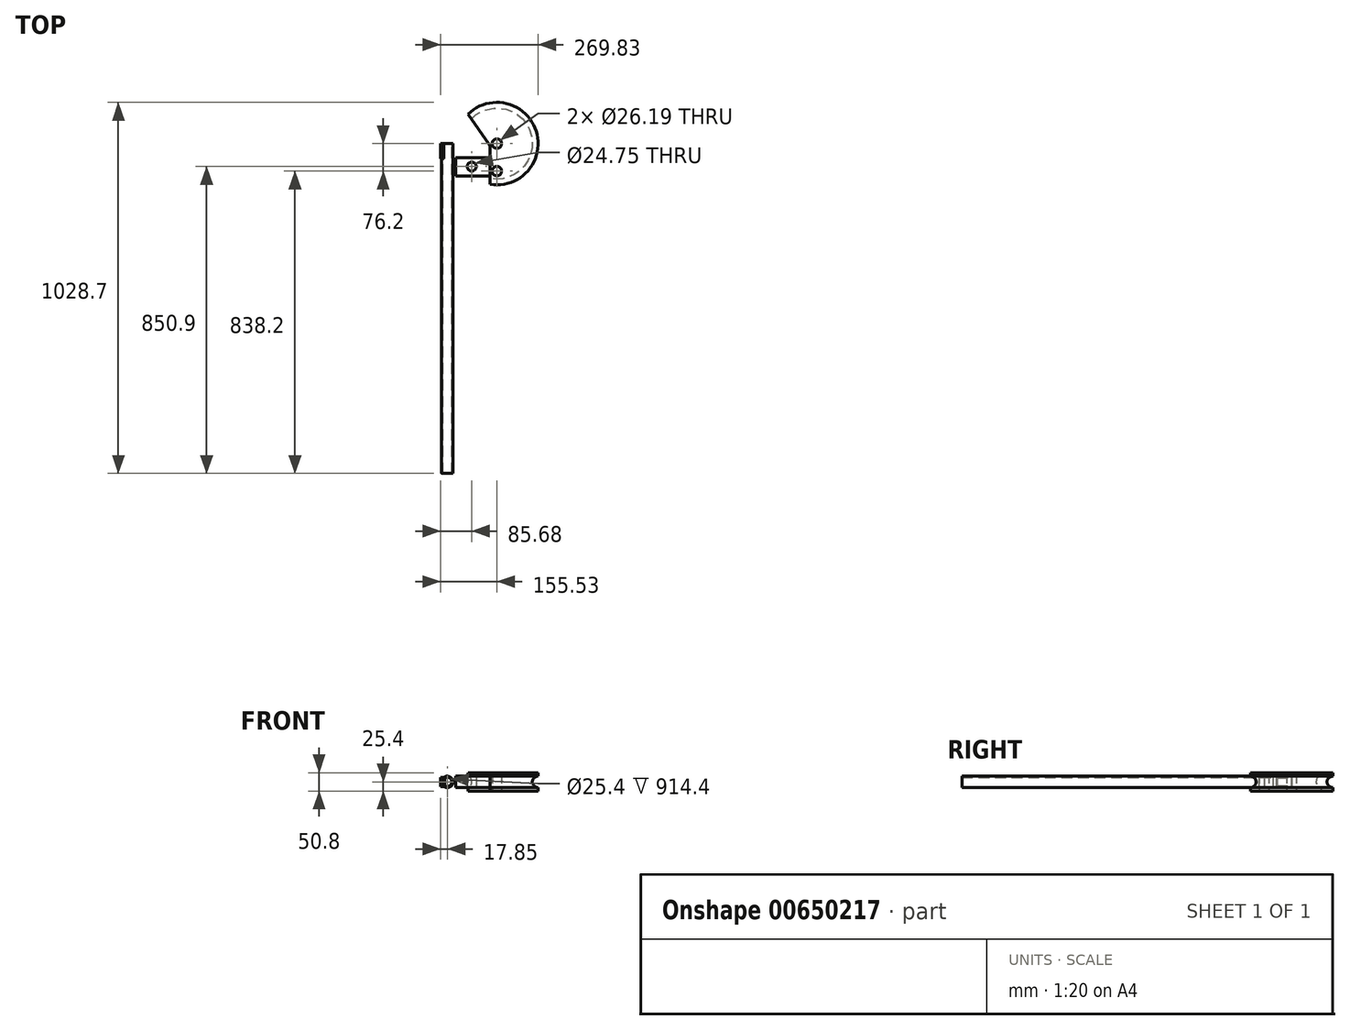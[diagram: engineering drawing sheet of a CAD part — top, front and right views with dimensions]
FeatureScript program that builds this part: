
annotation { "Feature Type Name" : "Feature", "Feature Type Description" : "" }
export const myFeature = defineFeature(function(context is Context, id is Id, definition is map)
    precondition{}
    {
        {
            var Q0;
            Q0=qCreatedBy(makeId("Top.planeOp"),FACE);
            var sketch = newSketch(context, id + "F0", { "sketchPlane" : qUnion([Q0])});
            skArc(sketch, "E0", {"start": v(-19.05, -112.7) * mm, "mid": v(109, 34.37) * mm, "end": v(-80.25, 81.4) * mm});
            skCircle(sketch, "E1", {"center": v(0, 0) * mm, "radius": 13.1 * mm});
            skLineSegment(sketch, "E2", {"start": v(0, 0) * mm, "end": v(0, -166.98) * mm, "construction": true});
            skLineSegment(sketch, "E3", {"start": v(0, 0) * mm, "end": v(-105.24, 150.3) * mm, "construction": true});
            skLineSegment(sketch, "E4.0", {"start": v(-19.05, -6) * mm, "end": v(-80.25, 81.4) * mm});
            skLineSegment(sketch, "E4.1", {"start": v(-19.05, -6) * mm, "end": v(-19.05, -112.7) * mm});
            skSolve(sketch);
        }
        {
            var Q0;
            Q0 = qSketchRegion(id + "F0", true);
            extrude(context, id + "F1", {"entities" : qUnion([Q0]), "endBound" : BoundingType.SYMMETRIC, "depth" : 50.8 * mm, "offsetDistance" : 25.4 * mm});
        }
        {
            var Q0;
            Q0=qCreatedBy(makeId("Top.planeOp"),FACE);
            var sketch = newSketch(context, id + "F2", { "sketchPlane" : qUnion([Q0])});
            skLineSegment(sketch, "E5", {"start": v(14.64, 175.52) * mm, "end": v(14.64, 166) * mm});
            skLineSegment(sketch, "E6", {"start": v(22.02, 212) * mm, "end": v(23.53, 220.42) * mm});
            skLineSegment(sketch, "E7", {"start": v(21.47, 208.86) * mm, "end": v(21.75, 210.43) * mm});
            skLineSegment(sketch, "E8", {"start": v(19.5, 197.94) * mm, "end": v(21.18, 207.32) * mm});
            skLineSegment(sketch, "E9", {"start": v(18.95, 194.8) * mm, "end": v(19.23, 196.37) * mm});
            skLineSegment(sketch, "E10", {"start": v(16.99, 183.86) * mm, "end": v(18.66, 193.24) * mm});
            skLineSegment(sketch, "E11", {"start": v(16.44, 180.75) * mm, "end": v(16.71, 182.3) * mm});
            skLineSegment(sketch, "E12", {"start": v(14.64, 170.76) * mm, "end": v(16.16, 179.19) * mm});
            skLineSegment(sketch, "E13", {"start": v(208.16, 163.65) * mm, "end": v(205.14, 165.03) * mm});
            skLineSegment(sketch, "E14", {"start": v(207.72, 164.56) * mm, "end": v(207.57, 164.88) * mm});
            skLineSegment(sketch, "E15", {"start": v(207.57, 164.88) * mm, "end": v(207.25, 165.17) * mm});
            skLineSegment(sketch, "E16", {"start": v(207.25, 165.17) * mm, "end": v(206.8, 165.32) * mm});
            skLineSegment(sketch, "E17", {"start": v(206.8, 165.32) * mm, "end": v(206.51, 165.32) * mm});
            skLineSegment(sketch, "E18", {"start": v(206.51, 165.32) * mm, "end": v(206.05, 165.17) * mm});
            skLineSegment(sketch, "E19", {"start": v(206.05, 165.17) * mm, "end": v(205.75, 164.88) * mm});
            skLineSegment(sketch, "E20", {"start": v(205.75, 164.88) * mm, "end": v(205.6, 164.56) * mm});
            skLineSegment(sketch, "E21", {"start": v(205.6, 164.56) * mm, "end": v(205.6, 164.12) * mm});
            skLineSegment(sketch, "E22", {"start": v(205.6, 164.12) * mm, "end": v(205.75, 163.82) * mm});
            skLineSegment(sketch, "E23", {"start": v(205.75, 163.82) * mm, "end": v(206.05, 163.5) * mm});
            skLineSegment(sketch, "E24", {"start": v(206.05, 163.5) * mm, "end": v(206.51, 163.35) * mm});
            skLineSegment(sketch, "E25", {"start": v(206.51, 163.35) * mm, "end": v(206.8, 163.35) * mm});
            skLineSegment(sketch, "E26", {"start": v(206.8, 163.35) * mm, "end": v(207.25, 163.5) * mm});
            skLineSegment(sketch, "E27", {"start": v(207.25, 163.5) * mm, "end": v(207.57, 163.82) * mm});
            skLineSegment(sketch, "E28", {"start": v(207.57, 163.82) * mm, "end": v(207.72, 164.12) * mm});
            skLineSegment(sketch, "E29", {"start": v(207.72, 164.12) * mm, "end": v(207.72, 164.56) * mm});
            skLineSegment(sketch, "E30", {"start": v(208.78, 166.38) * mm, "end": v(208.63, 166.53) * mm});
            skLineSegment(sketch, "E31", {"start": v(208.63, 166.53) * mm, "end": v(208.78, 166.68) * mm});
            skLineSegment(sketch, "E32", {"start": v(208.78, 166.68) * mm, "end": v(208.93, 166.53) * mm});
            skLineSegment(sketch, "E33", {"start": v(208.93, 166.53) * mm, "end": v(208.78, 166.38) * mm});
            skLineSegment(sketch, "E34", {"start": v(208.78, 166.38) * mm, "end": v(208.48, 166.38) * mm});
            skLineSegment(sketch, "E35", {"start": v(208.48, 166.38) * mm, "end": v(208.16, 166.53) * mm});
            skLineSegment(sketch, "E36", {"start": v(208.16, 166.53) * mm, "end": v(208.02, 166.68) * mm});
            skLineSegment(sketch, "E37", {"start": v(208.78, 167.3) * mm, "end": v(208.63, 167.44) * mm});
            skLineSegment(sketch, "E38", {"start": v(208.63, 167.44) * mm, "end": v(208.78, 167.59) * mm});
            skLineSegment(sketch, "E39", {"start": v(208.78, 167.59) * mm, "end": v(208.93, 167.44) * mm});
            skLineSegment(sketch, "E40", {"start": v(208.93, 167.44) * mm, "end": v(208.78, 167.3) * mm});
            skLineSegment(sketch, "E41", {"start": v(208.78, 167.3) * mm, "end": v(208.48, 167.3) * mm});
            skLineSegment(sketch, "E42", {"start": v(208.48, 167.3) * mm, "end": v(208.16, 167.44) * mm});
            skLineSegment(sketch, "E43", {"start": v(208.16, 167.44) * mm, "end": v(208.02, 167.59) * mm});
            skLineSegment(sketch, "E44", {"start": v(206.2, 170.61) * mm, "end": v(205.92, 170.57) * mm});
            skLineSegment(sketch, "E45", {"start": v(205.92, 170.57) * mm, "end": v(205.67, 170.47) * mm});
            skLineSegment(sketch, "E46", {"start": v(205.67, 170.47) * mm, "end": v(205.45, 170.3) * mm});
            skLineSegment(sketch, "E47", {"start": v(205.45, 170.3) * mm, "end": v(205.28, 170.08) * mm});
            skLineSegment(sketch, "E48", {"start": v(205.28, 170.08) * mm, "end": v(205.18, 169.83) * mm});
            skLineSegment(sketch, "E49", {"start": v(205.18, 169.83) * mm, "end": v(205.14, 169.56) * mm});
            skLineSegment(sketch, "E50", {"start": v(205.14, 169.56) * mm, "end": v(205.18, 169.28) * mm});
            skLineSegment(sketch, "E51", {"start": v(205.18, 169.28) * mm, "end": v(205.28, 169.03) * mm});
            skLineSegment(sketch, "E52", {"start": v(205.28, 169.03) * mm, "end": v(205.45, 168.81) * mm});
            skLineSegment(sketch, "E53", {"start": v(205.45, 168.81) * mm, "end": v(205.67, 168.65) * mm});
            skLineSegment(sketch, "E54", {"start": v(205.67, 168.65) * mm, "end": v(205.92, 168.54) * mm});
            skLineSegment(sketch, "E55", {"start": v(205.92, 168.54) * mm, "end": v(206.2, 168.5) * mm});
            skLineSegment(sketch, "E56", {"start": v(206.2, 168.5) * mm, "end": v(207.25, 168.5) * mm});
            skLineSegment(sketch, "E57", {"start": v(207.25, 168.5) * mm, "end": v(207.53, 168.54) * mm});
            skLineSegment(sketch, "E58", {"start": v(207.53, 168.54) * mm, "end": v(207.78, 168.65) * mm});
            skLineSegment(sketch, "E59", {"start": v(207.78, 168.65) * mm, "end": v(208.02, 168.81) * mm});
            skLineSegment(sketch, "E60", {"start": v(208.02, 168.81) * mm, "end": v(208.18, 169.03) * mm});
            skLineSegment(sketch, "E61", {"start": v(208.18, 169.03) * mm, "end": v(208.3, 169.28) * mm});
            skLineSegment(sketch, "E62", {"start": v(208.3, 169.28) * mm, "end": v(208.31, 169.56) * mm});
            skLineSegment(sketch, "E63", {"start": v(208.31, 169.56) * mm, "end": v(208.3, 169.83) * mm});
            skLineSegment(sketch, "E64", {"start": v(208.3, 169.83) * mm, "end": v(208.18, 170.08) * mm});
            skLineSegment(sketch, "E65", {"start": v(208.18, 170.08) * mm, "end": v(208.02, 170.3) * mm});
            skLineSegment(sketch, "E66", {"start": v(208.02, 170.3) * mm, "end": v(207.78, 170.47) * mm});
            skLineSegment(sketch, "E67", {"start": v(207.78, 170.47) * mm, "end": v(207.53, 170.57) * mm});
            skLineSegment(sketch, "E68", {"start": v(207.53, 170.57) * mm, "end": v(207.25, 170.61) * mm});
            skLineSegment(sketch, "E69", {"start": v(207.25, 170.61) * mm, "end": v(206.2, 170.61) * mm});
            skLineSegment(sketch, "E70", {"start": v(206.2, 173.64) * mm, "end": v(205.92, 173.6) * mm});
            skLineSegment(sketch, "E71", {"start": v(205.92, 173.6) * mm, "end": v(205.67, 173.5) * mm});
            skLineSegment(sketch, "E72", {"start": v(205.67, 173.5) * mm, "end": v(205.45, 173.32) * mm});
            skLineSegment(sketch, "E73", {"start": v(205.45, 173.32) * mm, "end": v(205.28, 173.11) * mm});
            skLineSegment(sketch, "E74", {"start": v(205.28, 173.11) * mm, "end": v(205.18, 172.86) * mm});
            skLineSegment(sketch, "E75", {"start": v(205.18, 172.86) * mm, "end": v(205.14, 172.58) * mm});
            skLineSegment(sketch, "E76", {"start": v(205.14, 172.58) * mm, "end": v(205.18, 172.3) * mm});
            skLineSegment(sketch, "E77", {"start": v(205.18, 172.3) * mm, "end": v(205.28, 172.05) * mm});
            skLineSegment(sketch, "E78", {"start": v(205.28, 172.05) * mm, "end": v(205.45, 171.84) * mm});
            skLineSegment(sketch, "E79", {"start": v(205.45, 171.84) * mm, "end": v(205.67, 171.67) * mm});
            skLineSegment(sketch, "E80", {"start": v(205.67, 171.67) * mm, "end": v(205.92, 171.57) * mm});
            skLineSegment(sketch, "E81", {"start": v(205.92, 171.57) * mm, "end": v(206.2, 171.52) * mm});
            skLineSegment(sketch, "E82", {"start": v(206.2, 171.52) * mm, "end": v(207.25, 171.52) * mm});
            skLineSegment(sketch, "E83", {"start": v(207.25, 171.52) * mm, "end": v(207.53, 171.57) * mm});
            skLineSegment(sketch, "E84", {"start": v(207.53, 171.57) * mm, "end": v(207.78, 171.67) * mm});
            skLineSegment(sketch, "E85", {"start": v(207.78, 171.67) * mm, "end": v(208.02, 171.84) * mm});
            skLineSegment(sketch, "E86", {"start": v(208.02, 171.84) * mm, "end": v(208.18, 172.05) * mm});
            skLineSegment(sketch, "E87", {"start": v(208.18, 172.05) * mm, "end": v(208.3, 172.3) * mm});
            skLineSegment(sketch, "E88", {"start": v(208.3, 172.3) * mm, "end": v(208.31, 172.58) * mm});
            skLineSegment(sketch, "E89", {"start": v(208.31, 172.58) * mm, "end": v(208.3, 172.86) * mm});
            skLineSegment(sketch, "E90", {"start": v(208.3, 172.86) * mm, "end": v(208.18, 173.11) * mm});
            skLineSegment(sketch, "E91", {"start": v(208.18, 173.11) * mm, "end": v(208.02, 173.32) * mm});
            skLineSegment(sketch, "E92", {"start": v(208.02, 173.32) * mm, "end": v(207.78, 173.5) * mm});
            skLineSegment(sketch, "E93", {"start": v(207.78, 173.5) * mm, "end": v(207.53, 173.6) * mm});
            skLineSegment(sketch, "E94", {"start": v(207.53, 173.6) * mm, "end": v(207.25, 173.64) * mm});
            skLineSegment(sketch, "E95", {"start": v(207.25, 173.64) * mm, "end": v(206.2, 173.64) * mm});
            skLineSegment(sketch, "E96", {"start": v(205.45, 175) * mm, "end": v(205.3, 175.14) * mm});
            skLineSegment(sketch, "E97", {"start": v(205.3, 175.14) * mm, "end": v(205.14, 175) * mm});
            skLineSegment(sketch, "E98", {"start": v(205.14, 175) * mm, "end": v(205.3, 174.85) * mm});
            skLineSegment(sketch, "E99", {"start": v(207.25, 176.2) * mm, "end": v(206.8, 176.35) * mm});
            skLineSegment(sketch, "E100", {"start": v(206.8, 176.35) * mm, "end": v(206.51, 176.67) * mm});
            skLineSegment(sketch, "E101", {"start": v(206.51, 176.67) * mm, "end": v(206.36, 177.11) * mm});
            skLineSegment(sketch, "E102", {"start": v(206.36, 177.11) * mm, "end": v(206.36, 177.26) * mm});
            skLineSegment(sketch, "E103", {"start": v(206.36, 177.26) * mm, "end": v(206.51, 177.73) * mm});
            skLineSegment(sketch, "E104", {"start": v(206.51, 177.73) * mm, "end": v(206.8, 178.02) * mm});
            skLineSegment(sketch, "E105", {"start": v(206.8, 178.02) * mm, "end": v(207.25, 178.17) * mm});
            skLineSegment(sketch, "E106", {"start": v(207.25, 178.17) * mm, "end": v(207.42, 178.17) * mm});
            skLineSegment(sketch, "E107", {"start": v(207.42, 178.17) * mm, "end": v(207.87, 178.02) * mm});
            skLineSegment(sketch, "E108", {"start": v(207.87, 178.02) * mm, "end": v(208.16, 177.73) * mm});
            skLineSegment(sketch, "E109", {"start": v(208.16, 177.73) * mm, "end": v(208.31, 177.26) * mm});
            skLineSegment(sketch, "E110", {"start": v(208.31, 177.26) * mm, "end": v(208.31, 177.11) * mm});
            skLineSegment(sketch, "E111", {"start": v(208.31, 177.11) * mm, "end": v(208.16, 176.67) * mm});
            skLineSegment(sketch, "E112", {"start": v(208.16, 176.67) * mm, "end": v(207.87, 176.35) * mm});
            skLineSegment(sketch, "E113", {"start": v(207.87, 176.35) * mm, "end": v(207.25, 176.2) * mm});
            skLineSegment(sketch, "E114", {"start": v(207.25, 176.2) * mm, "end": v(206.51, 176.2) * mm});
            skLineSegment(sketch, "E115", {"start": v(206.51, 176.2) * mm, "end": v(205.75, 176.35) * mm});
            skLineSegment(sketch, "E116", {"start": v(205.75, 176.35) * mm, "end": v(205.3, 176.67) * mm});
            skLineSegment(sketch, "E117", {"start": v(205.3, 176.67) * mm, "end": v(205.14, 177.11) * mm});
            skLineSegment(sketch, "E118", {"start": v(205.14, 177.11) * mm, "end": v(205.14, 177.4) * mm});
            skLineSegment(sketch, "E119", {"start": v(205.14, 177.4) * mm, "end": v(205.3, 177.87) * mm});
            skLineSegment(sketch, "E120", {"start": v(205.3, 177.87) * mm, "end": v(205.6, 178.02) * mm});
            skLineSegment(sketch, "E121", {"start": v(203.55, 285.06) * mm, "end": v(203.55, 56.46) * mm});
            skLineSegment(sketch, "E122", {"start": v(153.2, 90.07) * mm, "end": v(154.97, 93.2) * mm});
            skLineSegment(sketch, "E123", {"start": v(154.97, 93.2) * mm, "end": v(156.69, 96.4) * mm});
            skLineSegment(sketch, "E124", {"start": v(156.69, 96.4) * mm, "end": v(158.34, 99.62) * mm});
            skLineSegment(sketch, "E125", {"start": v(158.34, 99.62) * mm, "end": v(159.9, 102.88) * mm});
            skLineSegment(sketch, "E126", {"start": v(159.9, 102.88) * mm, "end": v(161.39, 106.16) * mm});
            skLineSegment(sketch, "E127", {"start": v(161.39, 106.16) * mm, "end": v(162.8, 109.48) * mm});
            skLineSegment(sketch, "E128", {"start": v(162.8, 109.48) * mm, "end": v(164.16, 112.85) * mm});
            skLineSegment(sketch, "E129", {"start": v(164.16, 112.85) * mm, "end": v(165.43, 116.24) * mm});
            skLineSegment(sketch, "E130", {"start": v(165.43, 116.24) * mm, "end": v(166.61, 119.64) * mm});
            skLineSegment(sketch, "E131", {"start": v(166.61, 119.64) * mm, "end": v(167.74, 123.1) * mm});
            skLineSegment(sketch, "E132", {"start": v(167.74, 123.1) * mm, "end": v(168.77, 126.54) * mm});
            skLineSegment(sketch, "E133", {"start": v(168.77, 126.54) * mm, "end": v(169.72, 130.04) * mm});
            skLineSegment(sketch, "E134", {"start": v(169.72, 130.04) * mm, "end": v(170.6, 133.53) * mm});
            skLineSegment(sketch, "E135", {"start": v(170.6, 133.53) * mm, "end": v(171.4, 137.06) * mm});
            skLineSegment(sketch, "E136", {"start": v(171.4, 137.06) * mm, "end": v(172.12, 140.6) * mm});
            skLineSegment(sketch, "E137", {"start": v(172.12, 140.6) * mm, "end": v(172.75, 144.16) * mm});
            skLineSegment(sketch, "E138", {"start": v(172.75, 144.16) * mm, "end": v(173.32, 147.73) * mm});
            skLineSegment(sketch, "E139", {"start": v(173.32, 147.73) * mm, "end": v(173.79, 151.3) * mm});
            skLineSegment(sketch, "E140", {"start": v(173.79, 151.3) * mm, "end": v(174.2, 154.9) * mm});
            skLineSegment(sketch, "E141", {"start": v(174.2, 154.9) * mm, "end": v(174.5, 158.5) * mm});
            skLineSegment(sketch, "E142", {"start": v(174.5, 158.5) * mm, "end": v(174.74, 162.13) * mm});
            skLineSegment(sketch, "E143", {"start": v(174.74, 162.13) * mm, "end": v(174.91, 165.72) * mm});
            skLineSegment(sketch, "E144", {"start": v(174.91, 165.72) * mm, "end": v(174.97, 169.34) * mm});
            skLineSegment(sketch, "E145", {"start": v(174.97, 169.34) * mm, "end": v(174.97, 172.96) * mm});
            skLineSegment(sketch, "E146", {"start": v(174.97, 172.96) * mm, "end": v(174.87, 176.56) * mm});
            skLineSegment(sketch, "E147", {"start": v(174.87, 176.56) * mm, "end": v(174.7, 180.18) * mm});
            skLineSegment(sketch, "E148", {"start": v(174.7, 180.18) * mm, "end": v(174.45, 183.78) * mm});
            skLineSegment(sketch, "E149", {"start": v(174.45, 183.78) * mm, "end": v(174.13, 187.38) * mm});
            skLineSegment(sketch, "E150", {"start": v(102.06, 169.92) * mm, "end": v(99.03, 171.3) * mm});
            skLineSegment(sketch, "E151", {"start": v(101.61, 170.83) * mm, "end": v(101.46, 171.14) * mm});
            skLineSegment(sketch, "E152", {"start": v(101.46, 171.14) * mm, "end": v(101.14, 171.44) * mm});
            skLineSegment(sketch, "E153", {"start": v(101.14, 171.44) * mm, "end": v(100.7, 171.59) * mm});
            skLineSegment(sketch, "E154", {"start": v(100.7, 171.59) * mm, "end": v(100.4, 171.59) * mm});
            skLineSegment(sketch, "E155", {"start": v(100.4, 171.59) * mm, "end": v(99.94, 171.44) * mm});
            skLineSegment(sketch, "E156", {"start": v(99.94, 171.44) * mm, "end": v(99.64, 171.14) * mm});
            skLineSegment(sketch, "E157", {"start": v(99.64, 171.14) * mm, "end": v(99.5, 170.83) * mm});
            skLineSegment(sketch, "E158", {"start": v(99.5, 170.83) * mm, "end": v(99.5, 170.38) * mm});
            skLineSegment(sketch, "E159", {"start": v(99.5, 170.38) * mm, "end": v(99.64, 170.08) * mm});
            skLineSegment(sketch, "E160", {"start": v(99.64, 170.08) * mm, "end": v(99.94, 169.77) * mm});
            skLineSegment(sketch, "E161", {"start": v(99.94, 169.77) * mm, "end": v(100.4, 169.62) * mm});
            skLineSegment(sketch, "E162", {"start": v(100.4, 169.62) * mm, "end": v(100.7, 169.62) * mm});
            skLineSegment(sketch, "E163", {"start": v(100.7, 169.62) * mm, "end": v(101.14, 169.77) * mm});
            skLineSegment(sketch, "E164", {"start": v(101.14, 169.77) * mm, "end": v(101.46, 170.08) * mm});
            skLineSegment(sketch, "E165", {"start": v(101.46, 170.08) * mm, "end": v(101.61, 170.38) * mm});
            skLineSegment(sketch, "E166", {"start": v(101.61, 170.38) * mm, "end": v(101.61, 170.83) * mm});
            skLineSegment(sketch, "E167", {"start": v(101.61, 174) * mm, "end": v(101.76, 173.7) * mm});
            skLineSegment(sketch, "E168", {"start": v(101.76, 173.7) * mm, "end": v(102.2, 173.26) * mm});
            skLineSegment(sketch, "E169", {"start": v(102.2, 173.26) * mm, "end": v(99.03, 173.26) * mm});
            skLineSegment(sketch, "E170", {"start": v(102.2, 176.73) * mm, "end": v(102.2, 175.06) * mm});
            skLineSegment(sketch, "E171", {"start": v(102.2, 175.06) * mm, "end": v(101, 175.97) * mm});
            skLineSegment(sketch, "E172", {"start": v(101, 175.97) * mm, "end": v(101, 175.52) * mm});
            skLineSegment(sketch, "E173", {"start": v(101, 175.52) * mm, "end": v(100.85, 175.2) * mm});
            skLineSegment(sketch, "E174", {"start": v(100.85, 175.2) * mm, "end": v(100.7, 175.06) * mm});
            skLineSegment(sketch, "E175", {"start": v(100.7, 175.06) * mm, "end": v(100.23, 174.91) * mm});
            skLineSegment(sketch, "E176", {"start": v(100.23, 174.91) * mm, "end": v(99.94, 174.91) * mm});
            skLineSegment(sketch, "E177", {"start": v(99.94, 174.91) * mm, "end": v(99.5, 175.06) * mm});
            skLineSegment(sketch, "E178", {"start": v(99.5, 175.06) * mm, "end": v(99.18, 175.38) * mm});
            skLineSegment(sketch, "E179", {"start": v(99.18, 175.38) * mm, "end": v(99.03, 175.82) * mm});
            skLineSegment(sketch, "E180", {"start": v(99.03, 175.82) * mm, "end": v(99.03, 176.27) * mm});
            skLineSegment(sketch, "E181", {"start": v(99.03, 176.27) * mm, "end": v(99.18, 176.73) * mm});
            skLineSegment(sketch, "E182", {"start": v(99.18, 176.73) * mm, "end": v(99.32, 176.88) * mm});
            skLineSegment(sketch, "E183", {"start": v(99.32, 176.88) * mm, "end": v(99.64, 177.03) * mm});
            skLineSegment(sketch, "E184", {"start": v(100.09, 180.05) * mm, "end": v(99.81, 180.01) * mm});
            skLineSegment(sketch, "E185", {"start": v(99.81, 180.01) * mm, "end": v(99.56, 179.9) * mm});
            skLineSegment(sketch, "E186", {"start": v(99.56, 179.9) * mm, "end": v(99.35, 179.74) * mm});
            skLineSegment(sketch, "E187", {"start": v(99.35, 179.74) * mm, "end": v(99.18, 179.53) * mm});
            skLineSegment(sketch, "E188", {"start": v(99.18, 179.53) * mm, "end": v(99.07, 179.27) * mm});
            skLineSegment(sketch, "E189", {"start": v(99.07, 179.27) * mm, "end": v(99.03, 179) * mm});
            skLineSegment(sketch, "E190", {"start": v(99.03, 179) * mm, "end": v(99.07, 178.72) * mm});
            skLineSegment(sketch, "E191", {"start": v(99.07, 178.72) * mm, "end": v(99.18, 178.47) * mm});
            skLineSegment(sketch, "E192", {"start": v(99.18, 178.47) * mm, "end": v(99.35, 178.26) * mm});
            skLineSegment(sketch, "E193", {"start": v(99.35, 178.26) * mm, "end": v(99.56, 178.09) * mm});
            skLineSegment(sketch, "E194", {"start": v(99.56, 178.09) * mm, "end": v(99.81, 177.98) * mm});
            skLineSegment(sketch, "E195", {"start": v(99.81, 177.98) * mm, "end": v(100.09, 177.94) * mm});
            skLineSegment(sketch, "E196", {"start": v(100.09, 177.94) * mm, "end": v(101.14, 177.94) * mm});
            skLineSegment(sketch, "E197", {"start": v(101.14, 177.94) * mm, "end": v(101.42, 177.98) * mm});
            skLineSegment(sketch, "E198", {"start": v(101.42, 177.98) * mm, "end": v(101.67, 178.09) * mm});
            skLineSegment(sketch, "E199", {"start": v(101.67, 178.09) * mm, "end": v(101.9, 178.26) * mm});
            skLineSegment(sketch, "E200", {"start": v(101.9, 178.26) * mm, "end": v(102.06, 178.47) * mm});
            skLineSegment(sketch, "E201", {"start": v(102.06, 178.47) * mm, "end": v(102.16, 178.72) * mm});
            skLineSegment(sketch, "E202", {"start": v(102.16, 178.72) * mm, "end": v(102.2, 179) * mm});
            skLineSegment(sketch, "E203", {"start": v(102.2, 179) * mm, "end": v(102.16, 179.27) * mm});
            skLineSegment(sketch, "E204", {"start": v(102.16, 179.27) * mm, "end": v(102.06, 179.53) * mm});
            skLineSegment(sketch, "E205", {"start": v(102.06, 179.53) * mm, "end": v(101.9, 179.74) * mm});
            skLineSegment(sketch, "E206", {"start": v(101.9, 179.74) * mm, "end": v(101.67, 179.9) * mm});
            skLineSegment(sketch, "E207", {"start": v(101.67, 179.9) * mm, "end": v(101.42, 180.01) * mm});
            skLineSegment(sketch, "E208", {"start": v(101.42, 180.01) * mm, "end": v(101.14, 180.05) * mm});
            skLineSegment(sketch, "E209", {"start": v(101.14, 180.05) * mm, "end": v(100.09, 180.05) * mm});
            skLineSegment(sketch, "E210", {"start": v(99.32, 181.4) * mm, "end": v(99.18, 181.56) * mm});
            skLineSegment(sketch, "E211", {"start": v(99.18, 181.56) * mm, "end": v(99.03, 181.4) * mm});
            skLineSegment(sketch, "E212", {"start": v(99.03, 181.4) * mm, "end": v(99.18, 181.26) * mm});
            skLineSegment(sketch, "E213", {"start": v(101.61, 184) * mm, "end": v(101.76, 183.67) * mm});
            skLineSegment(sketch, "E214", {"start": v(101.76, 183.67) * mm, "end": v(102.2, 183.23) * mm});
            skLineSegment(sketch, "E215", {"start": v(102.2, 183.23) * mm, "end": v(99.03, 183.23) * mm});
            skLineSegment(sketch, "E216", {"start": v(-28.99, 199.87) * mm, "end": v(-30.47, 198.79) * mm});
            skLineSegment(sketch, "E217", {"start": v(-30.47, 198.79) * mm, "end": v(-31.93, 197.62) * mm});
            skLineSegment(sketch, "E218", {"start": v(-31.93, 197.62) * mm, "end": v(-33.3, 196.42) * mm});
            skLineSegment(sketch, "E219", {"start": v(-33.3, 196.42) * mm, "end": v(-34.64, 195.15) * mm});
            skLineSegment(sketch, "E220", {"start": v(-34.64, 195.15) * mm, "end": v(-35.93, 193.81) * mm});
            skLineSegment(sketch, "E221", {"start": v(-35.93, 193.81) * mm, "end": v(-37.14, 192.42) * mm});
            skLineSegment(sketch, "E222", {"start": v(-37.14, 192.42) * mm, "end": v(-38.3, 191) * mm});
            skLineSegment(sketch, "E223", {"start": v(-38.3, 191) * mm, "end": v(-39.4, 189.5) * mm});
            skLineSegment(sketch, "E224", {"start": v(-39.4, 189.5) * mm, "end": v(-40.44, 187.97) * mm});
            skLineSegment(sketch, "E225", {"start": v(-40.44, 187.97) * mm, "end": v(-41.41, 186.4) * mm});
            skLineSegment(sketch, "E226", {"start": v(-41.41, 186.4) * mm, "end": v(-42.3, 184.8) * mm});
            skLineSegment(sketch, "E227", {"start": v(-42.3, 184.8) * mm, "end": v(-43.13, 183.14) * mm});
            skLineSegment(sketch, "E228", {"start": v(-43.13, 183.14) * mm, "end": v(-43.89, 181.45) * mm});
            skLineSegment(sketch, "E229", {"start": v(-43.89, 181.45) * mm, "end": v(-44.57, 179.74) * mm});
            skLineSegment(sketch, "E230", {"start": v(-44.57, 179.74) * mm, "end": v(-45.18, 178) * mm});
            skLineSegment(sketch, "E231", {"start": v(-45.18, 178) * mm, "end": v(-45.7, 176.22) * mm});
            skLineSegment(sketch, "E232", {"start": v(-45.7, 176.22) * mm, "end": v(-46.15, 174.45) * mm});
            skLineSegment(sketch, "E233", {"start": v(-46.15, 174.45) * mm, "end": v(-46.53, 172.62) * mm});
            skLineSegment(sketch, "E234", {"start": v(-46.53, 172.62) * mm, "end": v(-46.83, 170.8) * mm});
            skLineSegment(sketch, "E235", {"start": v(-46.83, 170.8) * mm, "end": v(-47.06, 168.98) * mm});
            skLineSegment(sketch, "E236", {"start": v(-47.06, 168.98) * mm, "end": v(-47.21, 167.14) * mm});
            skLineSegment(sketch, "E237", {"start": v(-47.21, 167.14) * mm, "end": v(-47.25, 165.3) * mm});
            skLineSegment(sketch, "E238", {"start": v(-47.25, 165.3) * mm, "end": v(-47.25, 163.44) * mm});
            skLineSegment(sketch, "E239", {"start": v(-47.25, 163.44) * mm, "end": v(-47.15, 161.6) * mm});
            skLineSegment(sketch, "E240", {"start": v(-47.15, 161.6) * mm, "end": v(-46.98, 159.78) * mm});
            skLineSegment(sketch, "E241", {"start": v(-46.98, 159.78) * mm, "end": v(-46.73, 157.94) * mm});
            skLineSegment(sketch, "E242", {"start": v(-46.73, 157.94) * mm, "end": v(-46.39, 156.11) * mm});
            skLineSegment(sketch, "E243", {"start": v(109.5, 225.54) * mm, "end": v(113.63, 227.91) * mm});
            skLineSegment(sketch, "E244", {"start": v(106.75, 223.95) * mm, "end": v(108.13, 224.74) * mm});
            skLineSegment(sketch, "E245", {"start": v(97.12, 218.39) * mm, "end": v(105.38, 223.15) * mm});
            skLineSegment(sketch, "E246", {"start": v(94.4, 216.8) * mm, "end": v(95.77, 217.6) * mm});
            skLineSegment(sketch, "E247", {"start": v(84.76, 211.25) * mm, "end": v(93.02, 216.02) * mm});
            skLineSegment(sketch, "E248", {"start": v(82.01, 209.67) * mm, "end": v(83.39, 210.45) * mm});
            skLineSegment(sketch, "E249", {"start": v(72.38, 204.1) * mm, "end": v(80.63, 208.86) * mm});
            skLineSegment(sketch, "E250", {"start": v(69.63, 202.51) * mm, "end": v(71, 203.32) * mm});
            skLineSegment(sketch, "E251", {"start": v(60.02, 196.97) * mm, "end": v(68.25, 201.73) * mm});
            skLineSegment(sketch, "E252", {"start": v(57.27, 195.38) * mm, "end": v(58.64, 196.16) * mm});
            skLineSegment(sketch, "E253", {"start": v(47.64, 189.81) * mm, "end": v(55.9, 194.57) * mm});
            skLineSegment(sketch, "E254", {"start": v(44.88, 188.22) * mm, "end": v(46.26, 189.03) * mm});
            skLineSegment(sketch, "E255", {"start": v(35.27, 182.68) * mm, "end": v(43.5, 187.44) * mm});
            skLineSegment(sketch, "E256", {"start": v(32.52, 181.1) * mm, "end": v(33.9, 181.87) * mm});
            skLineSegment(sketch, "E257", {"start": v(22.9, 175.52) * mm, "end": v(31.15, 180.29) * mm});
            skLineSegment(sketch, "E258", {"start": v(20.14, 173.94) * mm, "end": v(21.52, 174.74) * mm});
            skLineSegment(sketch, "E259", {"start": v(14.64, 170.76) * mm, "end": v(18.76, 173.15) * mm});
            skLineSegment(sketch, "E260", {"start": v(52.1, 273.7) * mm, "end": v(53.73, 278.18) * mm});
            skLineSegment(sketch, "E261", {"start": v(51.02, 270.71) * mm, "end": v(51.57, 272.21) * mm});
            skLineSegment(sketch, "E262", {"start": v(47.21, 260.28) * mm, "end": v(50.47, 269.23) * mm});
            skLineSegment(sketch, "E263", {"start": v(46.13, 257.3) * mm, "end": v(46.68, 258.77) * mm});
            skLineSegment(sketch, "E264", {"start": v(42.34, 246.86) * mm, "end": v(45.58, 255.79) * mm});
            skLineSegment(sketch, "E265", {"start": v(41.24, 243.87) * mm, "end": v(41.8, 245.35) * mm});
            skLineSegment(sketch, "E266", {"start": v(37.45, 233.42) * mm, "end": v(40.71, 242.37) * mm});
            skLineSegment(sketch, "E267", {"start": v(36.35, 230.43) * mm, "end": v(36.9, 231.93) * mm});
            skLineSegment(sketch, "E268", {"start": v(32.56, 220) * mm, "end": v(35.82, 228.95) * mm});
            skLineSegment(sketch, "E269", {"start": v(31.49, 217.01) * mm, "end": v(32.01, 218.5) * mm});
            skLineSegment(sketch, "E270", {"start": v(27.68, 206.58) * mm, "end": v(30.94, 215.53) * mm});
            skLineSegment(sketch, "E271", {"start": v(26.6, 203.6) * mm, "end": v(27.13, 205.07) * mm});
            skLineSegment(sketch, "E272", {"start": v(22.79, 193.14) * mm, "end": v(26.05, 202.09) * mm});
            skLineSegment(sketch, "E273", {"start": v(21.7, 190.15) * mm, "end": v(22.24, 191.65) * mm});
            skLineSegment(sketch, "E274", {"start": v(17.9, 179.72) * mm, "end": v(21.16, 188.67) * mm});
            skLineSegment(sketch, "E275", {"start": v(16.82, 176.73) * mm, "end": v(17.37, 178.23) * mm});
            skLineSegment(sketch, "E276", {"start": v(11.9, 174.68) * mm, "end": v(14.64, 170.76) * mm});
            skLineSegment(sketch, "E277", {"start": v(14.64, 170.76) * mm, "end": v(16.27, 175.25) * mm});
            skLineSegment(sketch, "E278", {"start": v(10.09, 177.26) * mm, "end": v(11, 175.97) * mm});
            skLineSegment(sketch, "E279", {"start": v(3.71, 186.36) * mm, "end": v(9.18, 178.57) * mm});
            skLineSegment(sketch, "E280", {"start": v(1.9, 188.97) * mm, "end": v(2.8, 187.67) * mm});
            skLineSegment(sketch, "E281", {"start": v(-4.48, 198.07) * mm, "end": v(0.98, 190.28) * mm});
            skLineSegment(sketch, "E282", {"start": v(-6.3, 200.67) * mm, "end": v(-5.39, 199.38) * mm});
            skLineSegment(sketch, "E283", {"start": v(-12.67, 209.77) * mm, "end": v(-7.2, 201.98) * mm});
            skLineSegment(sketch, "E284", {"start": v(-14.49, 212.38) * mm, "end": v(-13.58, 211.08) * mm});
            skLineSegment(sketch, "E285", {"start": v(-20.86, 221.48) * mm, "end": v(-15.4, 213.69) * mm});
            skLineSegment(sketch, "E286", {"start": v(-22.68, 224.08) * mm, "end": v(-21.77, 222.79) * mm});
            skLineSegment(sketch, "E287", {"start": v(-29.07, 233.18) * mm, "end": v(-23.6, 225.4) * mm});
            skLineSegment(sketch, "E288", {"start": v(-30.9, 235.79) * mm, "end": v(-29.98, 234.5) * mm});
            skLineSegment(sketch, "E289", {"start": v(-37.26, 244.89) * mm, "end": v(-31.8, 237.08) * mm});
            skLineSegment(sketch, "E290", {"start": v(-39.08, 247.5) * mm, "end": v(-38.17, 246.2) * mm});
            skLineSegment(sketch, "E291", {"start": v(-45.46, 256.6) * mm, "end": v(-40, 248.78) * mm});
            skLineSegment(sketch, "E292", {"start": v(-47.28, 259.2) * mm, "end": v(-46.37, 257.88) * mm});
            skLineSegment(sketch, "E293", {"start": v(-50.92, 264.4) * mm, "end": v(-48.19, 260.49) * mm});
            skLineSegment(sketch, "E294", {"start": v(-36.44, 227.3) * mm, "end": v(-38, 225.84) * mm});
            skLineSegment(sketch, "E295", {"start": v(-38, 225.84) * mm, "end": v(-39.83, 224.04) * mm});
            skLineSegment(sketch, "E296", {"start": v(-39.83, 224.04) * mm, "end": v(-41.58, 222.2) * mm});
            skLineSegment(sketch, "E297", {"start": v(-41.58, 222.2) * mm, "end": v(-43.28, 220.27) * mm});
            skLineSegment(sketch, "E298", {"start": v(-34.05, 229.4) * mm, "end": v(-34.22, 229.25) * mm});
            skLineSegment(sketch, "E299", {"start": v(-34.22, 229.25) * mm, "end": v(-35.25, 228.36) * mm});
            skLineSegment(sketch, "E300", {"start": v(-25, 235.83) * mm, "end": v(-25.94, 235.26) * mm});
            skLineSegment(sketch, "E301", {"start": v(-25.94, 235.26) * mm, "end": v(-28.08, 233.86) * mm});
            skLineSegment(sketch, "E302", {"start": v(-28.08, 233.86) * mm, "end": v(-30.17, 232.4) * mm});
            skLineSegment(sketch, "E303", {"start": v(-30.17, 232.4) * mm, "end": v(-32.23, 230.85) * mm});
            skLineSegment(sketch, "E304", {"start": v(-32.23, 230.85) * mm, "end": v(-32.8, 230.39) * mm});
            skLineSegment(sketch, "E305", {"start": v(-22.26, 237.42) * mm, "end": v(-23.63, 236.65) * mm});
            skLineSegment(sketch, "E306", {"start": v(-12.18, 242.1) * mm, "end": v(-12.24, 242.07) * mm});
            skLineSegment(sketch, "E307", {"start": v(-12.24, 242.07) * mm, "end": v(-14.62, 241.12) * mm});
            skLineSegment(sketch, "E308", {"start": v(-14.62, 241.12) * mm, "end": v(-16.97, 240.1) * mm});
            skLineSegment(sketch, "E309", {"start": v(-16.97, 240.1) * mm, "end": v(-19.27, 239) * mm});
            skLineSegment(sketch, "E310", {"start": v(-19.27, 239) * mm, "end": v(-20.86, 238.18) * mm});
            skLineSegment(sketch, "E311", {"start": v(-9.18, 243.13) * mm, "end": v(-9.83, 242.92) * mm});
            skLineSegment(sketch, "E312", {"start": v(-9.83, 242.92) * mm, "end": v(-10.68, 242.62) * mm});
            skLineSegment(sketch, "E313", {"start": v(1.6, 245.82) * mm, "end": v(0.03, 245.54) * mm});
            skLineSegment(sketch, "E314", {"start": v(0.03, 245.54) * mm, "end": v(-2.47, 245.01) * mm});
            skLineSegment(sketch, "E315", {"start": v(-2.47, 245.01) * mm, "end": v(-4.94, 244.4) * mm});
            skLineSegment(sketch, "E316", {"start": v(-4.94, 244.4) * mm, "end": v(-7.4, 243.7) * mm});
            skLineSegment(sketch, "E317", {"start": v(-7.4, 243.7) * mm, "end": v(-7.67, 243.62) * mm});
            skLineSegment(sketch, "E318", {"start": v(4.73, 246.3) * mm, "end": v(3.16, 246.1) * mm});
            skLineSegment(sketch, "E319", {"start": v(15.8, 246.94) * mm, "end": v(15.27, 246.96) * mm});
            skLineSegment(sketch, "E320", {"start": v(15.27, 246.96) * mm, "end": v(12.71, 246.94) * mm});
            skLineSegment(sketch, "E321", {"start": v(12.71, 246.94) * mm, "end": v(10.15, 246.84) * mm});
            skLineSegment(sketch, "E322", {"start": v(10.15, 246.84) * mm, "end": v(7.6, 246.64) * mm});
            skLineSegment(sketch, "E323", {"start": v(7.6, 246.64) * mm, "end": v(6.3, 246.5) * mm});
            skLineSegment(sketch, "E324", {"start": v(18.98, 246.84) * mm, "end": v(17.81, 246.9) * mm});
            skLineSegment(sketch, "E325", {"start": v(17.81, 246.9) * mm, "end": v(17.39, 246.92) * mm});
            skLineSegment(sketch, "E326", {"start": v(29.98, 245.4) * mm, "end": v(27.97, 245.8) * mm});
            skLineSegment(sketch, "E327", {"start": v(27.97, 245.8) * mm, "end": v(25.45, 246.2) * mm});
            skLineSegment(sketch, "E328", {"start": v(25.45, 246.2) * mm, "end": v(22.91, 246.52) * mm});
            skLineSegment(sketch, "E329", {"start": v(22.91, 246.52) * mm, "end": v(20.56, 246.73) * mm});
            skLineSegment(sketch, "E330", {"start": v(33.1, 244.7) * mm, "end": v(32.97, 244.74) * mm});
            skLineSegment(sketch, "E331", {"start": v(32.97, 244.74) * mm, "end": v(31.55, 245.06) * mm});
            skLineSegment(sketch, "E332", {"start": v(43.64, 241.23) * mm, "end": v(42.68, 241.6) * mm});
            skLineSegment(sketch, "E333", {"start": v(42.68, 241.6) * mm, "end": v(40.3, 242.52) * mm});
            skLineSegment(sketch, "E334", {"start": v(40.3, 242.52) * mm, "end": v(37.88, 243.34) * mm});
            skLineSegment(sketch, "E335", {"start": v(37.88, 243.34) * mm, "end": v(35.44, 244.08) * mm});
            skLineSegment(sketch, "E336", {"start": v(35.44, 244.08) * mm, "end": v(34.62, 244.3) * mm});
            skLineSegment(sketch, "E337", {"start": v(46.53, 239.96) * mm, "end": v(45.1, 240.61) * mm});
            skLineSegment(sketch, "E338", {"start": v(56.27, 234.6) * mm, "end": v(54.11, 235.93) * mm});
            skLineSegment(sketch, "E339", {"start": v(54.11, 235.93) * mm, "end": v(51.91, 237.23) * mm});
            skLineSegment(sketch, "E340", {"start": v(51.91, 237.23) * mm, "end": v(49.67, 238.45) * mm});
            skLineSegment(sketch, "E341", {"start": v(49.67, 238.45) * mm, "end": v(47.97, 239.28) * mm});
            skLineSegment(sketch, "E342", {"start": v(58.88, 232.8) * mm, "end": v(58.39, 233.16) * mm});
            skLineSegment(sketch, "E343", {"start": v(58.39, 233.16) * mm, "end": v(57.58, 233.71) * mm});
            skLineSegment(sketch, "E344", {"start": v(67.43, 225.71) * mm, "end": v(66.35, 226.75) * mm});
            skLineSegment(sketch, "E345", {"start": v(66.35, 226.75) * mm, "end": v(64.44, 228.44) * mm});
            skLineSegment(sketch, "E346", {"start": v(64.44, 228.44) * mm, "end": v(62.47, 230.07) * mm});
            skLineSegment(sketch, "E347", {"start": v(62.47, 230.07) * mm, "end": v(60.46, 231.66) * mm});
            skLineSegment(sketch, "E348", {"start": v(60.46, 231.66) * mm, "end": v(60.17, 231.87) * mm});
            skLineSegment(sketch, "E349", {"start": v(69.67, 223.47) * mm, "end": v(68.57, 224.61) * mm});
            skLineSegment(sketch, "E350", {"start": v(76.74, 214.92) * mm, "end": v(76.49, 215.28) * mm});
            skLineSegment(sketch, "E351", {"start": v(76.49, 215.28) * mm, "end": v(74.96, 217.33) * mm});
            skLineSegment(sketch, "E352", {"start": v(74.96, 217.33) * mm, "end": v(73.37, 219.32) * mm});
            skLineSegment(sketch, "E353", {"start": v(73.37, 219.32) * mm, "end": v(71.7, 221.27) * mm});
            skLineSegment(sketch, "E354", {"start": v(71.7, 221.27) * mm, "end": v(70.75, 222.3) * mm});
            skLineSegment(sketch, "E355", {"start": v(78.54, 212.3) * mm, "end": v(77.95, 213.18) * mm});
            skLineSegment(sketch, "E356", {"start": v(77.95, 213.18) * mm, "end": v(77.65, 213.6) * mm});
            skLineSegment(sketch, "E357", {"start": v(83.9, 202.55) * mm, "end": v(83.05, 204.33) * mm});
            skLineSegment(sketch, "E358", {"start": v(83.05, 204.33) * mm, "end": v(81.88, 206.62) * mm});
            skLineSegment(sketch, "E359", {"start": v(81.88, 206.62) * mm, "end": v(80.63, 208.84) * mm});
            skLineSegment(sketch, "E360", {"start": v(80.63, 208.84) * mm, "end": v(79.39, 210.96) * mm});
            skLineSegment(sketch, "E361", {"start": v(85.16, 199.65) * mm, "end": v(85.14, 199.68) * mm});
            skLineSegment(sketch, "E362", {"start": v(85.14, 199.68) * mm, "end": v(84.53, 201.12) * mm});
            skLineSegment(sketch, "E363", {"start": v(88.6, 189.1) * mm, "end": v(88.38, 190) * mm});
            skLineSegment(sketch, "E364", {"start": v(88.38, 190) * mm, "end": v(87.68, 192.46) * mm});
            skLineSegment(sketch, "E365", {"start": v(87.68, 192.46) * mm, "end": v(86.92, 194.9) * mm});
            skLineSegment(sketch, "E366", {"start": v(86.92, 194.9) * mm, "end": v(86.07, 197.3) * mm});
            skLineSegment(sketch, "E367", {"start": v(86.07, 197.3) * mm, "end": v(85.74, 198.17) * mm});
            skLineSegment(sketch, "E368", {"start": v(89.3, 186) * mm, "end": v(88.97, 187.53) * mm});
            skLineSegment(sketch, "E369", {"start": v(88.97, 187.53) * mm, "end": v(88.97, 187.55) * mm});
            skLineSegment(sketch, "E370", {"start": v(90.73, 175) * mm, "end": v(90.56, 177.43) * mm});
            skLineSegment(sketch, "E371", {"start": v(90.56, 177.43) * mm, "end": v(90.29, 179.97) * mm});
            skLineSegment(sketch, "E372", {"start": v(90.29, 179.97) * mm, "end": v(89.93, 182.49) * mm});
            skLineSegment(sketch, "E373", {"start": v(89.93, 182.49) * mm, "end": v(89.6, 184.44) * mm});
            skLineSegment(sketch, "E374", {"start": v(90.84, 171.82) * mm, "end": v(90.84, 172.33) * mm});
            skLineSegment(sketch, "E375", {"start": v(90.84, 172.33) * mm, "end": v(90.8, 173.4) * mm});
            skLineSegment(sketch, "E376", {"start": v(90.18, 160.73) * mm, "end": v(90.35, 162.13) * mm});
            skLineSegment(sketch, "E377", {"start": v(90.35, 162.13) * mm, "end": v(90.6, 164.67) * mm});
            skLineSegment(sketch, "E378", {"start": v(90.6, 164.67) * mm, "end": v(90.75, 167.23) * mm});
            skLineSegment(sketch, "E379", {"start": v(90.75, 167.23) * mm, "end": v(90.84, 169.77) * mm});
            skLineSegment(sketch, "E380", {"start": v(90.84, 169.77) * mm, "end": v(90.84, 170.23) * mm});
            skLineSegment(sketch, "E381", {"start": v(89.7, 157.6) * mm, "end": v(89.95, 159.16) * mm});
            skLineSegment(sketch, "E382", {"start": v(86.98, 146.82) * mm, "end": v(87.1, 147.18) * mm});
            skLineSegment(sketch, "E383", {"start": v(87.1, 147.18) * mm, "end": v(87.85, 149.62) * mm});
            skLineSegment(sketch, "E384", {"start": v(87.85, 149.62) * mm, "end": v(88.5, 152.07) * mm});
            skLineSegment(sketch, "E385", {"start": v(88.5, 152.07) * mm, "end": v(89.1, 154.57) * mm});
            skLineSegment(sketch, "E386", {"start": v(89.1, 154.57) * mm, "end": v(89.4, 156.03) * mm});
            skLineSegment(sketch, "E387", {"start": v(85.93, 143.84) * mm, "end": v(86.26, 144.75) * mm});
            skLineSegment(sketch, "E388", {"start": v(86.26, 144.75) * mm, "end": v(86.46, 145.32) * mm});
            skLineSegment(sketch, "E389", {"start": v(81.25, 133.76) * mm, "end": v(82.14, 135.41) * mm});
            skLineSegment(sketch, "E390", {"start": v(82.14, 135.41) * mm, "end": v(83.3, 137.7) * mm});
            skLineSegment(sketch, "E391", {"start": v(83.3, 137.7) * mm, "end": v(84.36, 140) * mm});
            skLineSegment(sketch, "E392", {"start": v(84.36, 140) * mm, "end": v(85.35, 142.36) * mm});
            skLineSegment(sketch, "E393", {"start": v(79.66, 131.01) * mm, "end": v(80.47, 132.39) * mm});
            skLineSegment(sketch, "E394", {"start": v(73.18, 122) * mm, "end": v(73.71, 122.65) * mm});
            skLineSegment(sketch, "E395", {"start": v(73.71, 122.65) * mm, "end": v(75.3, 124.64) * mm});
            skLineSegment(sketch, "E396", {"start": v(75.3, 124.64) * mm, "end": v(76.82, 126.71) * mm});
            skLineSegment(sketch, "E397", {"start": v(76.82, 126.71) * mm, "end": v(78.26, 128.8) * mm});
            skLineSegment(sketch, "E398", {"start": v(78.26, 128.8) * mm, "end": v(78.81, 129.68) * mm});
            skLineSegment(sketch, "E399", {"start": v(71.09, 119.6) * mm, "end": v(72.08, 120.68) * mm});
            skLineSegment(sketch, "E400", {"start": v(72.08, 120.68) * mm, "end": v(72.17, 120.79) * mm});
            skLineSegment(sketch, "E401", {"start": v(63.07, 111.94) * mm, "end": v(64.87, 113.46) * mm});
            skLineSegment(sketch, "E402", {"start": v(64.87, 113.46) * mm, "end": v(66.75, 115.18) * mm});
            skLineSegment(sketch, "E403", {"start": v(66.75, 115.18) * mm, "end": v(68.6, 116.96) * mm});
            skLineSegment(sketch, "E404", {"start": v(68.6, 116.96) * mm, "end": v(70.03, 118.44) * mm});
            skLineSegment(sketch, "E405", {"start": v(60.57, 109.97) * mm, "end": v(60.9, 110.23) * mm});
            skLineSegment(sketch, "E406", {"start": v(60.9, 110.23) * mm, "end": v(61.82, 110.95) * mm});
            skLineSegment(sketch, "E407", {"start": v(51.26, 103.94) * mm, "end": v(52.4, 104.57) * mm});
            skLineSegment(sketch, "E408", {"start": v(52.4, 104.57) * mm, "end": v(54.6, 105.89) * mm});
            skLineSegment(sketch, "E409", {"start": v(54.6, 105.89) * mm, "end": v(56.76, 107.26) * mm});
            skLineSegment(sketch, "E410", {"start": v(56.76, 107.26) * mm, "end": v(58.85, 108.7) * mm});
            skLineSegment(sketch, "E411", {"start": v(58.85, 108.7) * mm, "end": v(59.3, 109.02) * mm});
            skLineSegment(sketch, "E412", {"start": v(48.44, 102.48) * mm, "end": v(49.86, 103.2) * mm});
            skLineSegment(sketch, "E413", {"start": v(38.15, 98.29) * mm, "end": v(38.4, 98.37) * mm});
            skLineSegment(sketch, "E414", {"start": v(38.4, 98.37) * mm, "end": v(40.82, 99.2) * mm});
            skLineSegment(sketch, "E415", {"start": v(40.82, 99.2) * mm, "end": v(43.21, 100.13) * mm});
            skLineSegment(sketch, "E416", {"start": v(43.21, 100.13) * mm, "end": v(45.56, 101.12) * mm});
            skLineSegment(sketch, "E417", {"start": v(45.56, 101.12) * mm, "end": v(47, 101.78) * mm});
            skLineSegment(sketch, "E418", {"start": v(35.1, 97.38) * mm, "end": v(35.97, 97.61) * mm});
            skLineSegment(sketch, "E419", {"start": v(35.97, 97.61) * mm, "end": v(36.63, 97.82) * mm});
            skLineSegment(sketch, "E420", {"start": v(24.23, 95.18) * mm, "end": v(26, 95.4) * mm});
            skLineSegment(sketch, "E421", {"start": v(26, 95.4) * mm, "end": v(28.52, 95.83) * mm});
            skLineSegment(sketch, "E422", {"start": v(28.52, 95.83) * mm, "end": v(31.02, 96.34) * mm});
            skLineSegment(sketch, "E423", {"start": v(31.02, 96.34) * mm, "end": v(33.52, 96.93) * mm});
            skLineSegment(sketch, "E424", {"start": v(33.52, 96.93) * mm, "end": v(33.58, 96.95) * mm});
            skLineSegment(sketch, "E425", {"start": v(21.07, 94.84) * mm, "end": v(22.66, 95) * mm});
            skLineSegment(sketch, "E426", {"start": v(9.98, 94.71) * mm, "end": v(10.72, 94.67) * mm});
            skLineSegment(sketch, "E427", {"start": v(10.72, 94.67) * mm, "end": v(13.28, 94.58) * mm});
            skLineSegment(sketch, "E428", {"start": v(13.28, 94.58) * mm, "end": v(15.82, 94.58) * mm});
            skLineSegment(sketch, "E429", {"start": v(15.82, 94.58) * mm, "end": v(18.38, 94.67) * mm});
            skLineSegment(sketch, "E430", {"start": v(18.38, 94.67) * mm, "end": v(19.48, 94.73) * mm});
            skLineSegment(sketch, "E431", {"start": v(6.8, 94.99) * mm, "end": v(8.18, 94.84) * mm});
            skLineSegment(sketch, "E432", {"start": v(8.18, 94.84) * mm, "end": v(8.4, 94.84) * mm});
            skLineSegment(sketch, "E433", {"start": v(-4.41, 97) * mm, "end": v(-1.92, 96.38) * mm});
            skLineSegment(sketch, "E434", {"start": v(-1.92, 96.38) * mm, "end": v(0.58, 95.87) * mm});
            skLineSegment(sketch, "E435", {"start": v(0.58, 95.87) * mm, "end": v(3.1, 95.45) * mm});
            skLineSegment(sketch, "E436", {"start": v(3.1, 95.45) * mm, "end": v(5.24, 95.15) * mm});
            skLineSegment(sketch, "E437", {"start": v(-4.41, 58.07) * mm, "end": v(-1.34, 57.58) * mm});
            skLineSegment(sketch, "E438", {"start": v(-1.34, 57.58) * mm, "end": v(1.73, 57.2) * mm});
            skLineSegment(sketch, "E439", {"start": v(1.73, 57.2) * mm, "end": v(4.8, 56.89) * mm});
            skLineSegment(sketch, "E440", {"start": v(4.8, 56.89) * mm, "end": v(7.88, 56.67) * mm});
            skLineSegment(sketch, "E441", {"start": v(7.88, 56.67) * mm, "end": v(10.97, 56.53) * mm});
            skLineSegment(sketch, "E442", {"start": v(10.97, 56.53) * mm, "end": v(14.07, 56.46) * mm});
            skLineSegment(sketch, "E443", {"start": v(14.07, 56.46) * mm, "end": v(17.16, 56.5) * mm});
            skLineSegment(sketch, "E444", {"start": v(17.16, 56.5) * mm, "end": v(20.25, 56.61) * mm});
            skLineSegment(sketch, "E445", {"start": v(20.25, 56.61) * mm, "end": v(23.34, 56.8) * mm});
            skLineSegment(sketch, "E446", {"start": v(23.34, 56.8) * mm, "end": v(26.43, 57.08) * mm});
            skLineSegment(sketch, "E447", {"start": v(26.43, 57.08) * mm, "end": v(29.5, 57.44) * mm});
            skLineSegment(sketch, "E448", {"start": v(29.5, 57.44) * mm, "end": v(32.56, 57.88) * mm});
            skLineSegment(sketch, "E449", {"start": v(32.56, 57.88) * mm, "end": v(35.61, 58.4) * mm});
            skLineSegment(sketch, "E450", {"start": v(35.61, 58.4) * mm, "end": v(38.64, 59.02) * mm});
            skLineSegment(sketch, "E451", {"start": v(38.64, 59.02) * mm, "end": v(41.67, 59.7) * mm});
            skLineSegment(sketch, "E452", {"start": v(41.67, 59.7) * mm, "end": v(44.65, 60.48) * mm});
            skLineSegment(sketch, "E453", {"start": v(44.65, 60.48) * mm, "end": v(47.64, 61.33) * mm});
            skLineSegment(sketch, "E454", {"start": v(47.64, 61.33) * mm, "end": v(50.58, 62.26) * mm});
            skLineSegment(sketch, "E455", {"start": v(50.58, 62.26) * mm, "end": v(53.5, 63.28) * mm});
            skLineSegment(sketch, "E456", {"start": v(53.5, 63.28) * mm, "end": v(56.4, 64.36) * mm});
            skLineSegment(sketch, "E457", {"start": v(56.4, 64.36) * mm, "end": v(59.26, 65.54) * mm});
            skLineSegment(sketch, "E458", {"start": v(59.26, 65.54) * mm, "end": v(62.1, 66.77) * mm});
            skLineSegment(sketch, "E459", {"start": v(62.1, 66.77) * mm, "end": v(64.89, 68.1) * mm});
            skLineSegment(sketch, "E460", {"start": v(64.89, 68.1) * mm, "end": v(67.64, 69.5) * mm});
            skLineSegment(sketch, "E461", {"start": v(67.64, 69.5) * mm, "end": v(70.37, 70.96) * mm});
            skLineSegment(sketch, "E462", {"start": v(70.37, 70.96) * mm, "end": v(73.06, 72.5) * mm});
            skLineSegment(sketch, "E463", {"start": v(73.06, 72.5) * mm, "end": v(75.68, 74.14) * mm});
            skLineSegment(sketch, "E464", {"start": v(75.68, 74.14) * mm, "end": v(78.28, 75.83) * mm});
            skLineSegment(sketch, "E465", {"start": v(78.28, 75.83) * mm, "end": v(80.82, 77.59) * mm});
            skLineSegment(sketch, "E466", {"start": v(80.82, 77.59) * mm, "end": v(83.32, 79.4) * mm});
            skLineSegment(sketch, "E467", {"start": v(83.32, 79.4) * mm, "end": v(85.78, 81.3) * mm});
            skLineSegment(sketch, "E468", {"start": v(85.78, 81.3) * mm, "end": v(88.17, 83.26) * mm});
            skLineSegment(sketch, "E469", {"start": v(88.17, 83.26) * mm, "end": v(90.52, 85.27) * mm});
            skLineSegment(sketch, "E470", {"start": v(90.52, 85.27) * mm, "end": v(92.8, 87.37) * mm});
            skLineSegment(sketch, "E471", {"start": v(92.8, 87.37) * mm, "end": v(95.03, 89.5) * mm});
            skLineSegment(sketch, "E472", {"start": v(95.03, 89.5) * mm, "end": v(97.19, 91.7) * mm});
            skLineSegment(sketch, "E473", {"start": v(97.19, 91.7) * mm, "end": v(99.3, 93.97) * mm});
            skLineSegment(sketch, "E474", {"start": v(99.3, 93.97) * mm, "end": v(101.36, 96.3) * mm});
            skLineSegment(sketch, "E475", {"start": v(101.36, 96.3) * mm, "end": v(103.35, 98.67) * mm});
            skLineSegment(sketch, "E476", {"start": v(103.35, 98.67) * mm, "end": v(105.25, 101.1) * mm});
            skLineSegment(sketch, "E477", {"start": v(105.25, 101.1) * mm, "end": v(107.11, 103.58) * mm});
            skLineSegment(sketch, "E478", {"start": v(107.11, 103.58) * mm, "end": v(108.9, 106.1) * mm});
            skLineSegment(sketch, "E479", {"start": v(108.9, 106.1) * mm, "end": v(110.6, 108.68) * mm});
            skLineSegment(sketch, "E480", {"start": v(110.6, 108.68) * mm, "end": v(112.26, 111.28) * mm});
            skLineSegment(sketch, "E481", {"start": v(112.26, 111.28) * mm, "end": v(113.82, 113.95) * mm});
            skLineSegment(sketch, "E482", {"start": v(113.82, 113.95) * mm, "end": v(115.33, 116.66) * mm});
            skLineSegment(sketch, "E483", {"start": v(115.33, 116.66) * mm, "end": v(116.77, 119.41) * mm});
            skLineSegment(sketch, "E484", {"start": v(116.77, 119.41) * mm, "end": v(118.1, 122.18) * mm});
            skLineSegment(sketch, "E485", {"start": v(118.1, 122.18) * mm, "end": v(119.4, 125) * mm});
            skLineSegment(sketch, "E486", {"start": v(119.4, 125) * mm, "end": v(120.58, 127.86) * mm});
            skLineSegment(sketch, "E487", {"start": v(120.58, 127.86) * mm, "end": v(121.7, 130.74) * mm});
            skLineSegment(sketch, "E488", {"start": v(121.7, 130.74) * mm, "end": v(122.76, 133.66) * mm});
            skLineSegment(sketch, "E489", {"start": v(122.76, 133.66) * mm, "end": v(123.7, 136.6) * mm});
            skLineSegment(sketch, "E490", {"start": v(123.7, 136.6) * mm, "end": v(124.6, 139.56) * mm});
            skLineSegment(sketch, "E491", {"start": v(124.6, 139.56) * mm, "end": v(125.4, 142.55) * mm});
            skLineSegment(sketch, "E492", {"start": v(125.4, 142.55) * mm, "end": v(126.12, 145.55) * mm});
            skLineSegment(sketch, "E493", {"start": v(126.12, 145.55) * mm, "end": v(126.78, 148.58) * mm});
            skLineSegment(sketch, "E494", {"start": v(126.78, 148.58) * mm, "end": v(127.33, 151.63) * mm});
            skLineSegment(sketch, "E495", {"start": v(127.33, 151.63) * mm, "end": v(127.81, 154.68) * mm});
            skLineSegment(sketch, "E496", {"start": v(127.81, 154.68) * mm, "end": v(128.2, 157.74) * mm});
            skLineSegment(sketch, "E497", {"start": v(128.2, 157.74) * mm, "end": v(128.51, 160.83) * mm});
            skLineSegment(sketch, "E498", {"start": v(128.51, 160.83) * mm, "end": v(128.75, 163.9) * mm});
            skLineSegment(sketch, "E499", {"start": v(128.75, 163.9) * mm, "end": v(128.87, 167) * mm});
            skLineSegment(sketch, "E500", {"start": v(128.87, 167) * mm, "end": v(128.94, 170.1) * mm});
            skLineSegment(sketch, "E501", {"start": v(128.94, 170.1) * mm, "end": v(128.92, 173.2) * mm});
            skLineSegment(sketch, "E502", {"start": v(128.92, 173.2) * mm, "end": v(128.8, 176.29) * mm});
            skLineSegment(sketch, "E503", {"start": v(128.8, 176.29) * mm, "end": v(128.62, 179.38) * mm});
            skLineSegment(sketch, "E504", {"start": v(128.62, 179.38) * mm, "end": v(128.34, 182.45) * mm});
            skLineSegment(sketch, "E505", {"start": v(128.34, 182.45) * mm, "end": v(127.98, 185.52) * mm});
            skLineSegment(sketch, "E506", {"start": v(127.98, 185.52) * mm, "end": v(127.54, 188.58) * mm});
            skLineSegment(sketch, "E507", {"start": v(127.54, 188.58) * mm, "end": v(127.03, 191.63) * mm});
            skLineSegment(sketch, "E508", {"start": v(127.03, 191.63) * mm, "end": v(126.42, 194.68) * mm});
            skLineSegment(sketch, "E509", {"start": v(126.42, 194.68) * mm, "end": v(125.72, 197.69) * mm});
            skLineSegment(sketch, "E510", {"start": v(125.72, 197.69) * mm, "end": v(124.96, 200.7) * mm});
            skLineSegment(sketch, "E511", {"start": v(124.96, 200.7) * mm, "end": v(124.11, 203.66) * mm});
            skLineSegment(sketch, "E512", {"start": v(124.11, 203.66) * mm, "end": v(123.18, 206.62) * mm});
            skLineSegment(sketch, "E513", {"start": v(123.18, 206.62) * mm, "end": v(122.16, 209.54) * mm});
            skLineSegment(sketch, "E514", {"start": v(122.16, 209.54) * mm, "end": v(121.08, 212.44) * mm});
            skLineSegment(sketch, "E515", {"start": v(121.08, 212.44) * mm, "end": v(119.92, 215.3) * mm});
            skLineSegment(sketch, "E516", {"start": v(119.92, 215.3) * mm, "end": v(118.67, 218.13) * mm});
            skLineSegment(sketch, "E517", {"start": v(118.67, 218.13) * mm, "end": v(117.36, 220.93) * mm});
            skLineSegment(sketch, "E518", {"start": v(117.36, 220.93) * mm, "end": v(115.96, 223.68) * mm});
            skLineSegment(sketch, "E519", {"start": v(115.96, 223.68) * mm, "end": v(114.48, 226.4) * mm});
            skLineSegment(sketch, "E520", {"start": v(114.48, 226.4) * mm, "end": v(112.93, 229.1) * mm});
            skLineSegment(sketch, "E521", {"start": v(112.93, 229.1) * mm, "end": v(111.33, 231.72) * mm});
            skLineSegment(sketch, "E522", {"start": v(111.33, 231.72) * mm, "end": v(109.63, 234.33) * mm});
            skLineSegment(sketch, "E523", {"start": v(109.63, 234.33) * mm, "end": v(107.9, 236.87) * mm});
            skLineSegment(sketch, "E524", {"start": v(107.9, 236.87) * mm, "end": v(106.06, 239.36) * mm});
            skLineSegment(sketch, "E525", {"start": v(106.06, 239.36) * mm, "end": v(104.17, 241.82) * mm});
            skLineSegment(sketch, "E526", {"start": v(104.17, 241.82) * mm, "end": v(102.22, 244.21) * mm});
            skLineSegment(sketch, "E527", {"start": v(102.22, 244.21) * mm, "end": v(100.2, 246.56) * mm});
            skLineSegment(sketch, "E528", {"start": v(100.2, 246.56) * mm, "end": v(98.12, 248.85) * mm});
            skLineSegment(sketch, "E529", {"start": v(98.12, 248.85) * mm, "end": v(95.98, 251.09) * mm});
            skLineSegment(sketch, "E530", {"start": v(95.98, 251.09) * mm, "end": v(93.76, 253.25) * mm});
            skLineSegment(sketch, "E531", {"start": v(93.76, 253.25) * mm, "end": v(91.51, 255.37) * mm});
            skLineSegment(sketch, "E532", {"start": v(91.51, 255.37) * mm, "end": v(89.19, 257.42) * mm});
            skLineSegment(sketch, "E533", {"start": v(89.19, 257.42) * mm, "end": v(86.82, 259.4) * mm});
            skLineSegment(sketch, "E534", {"start": v(86.82, 259.4) * mm, "end": v(84.38, 261.31) * mm});
            skLineSegment(sketch, "E535", {"start": v(84.38, 261.31) * mm, "end": v(81.9, 263.18) * mm});
            skLineSegment(sketch, "E536", {"start": v(81.9, 263.18) * mm, "end": v(79.39, 264.95) * mm});
            skLineSegment(sketch, "E537", {"start": v(79.39, 264.95) * mm, "end": v(76.82, 266.67) * mm});
            skLineSegment(sketch, "E538", {"start": v(76.82, 266.67) * mm, "end": v(74.2, 268.32) * mm});
            skLineSegment(sketch, "E539", {"start": v(74.2, 268.32) * mm, "end": v(71.53, 269.9) * mm});
            skLineSegment(sketch, "E540", {"start": v(71.53, 269.9) * mm, "end": v(68.82, 271.4) * mm});
            skLineSegment(sketch, "E541", {"start": v(68.82, 271.4) * mm, "end": v(66.1, 272.83) * mm});
            skLineSegment(sketch, "E542", {"start": v(66.1, 272.83) * mm, "end": v(63.3, 274.18) * mm});
            skLineSegment(sketch, "E543", {"start": v(63.3, 274.18) * mm, "end": v(60.48, 275.47) * mm});
            skLineSegment(sketch, "E544", {"start": v(60.48, 275.47) * mm, "end": v(57.65, 276.68) * mm});
            skLineSegment(sketch, "E545", {"start": v(57.65, 276.68) * mm, "end": v(54.75, 277.8) * mm});
            skLineSegment(sketch, "E546", {"start": v(54.75, 277.8) * mm, "end": v(51.85, 278.84) * mm});
            skLineSegment(sketch, "E547", {"start": v(51.85, 278.84) * mm, "end": v(48.9, 279.81) * mm});
            skLineSegment(sketch, "E548", {"start": v(48.9, 279.81) * mm, "end": v(45.94, 280.7) * mm});
            skLineSegment(sketch, "E549", {"start": v(45.94, 280.7) * mm, "end": v(42.96, 281.5) * mm});
            skLineSegment(sketch, "E550", {"start": v(42.96, 281.5) * mm, "end": v(39.95, 282.23) * mm});
            skLineSegment(sketch, "E551", {"start": v(39.95, 282.23) * mm, "end": v(36.93, 282.88) * mm});
            skLineSegment(sketch, "E552", {"start": v(36.93, 282.88) * mm, "end": v(33.88, 283.43) * mm});
            skLineSegment(sketch, "E553", {"start": v(33.88, 283.43) * mm, "end": v(30.83, 283.92) * mm});
            skLineSegment(sketch, "E554", {"start": v(30.83, 283.92) * mm, "end": v(27.76, 284.32) * mm});
            skLineSegment(sketch, "E555", {"start": v(27.76, 284.32) * mm, "end": v(24.67, 284.62) * mm});
            skLineSegment(sketch, "E556", {"start": v(24.67, 284.62) * mm, "end": v(21.6, 284.85) * mm});
            skLineSegment(sketch, "E557", {"start": v(21.6, 284.85) * mm, "end": v(18.51, 285) * mm});
            skLineSegment(sketch, "E558", {"start": v(18.51, 285) * mm, "end": v(15.4, 285.06) * mm});
            skLineSegment(sketch, "E559", {"start": v(15.4, 285.06) * mm, "end": v(12.3, 285.04) * mm});
            skLineSegment(sketch, "E560", {"start": v(12.3, 285.04) * mm, "end": v(9.22, 284.94) * mm});
            skLineSegment(sketch, "E561", {"start": v(9.22, 284.94) * mm, "end": v(6.13, 284.74) * mm});
            skLineSegment(sketch, "E562", {"start": v(6.13, 284.74) * mm, "end": v(3.06, 284.47) * mm});
            skLineSegment(sketch, "E563", {"start": v(3.06, 284.47) * mm, "end": v(-0.03, 284.13) * mm});
            skLineSegment(sketch, "E564", {"start": v(-0.03, 284.13) * mm, "end": v(-3.08, 283.69) * mm});
            skLineSegment(sketch, "E565", {"start": v(-3.08, 283.69) * mm, "end": v(-6.13, 283.16) * mm});
            skLineSegment(sketch, "E566", {"start": v(-6.13, 283.16) * mm, "end": v(-9.18, 282.56) * mm});
            skLineSegment(sketch, "E567", {"start": v(-9.18, 282.56) * mm, "end": v(-12.18, 281.87) * mm});
            skLineSegment(sketch, "E568", {"start": v(-12.18, 281.87) * mm, "end": v(-15.19, 281.1) * mm});
            skLineSegment(sketch, "E569", {"start": v(-15.19, 281.1) * mm, "end": v(-18.15, 280.26) * mm});
            skLineSegment(sketch, "E570", {"start": v(-18.15, 280.26) * mm, "end": v(-21.11, 279.33) * mm});
            skLineSegment(sketch, "E571", {"start": v(-21.11, 279.33) * mm, "end": v(-24.03, 278.33) * mm});
            skLineSegment(sketch, "E572", {"start": v(-24.03, 278.33) * mm, "end": v(-26.93, 277.23) * mm});
            skLineSegment(sketch, "E573", {"start": v(-26.93, 277.23) * mm, "end": v(-29.8, 276.07) * mm});
            skLineSegment(sketch, "E574", {"start": v(-29.8, 276.07) * mm, "end": v(-32.63, 274.84) * mm});
            skLineSegment(sketch, "E575", {"start": v(-32.63, 274.84) * mm, "end": v(-35.42, 273.5) * mm});
            skLineSegment(sketch, "E576", {"start": v(-35.42, 273.5) * mm, "end": v(-38.2, 272.13) * mm});
            skLineSegment(sketch, "E577", {"start": v(-38.2, 272.13) * mm, "end": v(-40.93, 270.65) * mm});
            skLineSegment(sketch, "E578", {"start": v(-40.93, 270.65) * mm, "end": v(-43.6, 269.1) * mm});
            skLineSegment(sketch, "E579", {"start": v(-43.6, 269.1) * mm, "end": v(-46.24, 267.5) * mm});
            skLineSegment(sketch, "E580", {"start": v(-46.24, 267.5) * mm, "end": v(-48.84, 265.82) * mm});
            skLineSegment(sketch, "E581", {"start": v(-48.84, 265.82) * mm, "end": v(-51.38, 264.06) * mm});
            skLineSegment(sketch, "E582", {"start": v(-51.38, 264.06) * mm, "end": v(-53.88, 262.24) * mm});
            skLineSegment(sketch, "E583", {"start": v(-53.88, 262.24) * mm, "end": v(-56.34, 260.36) * mm});
            skLineSegment(sketch, "E584", {"start": v(-56.34, 260.36) * mm, "end": v(-58.73, 258.4) * mm});
            skLineSegment(sketch, "E585", {"start": v(-58.73, 258.4) * mm, "end": v(-61.08, 256.38) * mm});
            skLineSegment(sketch, "E586", {"start": v(-61.08, 256.38) * mm, "end": v(-63.36, 254.3) * mm});
            skLineSegment(sketch, "E587", {"start": v(-63.36, 254.3) * mm, "end": v(-65.6, 252.17) * mm});
            skLineSegment(sketch, "E588", {"start": v(-65.6, 252.17) * mm, "end": v(-4.41, 164.75) * mm});
            skLineSegment(sketch, "E589", {"start": v(-54.22, 241.08) * mm, "end": v(-54.32, 240.97) * mm});
            skLineSegment(sketch, "E590", {"start": v(-54.32, 240.97) * mm, "end": v(-56.36, 238.94) * mm});
            skLineSegment(sketch, "E591", {"start": v(-50.75, 244.32) * mm, "end": v(-52.25, 242.96) * mm});
            skLineSegment(sketch, "E592", {"start": v(-52.25, 242.96) * mm, "end": v(-53.08, 242.18) * mm});
            skLineSegment(sketch, "E593", {"start": v(-47.1, 247.4) * mm, "end": v(-47.93, 246.75) * mm});
            skLineSegment(sketch, "E594", {"start": v(-47.93, 246.75) * mm, "end": v(-49.54, 245.37) * mm});
            skLineSegment(sketch, "E595", {"start": v(-43.34, 250.3) * mm, "end": v(-43.4, 250.26) * mm});
            skLineSegment(sketch, "E596", {"start": v(-43.4, 250.26) * mm, "end": v(-45.69, 248.53) * mm});
            skLineSegment(sketch, "E597", {"start": v(-45.69, 248.53) * mm, "end": v(-45.86, 248.38) * mm});
            skLineSegment(sketch, "E598", {"start": v(-39.4, 253.02) * mm, "end": v(-41.05, 251.92) * mm});
            skLineSegment(sketch, "E599", {"start": v(-41.05, 251.92) * mm, "end": v(-42.03, 251.22) * mm});
            skLineSegment(sketch, "E600", {"start": v(-35.38, 255.53) * mm, "end": v(-36.23, 255.03) * mm});
            skLineSegment(sketch, "E601", {"start": v(-36.23, 255.03) * mm, "end": v(-38.07, 253.86) * mm});
            skLineSegment(sketch, "E602", {"start": v(-31.21, 257.86) * mm, "end": v(-31.23, 257.84) * mm});
            skLineSegment(sketch, "E603", {"start": v(-31.23, 257.84) * mm, "end": v(-33.75, 256.47) * mm});
            skLineSegment(sketch, "E604", {"start": v(-33.75, 256.47) * mm, "end": v(-34, 256.32) * mm});
            skLineSegment(sketch, "E605", {"start": v(-26.96, 259.96) * mm, "end": v(-28.67, 259.15) * mm});
            skLineSegment(sketch, "E606", {"start": v(-28.67, 259.15) * mm, "end": v(-29.8, 258.58) * mm});
            skLineSegment(sketch, "E607", {"start": v(-22.57, 261.86) * mm, "end": v(-23.44, 261.52) * mm});
            skLineSegment(sketch, "E608", {"start": v(-23.44, 261.52) * mm, "end": v(-25.5, 260.61) * mm});
            skLineSegment(sketch, "E609", {"start": v(-18.13, 263.58) * mm, "end": v(-20.78, 262.6) * mm});
            skLineSegment(sketch, "E610", {"start": v(-20.78, 262.6) * mm, "end": v(-21.11, 262.46) * mm});
            skLineSegment(sketch, "E611", {"start": v(-13.6, 265.04) * mm, "end": v(-15.36, 264.5) * mm});
            skLineSegment(sketch, "E612", {"start": v(-15.36, 264.5) * mm, "end": v(-16.63, 264.09) * mm});
            skLineSegment(sketch, "E613", {"start": v(-9, 266.29) * mm, "end": v(-9.85, 266.1) * mm});
            skLineSegment(sketch, "E614", {"start": v(-9.85, 266.1) * mm, "end": v(-12.08, 265.48) * mm});
            skLineSegment(sketch, "E615", {"start": v(-4.37, 267.35) * mm, "end": v(-7.06, 266.77) * mm});
            skLineSegment(sketch, "E616", {"start": v(-7.06, 266.77) * mm, "end": v(-7.46, 266.67) * mm});
            skLineSegment(sketch, "E617", {"start": v(0.33, 268.13) * mm, "end": v(-1.4, 267.87) * mm});
            skLineSegment(sketch, "E618", {"start": v(-1.4, 267.87) * mm, "end": v(-2.8, 267.62) * mm});
            skLineSegment(sketch, "E619", {"start": v(5.05, 268.72) * mm, "end": v(4.27, 268.64) * mm});
            skLineSegment(sketch, "E620", {"start": v(4.27, 268.64) * mm, "end": v(1.9, 268.36) * mm});
            skLineSegment(sketch, "E621", {"start": v(9.81, 269.06) * mm, "end": v(7.12, 268.91) * mm});
            skLineSegment(sketch, "E622", {"start": v(7.12, 268.91) * mm, "end": v(6.64, 268.85) * mm});
            skLineSegment(sketch, "E623", {"start": v(14.57, 269.19) * mm, "end": v(12.86, 269.17) * mm});
            skLineSegment(sketch, "E624", {"start": v(12.86, 269.17) * mm, "end": v(11.4, 269.12) * mm});
            skLineSegment(sketch, "E625", {"start": v(19.34, 269.08) * mm, "end": v(18.62, 269.1) * mm});
            skLineSegment(sketch, "E626", {"start": v(18.62, 269.1) * mm, "end": v(16.16, 269.17) * mm});
            skLineSegment(sketch, "E627", {"start": v(24.08, 268.74) * mm, "end": v(21.47, 268.95) * mm});
            skLineSegment(sketch, "E628", {"start": v(21.47, 268.95) * mm, "end": v(20.9, 268.98) * mm});
            skLineSegment(sketch, "E629", {"start": v(28.8, 268.15) * mm, "end": v(27.19, 268.38) * mm});
            skLineSegment(sketch, "E630", {"start": v(27.19, 268.38) * mm, "end": v(25.64, 268.57) * mm});
            skLineSegment(sketch, "E631", {"start": v(33.5, 267.37) * mm, "end": v(32.86, 267.5) * mm});
            skLineSegment(sketch, "E632", {"start": v(32.86, 267.5) * mm, "end": v(30.36, 267.92) * mm});
            skLineSegment(sketch, "E633", {"start": v(38.15, 266.33) * mm, "end": v(35.68, 266.92) * mm});
            skLineSegment(sketch, "E634", {"start": v(35.68, 266.92) * mm, "end": v(35.06, 267.05) * mm});
            skLineSegment(sketch, "E635", {"start": v(42.75, 265.08) * mm, "end": v(41.24, 265.53) * mm});
            skLineSegment(sketch, "E636", {"start": v(41.24, 265.53) * mm, "end": v(39.68, 265.95) * mm});
            skLineSegment(sketch, "E637", {"start": v(47.28, 263.62) * mm, "end": v(46.73, 263.81) * mm});
            skLineSegment(sketch, "E638", {"start": v(46.73, 263.81) * mm, "end": v(44.27, 264.64) * mm});
            skLineSegment(sketch, "E639", {"start": v(51.72, 261.93) * mm, "end": v(49.41, 262.84) * mm});
            skLineSegment(sketch, "E640", {"start": v(49.41, 262.84) * mm, "end": v(48.76, 263.07) * mm});
            skLineSegment(sketch, "E641", {"start": v(56.08, 260.02) * mm, "end": v(54.73, 260.66) * mm});
            skLineSegment(sketch, "E642", {"start": v(54.73, 260.66) * mm, "end": v(53.18, 261.31) * mm});
            skLineSegment(sketch, "E643", {"start": v(60.36, 257.93) * mm, "end": v(59.91, 258.16) * mm});
            skLineSegment(sketch, "E644", {"start": v(59.91, 258.16) * mm, "end": v(57.52, 259.34) * mm});
            skLineSegment(sketch, "E645", {"start": v(64.53, 255.62) * mm, "end": v(62.43, 256.8) * mm});
            skLineSegment(sketch, "E646", {"start": v(62.43, 256.8) * mm, "end": v(61.75, 257.16) * mm});
            skLineSegment(sketch, "E647", {"start": v(68.57, 253.1) * mm, "end": v(67.36, 253.88) * mm});
            skLineSegment(sketch, "E648", {"start": v(67.36, 253.88) * mm, "end": v(65.88, 254.8) * mm});
            skLineSegment(sketch, "E649", {"start": v(72.49, 250.4) * mm, "end": v(72.13, 250.67) * mm});
            skLineSegment(sketch, "E650", {"start": v(72.13, 250.67) * mm, "end": v(69.88, 252.21) * mm});
            skLineSegment(sketch, "E651", {"start": v(76.27, 247.5) * mm, "end": v(74.43, 248.95) * mm});
            skLineSegment(sketch, "E652", {"start": v(74.43, 248.95) * mm, "end": v(73.76, 249.44) * mm});
            skLineSegment(sketch, "E653", {"start": v(79.91, 244.42) * mm, "end": v(78.88, 245.33) * mm});
            skLineSegment(sketch, "E654", {"start": v(78.88, 245.33) * mm, "end": v(77.5, 246.5) * mm});
            skLineSegment(sketch, "E655", {"start": v(83.4, 241.18) * mm, "end": v(83.13, 241.46) * mm});
            skLineSegment(sketch, "E656", {"start": v(83.13, 241.46) * mm, "end": v(81.1, 243.36) * mm});
            skLineSegment(sketch, "E657", {"start": v(86.73, 237.78) * mm, "end": v(85.16, 239.43) * mm});
            skLineSegment(sketch, "E658", {"start": v(85.16, 239.43) * mm, "end": v(84.53, 240.06) * mm});
            skLineSegment(sketch, "E659", {"start": v(89.88, 234.22) * mm, "end": v(89.04, 235.21) * mm});
            skLineSegment(sketch, "E660", {"start": v(89.04, 235.21) * mm, "end": v(87.79, 236.61) * mm});
            skLineSegment(sketch, "E661", {"start": v(92.87, 230.5) * mm, "end": v(92.68, 230.75) * mm});
            skLineSegment(sketch, "E662", {"start": v(92.68, 230.75) * mm, "end": v(90.9, 233) * mm});
            skLineSegment(sketch, "E663", {"start": v(95.66, 226.64) * mm, "end": v(94.4, 228.46) * mm});
            skLineSegment(sketch, "E664", {"start": v(94.4, 228.46) * mm, "end": v(93.82, 229.22) * mm});
            skLineSegment(sketch, "E665", {"start": v(98.27, 222.66) * mm, "end": v(97.61, 223.7) * mm});
            skLineSegment(sketch, "E666", {"start": v(97.61, 223.7) * mm, "end": v(96.55, 225.33) * mm});
            skLineSegment(sketch, "E667", {"start": v(100.68, 218.56) * mm, "end": v(100.55, 218.79) * mm});
            skLineSegment(sketch, "E668", {"start": v(100.55, 218.79) * mm, "end": v(99.13, 221.27) * mm});
            skLineSegment(sketch, "E669", {"start": v(99.13, 221.27) * mm, "end": v(99.1, 221.3) * mm});
            skLineSegment(sketch, "E670", {"start": v(102.88, 214.34) * mm, "end": v(101.93, 216.25) * mm});
            skLineSegment(sketch, "E671", {"start": v(101.93, 216.25) * mm, "end": v(101.44, 217.16) * mm});
            skLineSegment(sketch, "E672", {"start": v(104.9, 210.03) * mm, "end": v(104.43, 211.08) * mm});
            skLineSegment(sketch, "E673", {"start": v(104.43, 211.08) * mm, "end": v(103.58, 212.9) * mm});
            skLineSegment(sketch, "E674", {"start": v(106.7, 205.6) * mm, "end": v(106.63, 205.8) * mm});
            skLineSegment(sketch, "E675", {"start": v(106.63, 205.8) * mm, "end": v(105.57, 208.46) * mm});
            skLineSegment(sketch, "E676", {"start": v(105.57, 208.46) * mm, "end": v(105.53, 208.57) * mm});
            skLineSegment(sketch, "E677", {"start": v(108.26, 201.12) * mm, "end": v(107.6, 203.08) * mm});
            skLineSegment(sketch, "E678", {"start": v(107.6, 203.08) * mm, "end": v(107.24, 204.12) * mm});
            skLineSegment(sketch, "E679", {"start": v(109.61, 196.54) * mm, "end": v(109.34, 197.62) * mm});
            skLineSegment(sketch, "E680", {"start": v(109.34, 197.62) * mm, "end": v(108.74, 199.61) * mm});
            skLineSegment(sketch, "E681", {"start": v(110.78, 191.93) * mm, "end": v(110.73, 192.06) * mm});
            skLineSegment(sketch, "E682", {"start": v(110.73, 192.06) * mm, "end": v(110.08, 194.85) * mm});
            skLineSegment(sketch, "E683", {"start": v(110.08, 194.85) * mm, "end": v(110.03, 195.02) * mm});
            skLineSegment(sketch, "E684", {"start": v(111.66, 187.25) * mm, "end": v(111.33, 189.24) * mm});
            skLineSegment(sketch, "E685", {"start": v(111.33, 189.24) * mm, "end": v(111.1, 190.38) * mm});
            skLineSegment(sketch, "E686", {"start": v(112.36, 182.55) * mm, "end": v(112.24, 183.57) * mm});
            skLineSegment(sketch, "E687", {"start": v(112.24, 183.57) * mm, "end": v(111.92, 185.68) * mm});
            skLineSegment(sketch, "E688", {"start": v(112.8, 177.81) * mm, "end": v(112.8, 177.85) * mm});
            skLineSegment(sketch, "E689", {"start": v(112.8, 177.85) * mm, "end": v(112.57, 180.71) * mm});
            skLineSegment(sketch, "E690", {"start": v(112.57, 180.71) * mm, "end": v(112.53, 180.96) * mm});
            skLineSegment(sketch, "E691", {"start": v(113.04, 173.05) * mm, "end": v(112.98, 175) * mm});
            skLineSegment(sketch, "E692", {"start": v(112.98, 175) * mm, "end": v(112.91, 176.22) * mm});
            skLineSegment(sketch, "E693", {"start": v(113.02, 168.29) * mm, "end": v(113.06, 169.24) * mm});
            skLineSegment(sketch, "E694", {"start": v(113.06, 169.24) * mm, "end": v(113.06, 171.46) * mm});
            skLineSegment(sketch, "E695", {"start": v(112.8, 163.52) * mm, "end": v(112.98, 166.38) * mm});
            skLineSegment(sketch, "E696", {"start": v(112.98, 166.38) * mm, "end": v(112.98, 166.7) * mm});
            skLineSegment(sketch, "E697", {"start": v(112.32, 158.78) * mm, "end": v(112.55, 160.64) * mm});
            skLineSegment(sketch, "E698", {"start": v(112.55, 160.64) * mm, "end": v(112.66, 161.94) * mm});
            skLineSegment(sketch, "E699", {"start": v(111.64, 154.08) * mm, "end": v(111.8, 154.97) * mm});
            skLineSegment(sketch, "E700", {"start": v(111.8, 154.97) * mm, "end": v(112.13, 157.22) * mm});
            skLineSegment(sketch, "E701", {"start": v(110.71, 149.4) * mm, "end": v(111.28, 152.14) * mm});
            skLineSegment(sketch, "E702", {"start": v(111.28, 152.14) * mm, "end": v(111.35, 152.52) * mm});
            skLineSegment(sketch, "E703", {"start": v(109.57, 144.8) * mm, "end": v(110.03, 146.53) * mm});
            skLineSegment(sketch, "E704", {"start": v(110.03, 146.53) * mm, "end": v(110.35, 147.86) * mm});
            skLineSegment(sketch, "E705", {"start": v(108.2, 140.22) * mm, "end": v(108.47, 141) * mm});
            skLineSegment(sketch, "E706", {"start": v(108.47, 141) * mm, "end": v(109.15, 143.25) * mm});
            skLineSegment(sketch, "E707", {"start": v(106.63, 135.73) * mm, "end": v(107.56, 138.3) * mm});
            skLineSegment(sketch, "E708", {"start": v(107.56, 138.3) * mm, "end": v(107.7, 138.72) * mm});
            skLineSegment(sketch, "E709", {"start": v(104.8, 131.33) * mm, "end": v(105.5, 132.92) * mm});
            skLineSegment(sketch, "E710", {"start": v(105.5, 132.92) * mm, "end": v(106.03, 134.25) * mm});
            skLineSegment(sketch, "E711", {"start": v(102.8, 127.01) * mm, "end": v(103.13, 127.69) * mm});
            skLineSegment(sketch, "E712", {"start": v(103.13, 127.69) * mm, "end": v(104.17, 129.87) * mm});
            skLineSegment(sketch, "E713", {"start": v(100.6, 122.8) * mm, "end": v(101.84, 125.13) * mm});
            skLineSegment(sketch, "E714", {"start": v(101.84, 125.13) * mm, "end": v(102.08, 125.6) * mm});
            skLineSegment(sketch, "E715", {"start": v(98.16, 118.7) * mm, "end": v(99.05, 120.13) * mm});
            skLineSegment(sketch, "E716", {"start": v(99.05, 120.13) * mm, "end": v(99.8, 121.42) * mm});
            skLineSegment(sketch, "E717", {"start": v(95.54, 114.71) * mm, "end": v(95.94, 115.28) * mm});
            skLineSegment(sketch, "E718", {"start": v(95.94, 115.28) * mm, "end": v(97.31, 117.36) * mm});
            skLineSegment(sketch, "E719", {"start": v(92.74, 110.86) * mm, "end": v(94.29, 112.93) * mm});
            skLineSegment(sketch, "E720", {"start": v(94.29, 112.93) * mm, "end": v(94.63, 113.42) * mm});
            skLineSegment(sketch, "E721", {"start": v(89.76, 107.16) * mm, "end": v(90.8, 108.4) * mm});
            skLineSegment(sketch, "E722", {"start": v(90.8, 108.4) * mm, "end": v(91.77, 109.61) * mm});
            skLineSegment(sketch, "E723", {"start": v(86.58, 103.6) * mm, "end": v(87.03, 104.07) * mm});
            skLineSegment(sketch, "E724", {"start": v(87.03, 104.07) * mm, "end": v(88.72, 105.95) * mm});
            skLineSegment(sketch, "E725", {"start": v(83.26, 100.2) * mm, "end": v(85.04, 101.97) * mm});
            skLineSegment(sketch, "E726", {"start": v(85.04, 101.97) * mm, "end": v(85.48, 102.46) * mm});
            skLineSegment(sketch, "E727", {"start": v(79.77, 96.98) * mm, "end": v(80.9, 98) * mm});
            skLineSegment(sketch, "E728", {"start": v(80.9, 98) * mm, "end": v(82.1, 99.11) * mm});
            skLineSegment(sketch, "E729", {"start": v(76.1, 93.9) * mm, "end": v(76.55, 94.24) * mm});
            skLineSegment(sketch, "E730", {"start": v(76.55, 94.24) * mm, "end": v(78.56, 95.92) * mm});
            skLineSegment(sketch, "E731", {"start": v(72.32, 91.03) * mm, "end": v(74.3, 92.49) * mm});
            skLineSegment(sketch, "E732", {"start": v(74.3, 92.49) * mm, "end": v(74.86, 92.93) * mm});
            skLineSegment(sketch, "E733", {"start": v(68.4, 88.32) * mm, "end": v(69.63, 89.14) * mm});
            skLineSegment(sketch, "E734", {"start": v(69.63, 89.14) * mm, "end": v(71.02, 90.1) * mm});
            skLineSegment(sketch, "E735", {"start": v(64.36, 85.82) * mm, "end": v(64.78, 86.07) * mm});
            skLineSegment(sketch, "E736", {"start": v(64.78, 86.07) * mm, "end": v(67.07, 87.47) * mm});
            skLineSegment(sketch, "E737", {"start": v(60.19, 83.51) * mm, "end": v(62.28, 84.63) * mm});
            skLineSegment(sketch, "E738", {"start": v(62.28, 84.63) * mm, "end": v(62.96, 85.04) * mm});
            skLineSegment(sketch, "E739", {"start": v(55.91, 81.42) * mm, "end": v(57.18, 82.01) * mm});
            skLineSegment(sketch, "E740", {"start": v(57.18, 82.01) * mm, "end": v(58.77, 82.8) * mm});
            skLineSegment(sketch, "E741", {"start": v(51.53, 79.51) * mm, "end": v(51.93, 79.68) * mm});
            skLineSegment(sketch, "E742", {"start": v(51.93, 79.68) * mm, "end": v(54.47, 80.76) * mm});
            skLineSegment(sketch, "E743", {"start": v(47.09, 77.84) * mm, "end": v(49.27, 78.62) * mm});
            skLineSegment(sketch, "E744", {"start": v(49.27, 78.62) * mm, "end": v(50.07, 78.94) * mm});
            skLineSegment(sketch, "E745", {"start": v(42.56, 76.38) * mm, "end": v(43.83, 76.76) * mm});
            skLineSegment(sketch, "E746", {"start": v(43.83, 76.76) * mm, "end": v(45.58, 77.33) * mm});
            skLineSegment(sketch, "E747", {"start": v(37.94, 75.15) * mm, "end": v(38.3, 75.24) * mm});
            skLineSegment(sketch, "E748", {"start": v(38.3, 75.24) * mm, "end": v(41.03, 75.94) * mm});
            skLineSegment(sketch, "E749", {"start": v(33.3, 74.14) * mm, "end": v(35.5, 74.58) * mm});
            skLineSegment(sketch, "E750", {"start": v(35.5, 74.58) * mm, "end": v(36.4, 74.8) * mm});
            skLineSegment(sketch, "E751", {"start": v(28.6, 73.35) * mm, "end": v(29.86, 73.52) * mm});
            skLineSegment(sketch, "E752", {"start": v(29.86, 73.52) * mm, "end": v(31.74, 73.84) * mm});
            skLineSegment(sketch, "E753", {"start": v(23.87, 72.78) * mm, "end": v(24.16, 72.8) * mm});
            skLineSegment(sketch, "E754", {"start": v(24.16, 72.8) * mm, "end": v(27.02, 73.12) * mm});
            skLineSegment(sketch, "E755", {"start": v(19.12, 72.44) * mm, "end": v(21.3, 72.57) * mm});
            skLineSegment(sketch, "E756", {"start": v(21.3, 72.57) * mm, "end": v(22.3, 72.65) * mm});
            skLineSegment(sketch, "E757", {"start": v(14.36, 72.36) * mm, "end": v(15.57, 72.34) * mm});
            skLineSegment(sketch, "E758", {"start": v(15.57, 72.34) * mm, "end": v(17.54, 72.4) * mm});
            skLineSegment(sketch, "E759", {"start": v(9.6, 72.46) * mm, "end": v(9.83, 72.46) * mm});
            skLineSegment(sketch, "E760", {"start": v(9.83, 72.46) * mm, "end": v(12.69, 72.36) * mm});
            skLineSegment(sketch, "E761", {"start": v(12.69, 72.36) * mm, "end": v(12.77, 72.36) * mm});
            skLineSegment(sketch, "E762", {"start": v(4.86, 72.85) * mm, "end": v(6.97, 72.63) * mm});
            skLineSegment(sketch, "E763", {"start": v(6.97, 72.63) * mm, "end": v(8.01, 72.57) * mm});
            skLineSegment(sketch, "E764", {"start": v(0.14, 73.44) * mm, "end": v(1.26, 73.25) * mm});
            skLineSegment(sketch, "E765", {"start": v(1.26, 73.25) * mm, "end": v(3.27, 73.01) * mm});
            skLineSegment(sketch, "E766", {"start": v(-4.41, 74.2) * mm, "end": v(-1.58, 73.7) * mm});
            skLineSegment(sketch, "E767", {"start": v(-1.58, 73.7) * mm, "end": v(-1.45, 73.67) * mm});
            skLineSegment(sketch, "E768", {"start": v(14.64, 158.06) * mm, "end": v(15.7, 158.1) * mm});
            skLineSegment(sketch, "E769", {"start": v(15.7, 158.1) * mm, "end": v(16.73, 158.23) * mm});
            skLineSegment(sketch, "E770", {"start": v(16.73, 158.23) * mm, "end": v(17.77, 158.46) * mm});
            skLineSegment(sketch, "E771", {"start": v(17.77, 158.46) * mm, "end": v(18.76, 158.76) * mm});
            skLineSegment(sketch, "E772", {"start": v(18.76, 158.76) * mm, "end": v(19.74, 159.14) * mm});
            skLineSegment(sketch, "E773", {"start": v(19.74, 159.14) * mm, "end": v(20.7, 159.6) * mm});
            skLineSegment(sketch, "E774", {"start": v(20.7, 159.6) * mm, "end": v(21.6, 160.14) * mm});
            skLineSegment(sketch, "E775", {"start": v(21.6, 160.14) * mm, "end": v(22.45, 160.75) * mm});
            skLineSegment(sketch, "E776", {"start": v(22.45, 160.75) * mm, "end": v(23.25, 161.43) * mm});
            skLineSegment(sketch, "E777", {"start": v(23.25, 161.43) * mm, "end": v(24, 162.17) * mm});
            skLineSegment(sketch, "E778", {"start": v(24, 162.17) * mm, "end": v(24.67, 162.97) * mm});
            skLineSegment(sketch, "E779", {"start": v(24.67, 162.97) * mm, "end": v(25.28, 163.82) * mm});
            skLineSegment(sketch, "E780", {"start": v(25.28, 163.82) * mm, "end": v(25.81, 164.73) * mm});
            skLineSegment(sketch, "E781", {"start": v(25.81, 164.73) * mm, "end": v(26.28, 165.66) * mm});
            skLineSegment(sketch, "E782", {"start": v(26.28, 165.66) * mm, "end": v(26.66, 166.63) * mm});
            skLineSegment(sketch, "E783", {"start": v(26.66, 166.63) * mm, "end": v(26.96, 167.65) * mm});
            skLineSegment(sketch, "E784", {"start": v(26.96, 167.65) * mm, "end": v(27.17, 168.67) * mm});
            skLineSegment(sketch, "E785", {"start": v(27.17, 168.67) * mm, "end": v(27.3, 169.72) * mm});
            skLineSegment(sketch, "E786", {"start": v(27.3, 169.72) * mm, "end": v(27.34, 170.76) * mm});
            skLineSegment(sketch, "E787", {"start": v(27.34, 170.76) * mm, "end": v(27.3, 171.82) * mm});
            skLineSegment(sketch, "E788", {"start": v(27.3, 171.82) * mm, "end": v(27.17, 172.86) * mm});
            skLineSegment(sketch, "E789", {"start": v(27.17, 172.86) * mm, "end": v(26.96, 173.87) * mm});
            skLineSegment(sketch, "E790", {"start": v(26.96, 173.87) * mm, "end": v(26.66, 174.89) * mm});
            skLineSegment(sketch, "E791", {"start": v(26.66, 174.89) * mm, "end": v(26.28, 175.86) * mm});
            skLineSegment(sketch, "E792", {"start": v(26.28, 175.86) * mm, "end": v(25.81, 176.82) * mm});
            skLineSegment(sketch, "E793", {"start": v(25.81, 176.82) * mm, "end": v(25.28, 177.7) * mm});
            skLineSegment(sketch, "E794", {"start": v(25.28, 177.7) * mm, "end": v(24.67, 178.57) * mm});
            skLineSegment(sketch, "E795", {"start": v(24.67, 178.57) * mm, "end": v(24, 179.38) * mm});
            skLineSegment(sketch, "E796", {"start": v(24, 179.38) * mm, "end": v(23.25, 180.12) * mm});
            skLineSegment(sketch, "E797", {"start": v(23.25, 180.12) * mm, "end": v(22.45, 180.8) * mm});
            skLineSegment(sketch, "E798", {"start": v(22.45, 180.8) * mm, "end": v(21.6, 181.39) * mm});
            skLineSegment(sketch, "E799", {"start": v(21.6, 181.39) * mm, "end": v(20.7, 181.94) * mm});
            skLineSegment(sketch, "E800", {"start": v(20.7, 181.94) * mm, "end": v(19.74, 182.4) * mm});
            skLineSegment(sketch, "E801", {"start": v(19.74, 182.4) * mm, "end": v(18.76, 182.78) * mm});
            skLineSegment(sketch, "E802", {"start": v(18.76, 182.78) * mm, "end": v(17.77, 183.08) * mm});
            skLineSegment(sketch, "E803", {"start": v(17.77, 183.08) * mm, "end": v(16.73, 183.3) * mm});
            skLineSegment(sketch, "E804", {"start": v(16.73, 183.3) * mm, "end": v(15.7, 183.42) * mm});
            skLineSegment(sketch, "E805", {"start": v(15.7, 183.42) * mm, "end": v(14.64, 183.46) * mm});
            skLineSegment(sketch, "E806", {"start": v(14.64, 183.46) * mm, "end": v(13.6, 183.42) * mm});
            skLineSegment(sketch, "E807", {"start": v(13.6, 183.42) * mm, "end": v(12.56, 183.3) * mm});
            skLineSegment(sketch, "E808", {"start": v(12.56, 183.3) * mm, "end": v(11.53, 183.08) * mm});
            skLineSegment(sketch, "E809", {"start": v(11.53, 183.08) * mm, "end": v(10.53, 182.78) * mm});
            skLineSegment(sketch, "E810", {"start": v(10.53, 182.78) * mm, "end": v(9.54, 182.4) * mm});
            skLineSegment(sketch, "E811", {"start": v(9.54, 182.4) * mm, "end": v(8.6, 181.94) * mm});
            skLineSegment(sketch, "E812", {"start": v(8.6, 181.94) * mm, "end": v(7.7, 181.39) * mm});
            skLineSegment(sketch, "E813", {"start": v(7.7, 181.39) * mm, "end": v(6.85, 180.8) * mm});
            skLineSegment(sketch, "E814", {"start": v(6.85, 180.8) * mm, "end": v(6.04, 180.12) * mm});
            skLineSegment(sketch, "E815", {"start": v(6.04, 180.12) * mm, "end": v(5.3, 179.38) * mm});
            skLineSegment(sketch, "E816", {"start": v(5.3, 179.38) * mm, "end": v(4.62, 178.57) * mm});
            skLineSegment(sketch, "E817", {"start": v(4.62, 178.57) * mm, "end": v(4.01, 177.7) * mm});
            skLineSegment(sketch, "E818", {"start": v(4.01, 177.7) * mm, "end": v(3.48, 176.82) * mm});
            skLineSegment(sketch, "E819", {"start": v(3.48, 176.82) * mm, "end": v(3.02, 175.86) * mm});
            skLineSegment(sketch, "E820", {"start": v(3.02, 175.86) * mm, "end": v(2.64, 174.89) * mm});
            skLineSegment(sketch, "E821", {"start": v(2.64, 174.89) * mm, "end": v(2.34, 173.87) * mm});
            skLineSegment(sketch, "E822", {"start": v(2.34, 173.87) * mm, "end": v(2.13, 172.86) * mm});
            skLineSegment(sketch, "E823", {"start": v(2.13, 172.86) * mm, "end": v(1.98, 171.82) * mm});
            skLineSegment(sketch, "E824", {"start": v(1.98, 171.82) * mm, "end": v(1.94, 170.76) * mm});
            skLineSegment(sketch, "E825", {"start": v(1.94, 170.76) * mm, "end": v(1.98, 169.72) * mm});
            skLineSegment(sketch, "E826", {"start": v(1.98, 169.72) * mm, "end": v(2.13, 168.67) * mm});
            skLineSegment(sketch, "E827", {"start": v(2.13, 168.67) * mm, "end": v(2.34, 167.65) * mm});
            skLineSegment(sketch, "E828", {"start": v(2.34, 167.65) * mm, "end": v(2.64, 166.63) * mm});
            skLineSegment(sketch, "E829", {"start": v(2.64, 166.63) * mm, "end": v(3.02, 165.66) * mm});
            skLineSegment(sketch, "E830", {"start": v(3.02, 165.66) * mm, "end": v(3.48, 164.73) * mm});
            skLineSegment(sketch, "E831", {"start": v(3.48, 164.73) * mm, "end": v(4.01, 163.82) * mm});
            skLineSegment(sketch, "E832", {"start": v(4.01, 163.82) * mm, "end": v(4.62, 162.97) * mm});
            skLineSegment(sketch, "E833", {"start": v(4.62, 162.97) * mm, "end": v(5.3, 162.17) * mm});
            skLineSegment(sketch, "E834", {"start": v(5.3, 162.17) * mm, "end": v(6.04, 161.43) * mm});
            skLineSegment(sketch, "E835", {"start": v(6.04, 161.43) * mm, "end": v(6.85, 160.75) * mm});
            skLineSegment(sketch, "E836", {"start": v(6.85, 160.75) * mm, "end": v(7.7, 160.14) * mm});
            skLineSegment(sketch, "E837", {"start": v(7.7, 160.14) * mm, "end": v(8.6, 159.6) * mm});
            skLineSegment(sketch, "E838", {"start": v(8.6, 159.6) * mm, "end": v(9.54, 159.14) * mm});
            skLineSegment(sketch, "E839", {"start": v(9.54, 159.14) * mm, "end": v(10.53, 158.76) * mm});
            skLineSegment(sketch, "E840", {"start": v(10.53, 158.76) * mm, "end": v(11.53, 158.46) * mm});
            skLineSegment(sketch, "E841", {"start": v(11.53, 158.46) * mm, "end": v(12.56, 158.23) * mm});
            skLineSegment(sketch, "E842", {"start": v(12.56, 158.23) * mm, "end": v(13.6, 158.1) * mm});
            skLineSegment(sketch, "E843", {"start": v(13.6, 158.1) * mm, "end": v(14.64, 158.06) * mm});
            skLineSegment(sketch, "E844", {"start": v(-13.73, 328.58) * mm, "end": v(-17.32, 327.88) * mm});
            skLineSegment(sketch, "E845", {"start": v(-17.32, 327.88) * mm, "end": v(-20.9, 327.12) * mm});
            skLineSegment(sketch, "E846", {"start": v(-20.9, 327.12) * mm, "end": v(-24.46, 326.27) * mm});
            skLineSegment(sketch, "E847", {"start": v(-24.46, 326.27) * mm, "end": v(-27.97, 325.34) * mm});
            skLineSegment(sketch, "E848", {"start": v(-27.97, 325.34) * mm, "end": v(-31.49, 324.33) * mm});
            skLineSegment(sketch, "E849", {"start": v(-31.49, 324.33) * mm, "end": v(-34.98, 323.23) * mm});
            skLineSegment(sketch, "E850", {"start": v(-34.98, 323.23) * mm, "end": v(-38.45, 322.06) * mm});
            skLineSegment(sketch, "E851", {"start": v(-38.45, 322.06) * mm, "end": v(-41.88, 320.81) * mm});
            skLineSegment(sketch, "E852", {"start": v(-41.88, 320.81) * mm, "end": v(-45.29, 319.48) * mm});
            skLineSegment(sketch, "E853", {"start": v(-45.29, 319.48) * mm, "end": v(-48.65, 318.08) * mm});
            skLineSegment(sketch, "E854", {"start": v(-48.65, 318.08) * mm, "end": v(-52, 316.6) * mm});
            skLineSegment(sketch, "E855", {"start": v(-52, 316.6) * mm, "end": v(-55.3, 315.06) * mm});
            skLineSegment(sketch, "E856", {"start": v(-55.3, 315.06) * mm, "end": v(-58.56, 313.43) * mm});
            skLineSegment(sketch, "E857", {"start": v(-58.56, 313.43) * mm, "end": v(-61.8, 311.71) * mm});
            skLineSegment(sketch, "E858", {"start": v(-61.8, 311.71) * mm, "end": v(-65, 309.93) * mm});
            skLineSegment(sketch, "E859", {"start": v(-65, 309.93) * mm, "end": v(-68.15, 308.1) * mm});
            skLineSegment(sketch, "E860", {"start": v(-68.15, 308.1) * mm, "end": v(-71.24, 306.17) * mm});
            skLineSegment(sketch, "E861", {"start": v(-71.24, 306.17) * mm, "end": v(-74.3, 304.18) * mm});
            skLineSegment(sketch, "E862", {"start": v(-74.3, 304.18) * mm, "end": v(-77.31, 302.1) * mm});
            skLineSegment(sketch, "E863", {"start": v(-78.94, 304.43) * mm, "end": v(-55.9, 271.52) * mm});
            skLineSegment(sketch, "E864", {"start": v(-77.31, 302.1) * mm, "end": v(-92.93, 291.18) * mm});
            skLineSegment(sketch, "E865", {"start": v(115.67, 295.29) * mm, "end": v(112.83, 297.53) * mm});
            skLineSegment(sketch, "E866", {"start": v(112.83, 297.53) * mm, "end": v(109.93, 299.7) * mm});
            skLineSegment(sketch, "E867", {"start": v(109.93, 299.7) * mm, "end": v(107, 301.83) * mm});
            skLineSegment(sketch, "E868", {"start": v(107, 301.83) * mm, "end": v(104.02, 303.88) * mm});
            skLineSegment(sketch, "E869", {"start": v(104.02, 303.88) * mm, "end": v(101, 305.87) * mm});
            skLineSegment(sketch, "E870", {"start": v(101, 305.87) * mm, "end": v(97.93, 307.77) * mm});
            skLineSegment(sketch, "E871", {"start": v(97.93, 307.77) * mm, "end": v(94.82, 309.62) * mm});
            skLineSegment(sketch, "E872", {"start": v(94.82, 309.62) * mm, "end": v(91.66, 311.4) * mm});
            skLineSegment(sketch, "E873", {"start": v(91.66, 311.4) * mm, "end": v(88.47, 313.1) * mm});
            skLineSegment(sketch, "E874", {"start": v(88.47, 313.1) * mm, "end": v(85.23, 314.74) * mm});
            skLineSegment(sketch, "E875", {"start": v(85.23, 314.74) * mm, "end": v(81.97, 316.28) * mm});
            skLineSegment(sketch, "E876", {"start": v(81.97, 316.28) * mm, "end": v(78.67, 317.76) * mm});
            skLineSegment(sketch, "E877", {"start": v(78.67, 317.76) * mm, "end": v(75.32, 319.18) * mm});
            skLineSegment(sketch, "E878", {"start": v(75.32, 319.18) * mm, "end": v(71.96, 320.52) * mm});
            skLineSegment(sketch, "E879", {"start": v(71.96, 320.52) * mm, "end": v(68.57, 321.77) * mm});
            skLineSegment(sketch, "E880", {"start": v(68.57, 321.77) * mm, "end": v(65.14, 322.95) * mm});
            skLineSegment(sketch, "E881", {"start": v(65.14, 322.95) * mm, "end": v(61.71, 324.05) * mm});
            skLineSegment(sketch, "E882", {"start": v(61.71, 324.05) * mm, "end": v(58.24, 325.07) * mm});
            skLineSegment(sketch, "E883", {"start": v(58.24, 325.07) * mm, "end": v(54.75, 326.02) * mm});
            skLineSegment(sketch, "E884", {"start": v(54.75, 326.02) * mm, "end": v(51.23, 326.87) * mm});
            skLineSegment(sketch, "E885", {"start": v(51.23, 326.87) * mm, "end": v(47.7, 327.67) * mm});
            skLineSegment(sketch, "E886", {"start": v(47.7, 327.67) * mm, "end": v(44.14, 328.37) * mm});
            skLineSegment(sketch, "E887", {"start": v(44.14, 328.37) * mm, "end": v(40.59, 328.98) * mm});
            skLineSegment(sketch, "E888", {"start": v(40.59, 328.98) * mm, "end": v(37, 329.53) * mm});
            skLineSegment(sketch, "E889", {"start": v(37, 329.53) * mm, "end": v(33.41, 330) * mm});
            skLineSegment(sketch, "E890", {"start": v(33.41, 330) * mm, "end": v(29.81, 330.38) * mm});
            skLineSegment(sketch, "E891", {"start": v(29.81, 330.38) * mm, "end": v(26.21, 330.68) * mm});
            skLineSegment(sketch, "E892", {"start": v(26.21, 330.68) * mm, "end": v(22.6, 330.9) * mm});
            skLineSegment(sketch, "E893", {"start": v(22.6, 330.9) * mm, "end": v(18.98, 331.04) * mm});
            skLineSegment(sketch, "E894", {"start": v(18.98, 331.04) * mm, "end": v(15.36, 331.1) * mm});
            skLineSegment(sketch, "E895", {"start": v(15.36, 331.1) * mm, "end": v(11.74, 331.08) * mm});
            skLineSegment(sketch, "E896", {"start": v(11.74, 331.08) * mm, "end": v(8.12, 330.97) * mm});
            skLineSegment(sketch, "E897", {"start": v(8.12, 330.97) * mm, "end": v(4.52, 330.78) * mm});
            skLineSegment(sketch, "E898", {"start": v(4.52, 330.78) * mm, "end": v(0.9, 330.5) * mm});
            skLineSegment(sketch, "E899", {"start": v(0.9, 330.5) * mm, "end": v(-2.7, 330.17) * mm});
            skLineSegment(sketch, "E900", {"start": v(-2.7, 330.17) * mm, "end": v(-6.3, 329.72) * mm});
            skLineSegment(sketch, "E901", {"start": v(-94.54, 293.49) * mm, "end": v(-71.51, 260.6) * mm});
            skLineSegment(sketch, "E902", {"start": v(-85.52, 289.4) * mm, "end": v(-85.5, 289.61) * mm});
            skLineSegment(sketch, "E903", {"start": v(-85.5, 289.61) * mm, "end": v(-85.3, 289.57) * mm});
            skLineSegment(sketch, "E904", {"start": v(-85.3, 289.57) * mm, "end": v(-85.31, 289.36) * mm});
            skLineSegment(sketch, "E905", {"start": v(-85.31, 289.36) * mm, "end": v(-85.52, 289.4) * mm});
            skLineSegment(sketch, "E906", {"start": v(-85.52, 289.4) * mm, "end": v(-85.71, 289.63) * mm});
            skLineSegment(sketch, "E907", {"start": v(-85.71, 289.63) * mm, "end": v(-85.76, 289.97) * mm});
            skLineSegment(sketch, "E908", {"start": v(-85.76, 289.97) * mm, "end": v(-85.74, 290.18) * mm});
            skLineSegment(sketch, "E909", {"start": v(-84.8, 289.93) * mm, "end": v(-84.76, 290.14) * mm});
            skLineSegment(sketch, "E910", {"start": v(-84.76, 290.14) * mm, "end": v(-84.55, 290.12) * mm});
            skLineSegment(sketch, "E911", {"start": v(-84.55, 290.12) * mm, "end": v(-84.6, 289.9) * mm});
            skLineSegment(sketch, "E912", {"start": v(-84.6, 289.9) * mm, "end": v(-84.8, 289.93) * mm});
            skLineSegment(sketch, "E913", {"start": v(-84.8, 289.93) * mm, "end": v(-84.97, 290.18) * mm});
            skLineSegment(sketch, "E914", {"start": v(-84.97, 290.18) * mm, "end": v(-85.04, 290.5) * mm});
            skLineSegment(sketch, "E915", {"start": v(-85.04, 290.5) * mm, "end": v(-85, 290.71) * mm});
            skLineSegment(sketch, "E916", {"start": v(-83.85, 291.2) * mm, "end": v(-82.62, 292.09) * mm});
            skLineSegment(sketch, "E917", {"start": v(-82.62, 292.09) * mm, "end": v(-83.3, 293.27) * mm});
            skLineSegment(sketch, "E918", {"start": v(-83.3, 293.27) * mm, "end": v(-83.34, 293.06) * mm});
            skLineSegment(sketch, "E919", {"start": v(-83.34, 293.06) * mm, "end": v(-83.62, 292.66) * mm});
            skLineSegment(sketch, "E920", {"start": v(-83.62, 292.66) * mm, "end": v(-83.98, 292.4) * mm});
            skLineSegment(sketch, "E921", {"start": v(-83.98, 292.4) * mm, "end": v(-84.44, 292.26) * mm});
            skLineSegment(sketch, "E922", {"start": v(-84.44, 292.26) * mm, "end": v(-84.87, 292.32) * mm});
            skLineSegment(sketch, "E923", {"start": v(-84.87, 292.32) * mm, "end": v(-85.25, 292.6) * mm});
            skLineSegment(sketch, "E924", {"start": v(-85.25, 292.6) * mm, "end": v(-85.44, 292.85) * mm});
            skLineSegment(sketch, "E925", {"start": v(-85.44, 292.85) * mm, "end": v(-85.57, 293.3) * mm});
            skLineSegment(sketch, "E926", {"start": v(-85.57, 293.3) * mm, "end": v(-85.5, 293.72) * mm});
            skLineSegment(sketch, "E927", {"start": v(-85.5, 293.72) * mm, "end": v(-85.23, 294.12) * mm});
            skLineSegment(sketch, "E928", {"start": v(-85.23, 294.12) * mm, "end": v(-84.87, 294.38) * mm});
            skLineSegment(sketch, "E929", {"start": v(-84.87, 294.38) * mm, "end": v(-84.4, 294.52) * mm});
            skLineSegment(sketch, "E930", {"start": v(-84.4, 294.52) * mm, "end": v(-84.2, 294.5) * mm});
            skLineSegment(sketch, "E931", {"start": v(-84.2, 294.5) * mm, "end": v(-83.9, 294.33) * mm});
            skLineSegment(sketch, "E932", {"start": v(-79.94, 294.06) * mm, "end": v(-81.65, 292.79) * mm});
            skLineSegment(sketch, "E933", {"start": v(-81.65, 292.79) * mm, "end": v(-82.3, 296.26) * mm});
            skLineSegment(sketch, "E934", {"start": v(-80.55, 297.17) * mm, "end": v(-80.5, 297.38) * mm});
            skLineSegment(sketch, "E935", {"start": v(-80.5, 297.38) * mm, "end": v(-80.72, 297.42) * mm});
            skLineSegment(sketch, "E936", {"start": v(-80.72, 297.42) * mm, "end": v(-80.74, 297.21) * mm});
            skLineSegment(sketch, "E937", {"start": v(-32.01, 198.15) * mm, "end": v(-31.3, 197.26) * mm});
            skLineSegment(sketch, "E938", {"start": v(-31.3, 197.26) * mm, "end": v(-28.99, 199.87) * mm});
            skLineSegment(sketch, "E939", {"start": v(40.71, 229.67) * mm, "end": v(41.75, 229.71) * mm});
            skLineSegment(sketch, "E940", {"start": v(41.75, 229.71) * mm, "end": v(42.79, 229.84) * mm});
            skLineSegment(sketch, "E941", {"start": v(42.79, 229.84) * mm, "end": v(43.83, 230.05) * mm});
            skLineSegment(sketch, "E942", {"start": v(43.83, 230.05) * mm, "end": v(44.82, 230.37) * mm});
            skLineSegment(sketch, "E943", {"start": v(44.82, 230.37) * mm, "end": v(45.82, 230.75) * mm});
            skLineSegment(sketch, "E944", {"start": v(45.82, 230.75) * mm, "end": v(46.75, 231.2) * mm});
            skLineSegment(sketch, "E945", {"start": v(46.75, 231.2) * mm, "end": v(47.66, 231.74) * mm});
            skLineSegment(sketch, "E946", {"start": v(47.66, 231.74) * mm, "end": v(48.5, 232.36) * mm});
            skLineSegment(sketch, "E947", {"start": v(48.5, 232.36) * mm, "end": v(49.3, 233.03) * mm});
            skLineSegment(sketch, "E948", {"start": v(49.3, 233.03) * mm, "end": v(50.05, 233.78) * mm});
            skLineSegment(sketch, "E949", {"start": v(50.05, 233.78) * mm, "end": v(50.73, 234.58) * mm});
            skLineSegment(sketch, "E950", {"start": v(50.73, 234.58) * mm, "end": v(51.34, 235.43) * mm});
            skLineSegment(sketch, "E951", {"start": v(51.34, 235.43) * mm, "end": v(51.87, 236.34) * mm});
            skLineSegment(sketch, "E952", {"start": v(51.87, 236.34) * mm, "end": v(52.33, 237.27) * mm});
            skLineSegment(sketch, "E953", {"start": v(52.33, 237.27) * mm, "end": v(52.72, 238.24) * mm});
            skLineSegment(sketch, "E954", {"start": v(52.72, 238.24) * mm, "end": v(53.01, 239.26) * mm});
            skLineSegment(sketch, "E955", {"start": v(53.01, 239.26) * mm, "end": v(53.22, 240.27) * mm});
            skLineSegment(sketch, "E956", {"start": v(53.22, 240.27) * mm, "end": v(53.37, 241.33) * mm});
            skLineSegment(sketch, "E957", {"start": v(53.37, 241.33) * mm, "end": v(53.41, 242.37) * mm});
            skLineSegment(sketch, "E958", {"start": v(53.41, 242.37) * mm, "end": v(53.37, 243.43) * mm});
            skLineSegment(sketch, "E959", {"start": v(53.37, 243.43) * mm, "end": v(53.22, 244.46) * mm});
            skLineSegment(sketch, "E960", {"start": v(53.22, 244.46) * mm, "end": v(53.01, 245.48) * mm});
            skLineSegment(sketch, "E961", {"start": v(53.01, 245.48) * mm, "end": v(52.72, 246.5) * mm});
            skLineSegment(sketch, "E962", {"start": v(52.72, 246.5) * mm, "end": v(52.33, 247.47) * mm});
            skLineSegment(sketch, "E963", {"start": v(52.33, 247.47) * mm, "end": v(51.87, 248.42) * mm});
            skLineSegment(sketch, "E964", {"start": v(51.87, 248.42) * mm, "end": v(51.34, 249.31) * mm});
            skLineSegment(sketch, "E965", {"start": v(51.34, 249.31) * mm, "end": v(50.73, 250.18) * mm});
            skLineSegment(sketch, "E966", {"start": v(50.73, 250.18) * mm, "end": v(50.05, 250.96) * mm});
            skLineSegment(sketch, "E967", {"start": v(50.05, 250.96) * mm, "end": v(49.3, 251.72) * mm});
            skLineSegment(sketch, "E968", {"start": v(49.3, 251.72) * mm, "end": v(48.5, 252.4) * mm});
            skLineSegment(sketch, "E969", {"start": v(48.5, 252.4) * mm, "end": v(47.66, 253) * mm});
            skLineSegment(sketch, "E970", {"start": v(47.66, 253) * mm, "end": v(46.75, 253.54) * mm});
            skLineSegment(sketch, "E971", {"start": v(46.75, 253.54) * mm, "end": v(45.82, 254.01) * mm});
            skLineSegment(sketch, "E972", {"start": v(45.82, 254.01) * mm, "end": v(44.82, 254.4) * mm});
            skLineSegment(sketch, "E973", {"start": v(44.82, 254.4) * mm, "end": v(43.83, 254.69) * mm});
            skLineSegment(sketch, "E974", {"start": v(43.83, 254.69) * mm, "end": v(42.79, 254.9) * mm});
            skLineSegment(sketch, "E975", {"start": v(42.79, 254.9) * mm, "end": v(41.75, 255.03) * mm});
            skLineSegment(sketch, "E976", {"start": v(41.75, 255.03) * mm, "end": v(40.71, 255.07) * mm});
            skLineSegment(sketch, "E977", {"start": v(40.71, 255.07) * mm, "end": v(39.66, 255.03) * mm});
            skLineSegment(sketch, "E978", {"start": v(39.66, 255.03) * mm, "end": v(38.62, 254.9) * mm});
            skLineSegment(sketch, "E979", {"start": v(38.62, 254.9) * mm, "end": v(37.58, 254.69) * mm});
            skLineSegment(sketch, "E980", {"start": v(37.58, 254.69) * mm, "end": v(36.59, 254.4) * mm});
            skLineSegment(sketch, "E981", {"start": v(36.59, 254.4) * mm, "end": v(35.61, 254.01) * mm});
            skLineSegment(sketch, "E982", {"start": v(35.61, 254.01) * mm, "end": v(34.66, 253.54) * mm});
            skLineSegment(sketch, "E983", {"start": v(34.66, 253.54) * mm, "end": v(33.75, 253) * mm});
            skLineSegment(sketch, "E984", {"start": v(33.75, 253) * mm, "end": v(32.9, 252.4) * mm});
            skLineSegment(sketch, "E985", {"start": v(32.9, 252.4) * mm, "end": v(32.1, 251.72) * mm});
            skLineSegment(sketch, "E986", {"start": v(32.1, 251.72) * mm, "end": v(31.36, 250.96) * mm});
            skLineSegment(sketch, "E987", {"start": v(31.36, 250.96) * mm, "end": v(30.68, 250.18) * mm});
            skLineSegment(sketch, "E988", {"start": v(30.68, 250.18) * mm, "end": v(30.07, 249.31) * mm});
            skLineSegment(sketch, "E989", {"start": v(30.07, 249.31) * mm, "end": v(29.54, 248.42) * mm});
            skLineSegment(sketch, "E990", {"start": v(29.54, 248.42) * mm, "end": v(29.07, 247.47) * mm});
            skLineSegment(sketch, "E991", {"start": v(29.07, 247.47) * mm, "end": v(28.7, 246.5) * mm});
            skLineSegment(sketch, "E992", {"start": v(28.7, 246.5) * mm, "end": v(28.4, 245.48) * mm});
            skLineSegment(sketch, "E993", {"start": v(28.4, 245.48) * mm, "end": v(28.18, 244.46) * mm});
            skLineSegment(sketch, "E994", {"start": v(28.18, 244.46) * mm, "end": v(28.06, 243.43) * mm});
            skLineSegment(sketch, "E995", {"start": v(28.06, 243.43) * mm, "end": v(28.01, 242.37) * mm});
            skLineSegment(sketch, "E996", {"start": v(28.01, 242.37) * mm, "end": v(28.06, 241.33) * mm});
            skLineSegment(sketch, "E997", {"start": v(28.06, 241.33) * mm, "end": v(28.18, 240.27) * mm});
            skLineSegment(sketch, "E998", {"start": v(28.18, 240.27) * mm, "end": v(28.4, 239.26) * mm});
            skLineSegment(sketch, "E999", {"start": v(28.4, 239.26) * mm, "end": v(28.7, 238.24) * mm});
            skLineSegment(sketch, "E1000", {"start": v(28.7, 238.24) * mm, "end": v(29.07, 237.27) * mm});
            skLineSegment(sketch, "E1001", {"start": v(29.07, 237.27) * mm, "end": v(29.54, 236.34) * mm});
            skLineSegment(sketch, "E1002", {"start": v(29.54, 236.34) * mm, "end": v(30.07, 235.43) * mm});
            skLineSegment(sketch, "E1003", {"start": v(30.07, 235.43) * mm, "end": v(30.68, 234.58) * mm});
            skLineSegment(sketch, "E1004", {"start": v(30.68, 234.58) * mm, "end": v(31.36, 233.78) * mm});
            skLineSegment(sketch, "E1005", {"start": v(31.36, 233.78) * mm, "end": v(32.1, 233.03) * mm});
            skLineSegment(sketch, "E1006", {"start": v(32.1, 233.03) * mm, "end": v(32.9, 232.36) * mm});
            skLineSegment(sketch, "E1007", {"start": v(32.9, 232.36) * mm, "end": v(33.75, 231.74) * mm});
            skLineSegment(sketch, "E1008", {"start": v(33.75, 231.74) * mm, "end": v(34.66, 231.2) * mm});
            skLineSegment(sketch, "E1009", {"start": v(34.66, 231.2) * mm, "end": v(35.61, 230.75) * mm});
            skLineSegment(sketch, "E1010", {"start": v(35.61, 230.75) * mm, "end": v(36.59, 230.37) * mm});
            skLineSegment(sketch, "E1011", {"start": v(36.59, 230.37) * mm, "end": v(37.58, 230.05) * mm});
            skLineSegment(sketch, "E1012", {"start": v(37.58, 230.05) * mm, "end": v(38.62, 229.84) * mm});
            skLineSegment(sketch, "E1013", {"start": v(38.62, 229.84) * mm, "end": v(39.66, 229.71) * mm});
            skLineSegment(sketch, "E1014", {"start": v(39.66, 229.71) * mm, "end": v(40.71, 229.67) * mm});
            skLineSegment(sketch, "E1015", {"start": v(9.73, 185.28) * mm, "end": v(6.72, 186.64) * mm});
            skLineSegment(sketch, "E1016", {"start": v(9.28, 186.2) * mm, "end": v(9.13, 186.49) * mm});
            skLineSegment(sketch, "E1017", {"start": v(9.13, 186.49) * mm, "end": v(8.84, 186.79) * mm});
            skLineSegment(sketch, "E1018", {"start": v(8.84, 186.79) * mm, "end": v(8.37, 186.95) * mm});
            skLineSegment(sketch, "E1019", {"start": v(8.37, 186.95) * mm, "end": v(8.08, 186.93) * mm});
            skLineSegment(sketch, "E1020", {"start": v(8.08, 186.93) * mm, "end": v(7.6, 186.79) * mm});
            skLineSegment(sketch, "E1021", {"start": v(7.6, 186.79) * mm, "end": v(7.31, 186.49) * mm});
            skLineSegment(sketch, "E1022", {"start": v(7.31, 186.49) * mm, "end": v(7.16, 186.2) * mm});
            skLineSegment(sketch, "E1023", {"start": v(7.16, 186.2) * mm, "end": v(7.16, 185.73) * mm});
            skLineSegment(sketch, "E1024", {"start": v(7.16, 185.73) * mm, "end": v(7.31, 185.43) * mm});
            skLineSegment(sketch, "E1025", {"start": v(7.31, 185.43) * mm, "end": v(7.6, 185.13) * mm});
            skLineSegment(sketch, "E1026", {"start": v(7.6, 185.13) * mm, "end": v(8.08, 184.99) * mm});
            skLineSegment(sketch, "E1027", {"start": v(8.08, 184.99) * mm, "end": v(8.37, 184.99) * mm});
            skLineSegment(sketch, "E1028", {"start": v(8.37, 184.99) * mm, "end": v(8.84, 185.13) * mm});
            skLineSegment(sketch, "E1029", {"start": v(8.84, 185.13) * mm, "end": v(9.13, 185.43) * mm});
            skLineSegment(sketch, "E1030", {"start": v(9.13, 185.43) * mm, "end": v(9.28, 185.73) * mm});
            skLineSegment(sketch, "E1031", {"start": v(9.28, 185.73) * mm, "end": v(9.28, 186.2) * mm});
            skLineSegment(sketch, "E1032", {"start": v(9.28, 189.37) * mm, "end": v(9.43, 189.07) * mm});
            skLineSegment(sketch, "E1033", {"start": v(9.43, 189.07) * mm, "end": v(9.9, 188.6) * mm});
            skLineSegment(sketch, "E1034", {"start": v(9.9, 188.6) * mm, "end": v(6.72, 188.6) * mm});
            skLineSegment(sketch, "E1035", {"start": v(9.87, 192.08) * mm, "end": v(9.87, 190.43) * mm});
            skLineSegment(sketch, "E1036", {"start": v(9.87, 190.43) * mm, "end": v(8.67, 191.34) * mm});
            skLineSegment(sketch, "E1037", {"start": v(8.67, 191.34) * mm, "end": v(8.67, 190.87) * mm});
            skLineSegment(sketch, "E1038", {"start": v(8.67, 190.87) * mm, "end": v(8.52, 190.57) * mm});
            skLineSegment(sketch, "E1039", {"start": v(8.52, 190.57) * mm, "end": v(8.37, 190.43) * mm});
            skLineSegment(sketch, "E1040", {"start": v(8.37, 190.43) * mm, "end": v(7.93, 190.28) * mm});
            skLineSegment(sketch, "E1041", {"start": v(7.93, 190.28) * mm, "end": v(7.6, 190.28) * mm});
            skLineSegment(sketch, "E1042", {"start": v(7.6, 190.28) * mm, "end": v(7.16, 190.43) * mm});
            skLineSegment(sketch, "E1043", {"start": v(7.16, 190.43) * mm, "end": v(6.87, 190.72) * mm});
            skLineSegment(sketch, "E1044", {"start": v(6.87, 190.72) * mm, "end": v(6.7, 191.17) * mm});
            skLineSegment(sketch, "E1045", {"start": v(6.7, 191.17) * mm, "end": v(6.7, 191.63) * mm});
            skLineSegment(sketch, "E1046", {"start": v(6.7, 191.63) * mm, "end": v(6.87, 192.08) * mm});
            skLineSegment(sketch, "E1047", {"start": v(6.87, 192.08) * mm, "end": v(7.02, 192.23) * mm});
            skLineSegment(sketch, "E1048", {"start": v(7.02, 192.23) * mm, "end": v(7.31, 192.4) * mm});
            skLineSegment(sketch, "E1049", {"start": v(7.76, 195.4) * mm, "end": v(7.48, 195.38) * mm});
            skLineSegment(sketch, "E1050", {"start": v(7.48, 195.38) * mm, "end": v(7.23, 195.27) * mm});
            skLineSegment(sketch, "E1051", {"start": v(7.23, 195.27) * mm, "end": v(7.02, 195.1) * mm});
            skLineSegment(sketch, "E1052", {"start": v(7.02, 195.1) * mm, "end": v(6.85, 194.87) * mm});
            skLineSegment(sketch, "E1053", {"start": v(6.85, 194.87) * mm, "end": v(6.74, 194.62) * mm});
            skLineSegment(sketch, "E1054", {"start": v(6.74, 194.62) * mm, "end": v(6.7, 194.34) * mm});
            skLineSegment(sketch, "E1055", {"start": v(6.7, 194.34) * mm, "end": v(6.74, 194.09) * mm});
            skLineSegment(sketch, "E1056", {"start": v(6.74, 194.09) * mm, "end": v(6.85, 193.81) * mm});
            skLineSegment(sketch, "E1057", {"start": v(6.85, 193.81) * mm, "end": v(7.02, 193.6) * mm});
            skLineSegment(sketch, "E1058", {"start": v(7.02, 193.6) * mm, "end": v(7.23, 193.43) * mm});
            skLineSegment(sketch, "E1059", {"start": v(7.23, 193.43) * mm, "end": v(7.5, 193.33) * mm});
            skLineSegment(sketch, "E1060", {"start": v(7.5, 193.33) * mm, "end": v(7.76, 193.28) * mm});
            skLineSegment(sketch, "E1061", {"start": v(7.76, 193.28) * mm, "end": v(8.82, 193.3) * mm});
            skLineSegment(sketch, "E1062", {"start": v(8.82, 193.3) * mm, "end": v(9.1, 193.33) * mm});
            skLineSegment(sketch, "E1063", {"start": v(9.1, 193.33) * mm, "end": v(9.35, 193.43) * mm});
            skLineSegment(sketch, "E1064", {"start": v(9.35, 193.43) * mm, "end": v(9.58, 193.6) * mm});
            skLineSegment(sketch, "E1065", {"start": v(9.58, 193.6) * mm, "end": v(9.75, 193.83) * mm});
            skLineSegment(sketch, "E1066", {"start": v(9.75, 193.83) * mm, "end": v(9.85, 194.09) * mm});
            skLineSegment(sketch, "E1067", {"start": v(9.85, 194.09) * mm, "end": v(9.87, 194.36) * mm});
            skLineSegment(sketch, "E1068", {"start": v(9.87, 194.36) * mm, "end": v(9.85, 194.62) * mm});
            skLineSegment(sketch, "E1069", {"start": v(9.85, 194.62) * mm, "end": v(9.75, 194.9) * mm});
            skLineSegment(sketch, "E1070", {"start": v(9.75, 194.9) * mm, "end": v(9.58, 195.1) * mm});
            skLineSegment(sketch, "E1071", {"start": v(9.58, 195.1) * mm, "end": v(9.35, 195.27) * mm});
            skLineSegment(sketch, "E1072", {"start": v(9.35, 195.27) * mm, "end": v(9.1, 195.38) * mm});
            skLineSegment(sketch, "E1073", {"start": v(9.1, 195.38) * mm, "end": v(8.82, 195.42) * mm});
            skLineSegment(sketch, "E1074", {"start": v(8.82, 195.42) * mm, "end": v(7.76, 195.4) * mm});
            skLineSegment(sketch, "E1075", {"start": v(7.02, 196.78) * mm, "end": v(6.87, 196.92) * mm});
            skLineSegment(sketch, "E1076", {"start": v(6.87, 196.92) * mm, "end": v(6.7, 196.78) * mm});
            skLineSegment(sketch, "E1077", {"start": v(6.7, 196.78) * mm, "end": v(6.87, 196.63) * mm});
            skLineSegment(sketch, "E1078", {"start": v(9.28, 199.34) * mm, "end": v(9.43, 199.04) * mm});
            skLineSegment(sketch, "E1079", {"start": v(9.43, 199.04) * mm, "end": v(9.87, 198.6) * mm});
            skLineSegment(sketch, "E1080", {"start": v(9.87, 198.6) * mm, "end": v(6.7, 198.58) * mm});
            skLineSegment(sketch, "E1081", {"start": v(13.7, 221.63) * mm, "end": v(10.68, 222.98) * mm});
            skLineSegment(sketch, "E1082", {"start": v(13.24, 222.54) * mm, "end": v(13.1, 222.83) * mm});
            skLineSegment(sketch, "E1083", {"start": v(13.1, 222.83) * mm, "end": v(12.8, 223.15) * mm});
            skLineSegment(sketch, "E1084", {"start": v(12.8, 223.15) * mm, "end": v(12.35, 223.3) * mm});
            skLineSegment(sketch, "E1085", {"start": v(12.35, 223.3) * mm, "end": v(12.03, 223.3) * mm});
            skLineSegment(sketch, "E1086", {"start": v(12.03, 223.3) * mm, "end": v(11.59, 223.15) * mm});
            skLineSegment(sketch, "E1087", {"start": v(11.59, 223.15) * mm, "end": v(11.3, 222.83) * mm});
            skLineSegment(sketch, "E1088", {"start": v(11.3, 222.83) * mm, "end": v(11.12, 222.54) * mm});
            skLineSegment(sketch, "E1089", {"start": v(11.12, 222.54) * mm, "end": v(11.12, 222.1) * mm});
            skLineSegment(sketch, "E1090", {"start": v(11.12, 222.1) * mm, "end": v(11.3, 221.77) * mm});
            skLineSegment(sketch, "E1091", {"start": v(11.3, 221.77) * mm, "end": v(11.59, 221.48) * mm});
            skLineSegment(sketch, "E1092", {"start": v(11.59, 221.48) * mm, "end": v(12.03, 221.33) * mm});
            skLineSegment(sketch, "E1093", {"start": v(12.03, 221.33) * mm, "end": v(12.35, 221.33) * mm});
            skLineSegment(sketch, "E1094", {"start": v(12.35, 221.33) * mm, "end": v(12.8, 221.48) * mm});
            skLineSegment(sketch, "E1095", {"start": v(12.8, 221.48) * mm, "end": v(13.1, 221.77) * mm});
            skLineSegment(sketch, "E1096", {"start": v(13.1, 221.77) * mm, "end": v(13.24, 222.1) * mm});
            skLineSegment(sketch, "E1097", {"start": v(13.24, 222.1) * mm, "end": v(13.24, 222.54) * mm});
            skLineSegment(sketch, "E1098", {"start": v(13.85, 226) * mm, "end": v(13.85, 224.36) * mm});
            skLineSegment(sketch, "E1099", {"start": v(13.85, 224.36) * mm, "end": v(12.65, 225.27) * mm});
            skLineSegment(sketch, "E1100", {"start": v(12.65, 225.27) * mm, "end": v(12.65, 224.8) * mm});
            skLineSegment(sketch, "E1101", {"start": v(12.65, 224.8) * mm, "end": v(12.5, 224.5) * mm});
            skLineSegment(sketch, "E1102", {"start": v(12.5, 224.5) * mm, "end": v(12.33, 224.36) * mm});
            skLineSegment(sketch, "E1103", {"start": v(12.33, 224.36) * mm, "end": v(11.89, 224.2) * mm});
            skLineSegment(sketch, "E1104", {"start": v(11.89, 224.2) * mm, "end": v(11.59, 224.2) * mm});
            skLineSegment(sketch, "E1105", {"start": v(11.59, 224.2) * mm, "end": v(11.12, 224.36) * mm});
            skLineSegment(sketch, "E1106", {"start": v(11.12, 224.36) * mm, "end": v(10.83, 224.65) * mm});
            skLineSegment(sketch, "E1107", {"start": v(10.83, 224.65) * mm, "end": v(10.68, 225.1) * mm});
            skLineSegment(sketch, "E1108", {"start": v(10.68, 225.1) * mm, "end": v(10.68, 225.56) * mm});
            skLineSegment(sketch, "E1109", {"start": v(10.68, 225.56) * mm, "end": v(10.83, 226) * mm});
            skLineSegment(sketch, "E1110", {"start": v(10.83, 226) * mm, "end": v(10.97, 226.16) * mm});
            skLineSegment(sketch, "E1111", {"start": v(10.97, 226.16) * mm, "end": v(11.27, 226.32) * mm});
            skLineSegment(sketch, "E1112", {"start": v(13.85, 227.53) * mm, "end": v(13.85, 229.03) * mm});
            skLineSegment(sketch, "E1113", {"start": v(13.85, 229.03) * mm, "end": v(12.5, 229.18) * mm});
            skLineSegment(sketch, "E1114", {"start": v(12.5, 229.18) * mm, "end": v(12.65, 229.03) * mm});
            skLineSegment(sketch, "E1115", {"start": v(12.65, 229.03) * mm, "end": v(12.8, 228.59) * mm});
            skLineSegment(sketch, "E1116", {"start": v(12.8, 228.59) * mm, "end": v(12.8, 228.12) * mm});
            skLineSegment(sketch, "E1117", {"start": v(12.8, 228.12) * mm, "end": v(12.65, 227.68) * mm});
            skLineSegment(sketch, "E1118", {"start": v(12.65, 227.68) * mm, "end": v(12.33, 227.38) * mm});
            skLineSegment(sketch, "E1119", {"start": v(12.33, 227.38) * mm, "end": v(11.89, 227.21) * mm});
            skLineSegment(sketch, "E1120", {"start": v(11.89, 227.21) * mm, "end": v(11.59, 227.21) * mm});
            skLineSegment(sketch, "E1121", {"start": v(11.59, 227.21) * mm, "end": v(11.12, 227.38) * mm});
            skLineSegment(sketch, "E1122", {"start": v(11.12, 227.38) * mm, "end": v(10.83, 227.68) * mm});
            skLineSegment(sketch, "E1123", {"start": v(10.83, 227.68) * mm, "end": v(10.68, 228.12) * mm});
            skLineSegment(sketch, "E1124", {"start": v(10.68, 228.12) * mm, "end": v(10.68, 228.59) * mm});
            skLineSegment(sketch, "E1125", {"start": v(10.68, 228.59) * mm, "end": v(10.83, 229.03) * mm});
            skLineSegment(sketch, "E1126", {"start": v(10.83, 229.03) * mm, "end": v(10.97, 229.18) * mm});
            skLineSegment(sketch, "E1127", {"start": v(10.97, 229.18) * mm, "end": v(11.27, 229.33) * mm});
            skLineSegment(sketch, "E1128", {"start": v(10.97, 230.7) * mm, "end": v(10.83, 230.85) * mm});
            skLineSegment(sketch, "E1129", {"start": v(10.83, 230.85) * mm, "end": v(10.68, 230.7) * mm});
            skLineSegment(sketch, "E1130", {"start": v(10.68, 230.7) * mm, "end": v(10.83, 230.56) * mm});
            skLineSegment(sketch, "E1131", {"start": v(27.19, 251.22) * mm, "end": v(24.16, 252.57) * mm});
            skLineSegment(sketch, "E1132", {"start": v(26.74, 252.13) * mm, "end": v(26.6, 252.42) * mm});
            skLineSegment(sketch, "E1133", {"start": v(26.6, 252.42) * mm, "end": v(26.28, 252.72) * mm});
            skLineSegment(sketch, "E1134", {"start": v(26.28, 252.72) * mm, "end": v(25.83, 252.87) * mm});
            skLineSegment(sketch, "E1135", {"start": v(25.83, 252.87) * mm, "end": v(25.54, 252.87) * mm});
            skLineSegment(sketch, "E1136", {"start": v(25.54, 252.87) * mm, "end": v(25.07, 252.72) * mm});
            skLineSegment(sketch, "E1137", {"start": v(25.07, 252.72) * mm, "end": v(24.78, 252.42) * mm});
            skLineSegment(sketch, "E1138", {"start": v(24.78, 252.42) * mm, "end": v(24.63, 252.13) * mm});
            skLineSegment(sketch, "E1139", {"start": v(24.63, 252.13) * mm, "end": v(24.63, 251.66) * mm});
            skLineSegment(sketch, "E1140", {"start": v(24.63, 251.66) * mm, "end": v(24.78, 251.36) * mm});
            skLineSegment(sketch, "E1141", {"start": v(24.78, 251.36) * mm, "end": v(25.07, 251.07) * mm});
            skLineSegment(sketch, "E1142", {"start": v(25.07, 251.07) * mm, "end": v(25.54, 250.9) * mm});
            skLineSegment(sketch, "E1143", {"start": v(25.54, 250.9) * mm, "end": v(25.83, 250.9) * mm});
            skLineSegment(sketch, "E1144", {"start": v(25.83, 250.9) * mm, "end": v(26.28, 251.07) * mm});
            skLineSegment(sketch, "E1145", {"start": v(26.28, 251.07) * mm, "end": v(26.6, 251.36) * mm});
            skLineSegment(sketch, "E1146", {"start": v(26.6, 251.36) * mm, "end": v(26.74, 251.66) * mm});
            skLineSegment(sketch, "E1147", {"start": v(26.74, 251.66) * mm, "end": v(26.74, 252.13) * mm});
            skLineSegment(sketch, "E1148", {"start": v(26.74, 255.3) * mm, "end": v(26.9, 254.98) * mm});
            skLineSegment(sketch, "E1149", {"start": v(26.9, 254.98) * mm, "end": v(27.34, 254.54) * mm});
            skLineSegment(sketch, "E1150", {"start": v(27.34, 254.54) * mm, "end": v(24.16, 254.54) * mm});
            skLineSegment(sketch, "E1151", {"start": v(27.34, 258.01) * mm, "end": v(27.34, 256.36) * mm});
            skLineSegment(sketch, "E1152", {"start": v(27.34, 256.36) * mm, "end": v(26.13, 257.25) * mm});
            skLineSegment(sketch, "E1153", {"start": v(26.13, 257.25) * mm, "end": v(26.13, 256.8) * mm});
            skLineSegment(sketch, "E1154", {"start": v(26.13, 256.8) * mm, "end": v(25.98, 256.5) * mm});
            skLineSegment(sketch, "E1155", {"start": v(25.98, 256.5) * mm, "end": v(25.83, 256.36) * mm});
            skLineSegment(sketch, "E1156", {"start": v(25.83, 256.36) * mm, "end": v(25.37, 256.2) * mm});
            skLineSegment(sketch, "E1157", {"start": v(25.37, 256.2) * mm, "end": v(25.07, 256.2) * mm});
            skLineSegment(sketch, "E1158", {"start": v(25.07, 256.2) * mm, "end": v(24.63, 256.36) * mm});
            skLineSegment(sketch, "E1159", {"start": v(24.63, 256.36) * mm, "end": v(24.3, 256.66) * mm});
            skLineSegment(sketch, "E1160", {"start": v(24.3, 256.66) * mm, "end": v(24.16, 257.1) * mm});
            skLineSegment(sketch, "E1161", {"start": v(24.16, 257.1) * mm, "end": v(24.16, 257.57) * mm});
            skLineSegment(sketch, "E1162", {"start": v(24.16, 257.57) * mm, "end": v(24.3, 258.01) * mm});
            skLineSegment(sketch, "E1163", {"start": v(24.3, 258.01) * mm, "end": v(24.48, 258.16) * mm});
            skLineSegment(sketch, "E1164", {"start": v(24.48, 258.16) * mm, "end": v(24.78, 258.3) * mm});
            skLineSegment(sketch, "E1165", {"start": v(25.22, 261.33) * mm, "end": v(24.94, 261.31) * mm});
            skLineSegment(sketch, "E1166", {"start": v(24.94, 261.31) * mm, "end": v(24.7, 261.2) * mm});
            skLineSegment(sketch, "E1167", {"start": v(24.7, 261.2) * mm, "end": v(24.48, 261.04) * mm});
            skLineSegment(sketch, "E1168", {"start": v(24.48, 261.04) * mm, "end": v(24.3, 260.8) * mm});
            skLineSegment(sketch, "E1169", {"start": v(24.3, 260.8) * mm, "end": v(24.2, 260.55) * mm});
            skLineSegment(sketch, "E1170", {"start": v(24.2, 260.55) * mm, "end": v(24.16, 260.28) * mm});
            skLineSegment(sketch, "E1171", {"start": v(24.16, 260.28) * mm, "end": v(24.2, 260) * mm});
            skLineSegment(sketch, "E1172", {"start": v(24.2, 260) * mm, "end": v(24.3, 259.75) * mm});
            skLineSegment(sketch, "E1173", {"start": v(24.3, 259.75) * mm, "end": v(24.48, 259.54) * mm});
            skLineSegment(sketch, "E1174", {"start": v(24.48, 259.54) * mm, "end": v(24.7, 259.37) * mm});
            skLineSegment(sketch, "E1175", {"start": v(24.7, 259.37) * mm, "end": v(24.94, 259.26) * mm});
            skLineSegment(sketch, "E1176", {"start": v(24.94, 259.26) * mm, "end": v(25.22, 259.22) * mm});
            skLineSegment(sketch, "E1177", {"start": v(25.22, 259.22) * mm, "end": v(26.28, 259.22) * mm});
            skLineSegment(sketch, "E1178", {"start": v(26.28, 259.22) * mm, "end": v(26.55, 259.26) * mm});
            skLineSegment(sketch, "E1179", {"start": v(26.55, 259.26) * mm, "end": v(26.8, 259.37) * mm});
            skLineSegment(sketch, "E1180", {"start": v(26.8, 259.37) * mm, "end": v(27.04, 259.54) * mm});
            skLineSegment(sketch, "E1181", {"start": v(27.04, 259.54) * mm, "end": v(27.2, 259.75) * mm});
            skLineSegment(sketch, "E1182", {"start": v(27.2, 259.75) * mm, "end": v(27.32, 260) * mm});
            skLineSegment(sketch, "E1183", {"start": v(27.32, 260) * mm, "end": v(27.34, 260.28) * mm});
            skLineSegment(sketch, "E1184", {"start": v(27.34, 260.28) * mm, "end": v(27.32, 260.55) * mm});
            skLineSegment(sketch, "E1185", {"start": v(27.32, 260.55) * mm, "end": v(27.2, 260.8) * mm});
            skLineSegment(sketch, "E1186", {"start": v(27.2, 260.8) * mm, "end": v(27.04, 261.04) * mm});
            skLineSegment(sketch, "E1187", {"start": v(27.04, 261.04) * mm, "end": v(26.8, 261.2) * mm});
            skLineSegment(sketch, "E1188", {"start": v(26.8, 261.2) * mm, "end": v(26.55, 261.31) * mm});
            skLineSegment(sketch, "E1189", {"start": v(26.55, 261.31) * mm, "end": v(26.28, 261.33) * mm});
            skLineSegment(sketch, "E1190", {"start": v(26.28, 261.33) * mm, "end": v(25.22, 261.33) * mm});
            skLineSegment(sketch, "E1191", {"start": v(24.48, 262.71) * mm, "end": v(24.3, 262.86) * mm});
            skLineSegment(sketch, "E1192", {"start": v(24.3, 262.86) * mm, "end": v(24.16, 262.71) * mm});
            skLineSegment(sketch, "E1193", {"start": v(24.16, 262.71) * mm, "end": v(24.3, 262.54) * mm});
            skLineSegment(sketch, "E1194", {"start": v(26.74, 265.27) * mm, "end": v(26.9, 264.97) * mm});
            skLineSegment(sketch, "E1195", {"start": v(26.9, 264.97) * mm, "end": v(27.34, 264.5) * mm});
            skLineSegment(sketch, "E1196", {"start": v(27.34, 264.5) * mm, "end": v(24.16, 264.5) * mm});
            skLineSegment(sketch, "E1197", {"start": v(23.53, 214.07) * mm, "end": v(24.25, 214.11) * mm});
            skLineSegment(sketch, "E1198", {"start": v(24.25, 214.11) * mm, "end": v(24.94, 214.22) * mm});
            skLineSegment(sketch, "E1199", {"start": v(24.94, 214.22) * mm, "end": v(25.62, 214.4) * mm});
            skLineSegment(sketch, "E1200", {"start": v(25.62, 214.4) * mm, "end": v(26.28, 214.68) * mm});
            skLineSegment(sketch, "E1201", {"start": v(26.28, 214.68) * mm, "end": v(26.91, 215.04) * mm});
            skLineSegment(sketch, "E1202", {"start": v(26.91, 215.04) * mm, "end": v(27.48, 215.44) * mm});
            skLineSegment(sketch, "E1203", {"start": v(27.48, 215.44) * mm, "end": v(28.01, 215.93) * mm});
            skLineSegment(sketch, "E1204", {"start": v(28.01, 215.93) * mm, "end": v(28.5, 216.46) * mm});
            skLineSegment(sketch, "E1205", {"start": v(28.5, 216.46) * mm, "end": v(28.9, 217.03) * mm});
            skLineSegment(sketch, "E1206", {"start": v(28.9, 217.03) * mm, "end": v(29.24, 217.65) * mm});
            skLineSegment(sketch, "E1207", {"start": v(29.24, 217.65) * mm, "end": v(29.52, 218.32) * mm});
            skLineSegment(sketch, "E1208", {"start": v(29.52, 218.32) * mm, "end": v(29.73, 219) * mm});
            skLineSegment(sketch, "E1209", {"start": v(29.73, 219) * mm, "end": v(29.83, 219.7) * mm});
            skLineSegment(sketch, "E1210", {"start": v(29.83, 219.7) * mm, "end": v(29.88, 220.42) * mm});
            skLineSegment(sketch, "E1211", {"start": v(29.88, 220.42) * mm, "end": v(29.83, 221.12) * mm});
            skLineSegment(sketch, "E1212", {"start": v(29.83, 221.12) * mm, "end": v(29.73, 221.82) * mm});
            skLineSegment(sketch, "E1213", {"start": v(29.73, 221.82) * mm, "end": v(29.52, 222.51) * mm});
            skLineSegment(sketch, "E1214", {"start": v(29.52, 222.51) * mm, "end": v(29.24, 223.17) * mm});
            skLineSegment(sketch, "E1215", {"start": v(29.24, 223.17) * mm, "end": v(28.9, 223.78) * mm});
            skLineSegment(sketch, "E1216", {"start": v(28.9, 223.78) * mm, "end": v(28.5, 224.38) * mm});
            skLineSegment(sketch, "E1217", {"start": v(28.5, 224.38) * mm, "end": v(28.01, 224.9) * mm});
            skLineSegment(sketch, "E1218", {"start": v(28.01, 224.9) * mm, "end": v(27.48, 225.37) * mm});
            skLineSegment(sketch, "E1219", {"start": v(27.48, 225.37) * mm, "end": v(26.91, 225.8) * mm});
            skLineSegment(sketch, "E1220", {"start": v(26.91, 225.8) * mm, "end": v(26.28, 226.13) * mm});
            skLineSegment(sketch, "E1221", {"start": v(26.28, 226.13) * mm, "end": v(25.62, 226.4) * mm});
            skLineSegment(sketch, "E1222", {"start": v(25.62, 226.4) * mm, "end": v(24.94, 226.6) * mm});
            skLineSegment(sketch, "E1223", {"start": v(24.94, 226.6) * mm, "end": v(24.25, 226.73) * mm});
            skLineSegment(sketch, "E1224", {"start": v(24.25, 226.73) * mm, "end": v(23.53, 226.77) * mm});
            skLineSegment(sketch, "E1225", {"start": v(23.53, 226.77) * mm, "end": v(22.83, 226.73) * mm});
            skLineSegment(sketch, "E1226", {"start": v(22.83, 226.73) * mm, "end": v(22.1, 226.6) * mm});
            skLineSegment(sketch, "E1227", {"start": v(22.1, 226.6) * mm, "end": v(21.43, 226.4) * mm});
            skLineSegment(sketch, "E1228", {"start": v(21.43, 226.4) * mm, "end": v(20.78, 226.13) * mm});
            skLineSegment(sketch, "E1229", {"start": v(20.78, 226.13) * mm, "end": v(20.14, 225.8) * mm});
            skLineSegment(sketch, "E1230", {"start": v(20.14, 225.8) * mm, "end": v(19.57, 225.37) * mm});
            skLineSegment(sketch, "E1231", {"start": v(19.57, 225.37) * mm, "end": v(19.04, 224.9) * mm});
            skLineSegment(sketch, "E1232", {"start": v(19.04, 224.9) * mm, "end": v(18.57, 224.38) * mm});
            skLineSegment(sketch, "E1233", {"start": v(18.57, 224.38) * mm, "end": v(18.15, 223.78) * mm});
            skLineSegment(sketch, "E1234", {"start": v(18.15, 223.78) * mm, "end": v(17.81, 223.17) * mm});
            skLineSegment(sketch, "E1235", {"start": v(17.81, 223.17) * mm, "end": v(17.54, 222.51) * mm});
            skLineSegment(sketch, "E1236", {"start": v(17.54, 222.51) * mm, "end": v(17.35, 221.82) * mm});
            skLineSegment(sketch, "E1237", {"start": v(17.35, 221.82) * mm, "end": v(17.22, 221.12) * mm});
            skLineSegment(sketch, "E1238", {"start": v(17.22, 221.12) * mm, "end": v(17.18, 220.42) * mm});
            skLineSegment(sketch, "E1239", {"start": v(17.18, 220.42) * mm, "end": v(17.22, 219.7) * mm});
            skLineSegment(sketch, "E1240", {"start": v(17.22, 219.7) * mm, "end": v(17.35, 219) * mm});
            skLineSegment(sketch, "E1241", {"start": v(17.35, 219) * mm, "end": v(17.54, 218.32) * mm});
            skLineSegment(sketch, "E1242", {"start": v(17.54, 218.32) * mm, "end": v(17.81, 217.65) * mm});
            skLineSegment(sketch, "E1243", {"start": v(17.81, 217.65) * mm, "end": v(18.15, 217.03) * mm});
            skLineSegment(sketch, "E1244", {"start": v(18.15, 217.03) * mm, "end": v(18.57, 216.46) * mm});
            skLineSegment(sketch, "E1245", {"start": v(18.57, 216.46) * mm, "end": v(19.04, 215.93) * mm});
            skLineSegment(sketch, "E1246", {"start": v(19.04, 215.93) * mm, "end": v(19.57, 215.44) * mm});
            skLineSegment(sketch, "E1247", {"start": v(19.57, 215.44) * mm, "end": v(20.14, 215.04) * mm});
            skLineSegment(sketch, "E1248", {"start": v(20.14, 215.04) * mm, "end": v(20.78, 214.68) * mm});
            skLineSegment(sketch, "E1249", {"start": v(20.78, 214.68) * mm, "end": v(21.43, 214.4) * mm});
            skLineSegment(sketch, "E1250", {"start": v(21.43, 214.4) * mm, "end": v(22.1, 214.22) * mm});
            skLineSegment(sketch, "E1251", {"start": v(22.1, 214.22) * mm, "end": v(22.83, 214.11) * mm});
            skLineSegment(sketch, "E1252", {"start": v(22.83, 214.11) * mm, "end": v(23.53, 214.07) * mm});
            skLineSegment(sketch, "E1253", {"start": v(78.24, 224.2) * mm, "end": v(75.22, 225.56) * mm});
            skLineSegment(sketch, "E1254", {"start": v(77.8, 225.12) * mm, "end": v(77.65, 225.41) * mm});
            skLineSegment(sketch, "E1255", {"start": v(77.65, 225.41) * mm, "end": v(77.33, 225.71) * mm});
            skLineSegment(sketch, "E1256", {"start": v(77.33, 225.71) * mm, "end": v(76.89, 225.86) * mm});
            skLineSegment(sketch, "E1257", {"start": v(76.89, 225.86) * mm, "end": v(76.6, 225.86) * mm});
            skLineSegment(sketch, "E1258", {"start": v(76.6, 225.86) * mm, "end": v(76.13, 225.71) * mm});
            skLineSegment(sketch, "E1259", {"start": v(76.13, 225.71) * mm, "end": v(75.83, 225.41) * mm});
            skLineSegment(sketch, "E1260", {"start": v(75.83, 225.41) * mm, "end": v(75.68, 225.12) * mm});
            skLineSegment(sketch, "E1261", {"start": v(75.68, 225.12) * mm, "end": v(75.68, 224.65) * mm});
            skLineSegment(sketch, "E1262", {"start": v(75.68, 224.65) * mm, "end": v(75.83, 224.36) * mm});
            skLineSegment(sketch, "E1263", {"start": v(75.83, 224.36) * mm, "end": v(76.13, 224.06) * mm});
            skLineSegment(sketch, "E1264", {"start": v(76.13, 224.06) * mm, "end": v(76.6, 223.9) * mm});
            skLineSegment(sketch, "E1265", {"start": v(76.6, 223.9) * mm, "end": v(76.89, 223.9) * mm});
            skLineSegment(sketch, "E1266", {"start": v(76.89, 223.9) * mm, "end": v(77.33, 224.06) * mm});
            skLineSegment(sketch, "E1267", {"start": v(77.33, 224.06) * mm, "end": v(77.65, 224.36) * mm});
            skLineSegment(sketch, "E1268", {"start": v(77.65, 224.36) * mm, "end": v(77.8, 224.65) * mm});
            skLineSegment(sketch, "E1269", {"start": v(77.8, 224.65) * mm, "end": v(77.8, 225.12) * mm});
            skLineSegment(sketch, "E1270", {"start": v(77.8, 228.3) * mm, "end": v(77.95, 227.98) * mm});
            skLineSegment(sketch, "E1271", {"start": v(77.95, 227.98) * mm, "end": v(78.4, 227.53) * mm});
            skLineSegment(sketch, "E1272", {"start": v(78.4, 227.53) * mm, "end": v(75.22, 227.53) * mm});
            skLineSegment(sketch, "E1273", {"start": v(78.4, 231) * mm, "end": v(78.4, 229.35) * mm});
            skLineSegment(sketch, "E1274", {"start": v(78.4, 229.35) * mm, "end": v(77.18, 230.24) * mm});
            skLineSegment(sketch, "E1275", {"start": v(77.18, 230.24) * mm, "end": v(77.18, 229.8) * mm});
            skLineSegment(sketch, "E1276", {"start": v(77.18, 229.8) * mm, "end": v(77.04, 229.5) * mm});
            skLineSegment(sketch, "E1277", {"start": v(77.04, 229.5) * mm, "end": v(76.89, 229.35) * mm});
            skLineSegment(sketch, "E1278", {"start": v(76.89, 229.35) * mm, "end": v(76.44, 229.18) * mm});
            skLineSegment(sketch, "E1279", {"start": v(76.44, 229.18) * mm, "end": v(76.13, 229.18) * mm});
            skLineSegment(sketch, "E1280", {"start": v(76.13, 229.18) * mm, "end": v(75.68, 229.35) * mm});
            skLineSegment(sketch, "E1281", {"start": v(75.68, 229.35) * mm, "end": v(75.39, 229.65) * mm});
            skLineSegment(sketch, "E1282", {"start": v(75.39, 229.65) * mm, "end": v(75.22, 230.1) * mm});
            skLineSegment(sketch, "E1283", {"start": v(75.22, 230.1) * mm, "end": v(75.22, 230.56) * mm});
            skLineSegment(sketch, "E1284", {"start": v(75.22, 230.56) * mm, "end": v(75.39, 231) * mm});
            skLineSegment(sketch, "E1285", {"start": v(75.39, 231) * mm, "end": v(75.53, 231.15) * mm});
            skLineSegment(sketch, "E1286", {"start": v(75.53, 231.15) * mm, "end": v(75.83, 231.3) * mm});
            skLineSegment(sketch, "E1287", {"start": v(76.27, 234.33) * mm, "end": v(76, 234.3) * mm});
            skLineSegment(sketch, "E1288", {"start": v(76, 234.3) * mm, "end": v(75.74, 234.2) * mm});
            skLineSegment(sketch, "E1289", {"start": v(75.74, 234.2) * mm, "end": v(75.53, 234.03) * mm});
            skLineSegment(sketch, "E1290", {"start": v(75.53, 234.03) * mm, "end": v(75.36, 233.8) * mm});
            skLineSegment(sketch, "E1291", {"start": v(75.36, 233.8) * mm, "end": v(75.26, 233.54) * mm});
            skLineSegment(sketch, "E1292", {"start": v(75.26, 233.54) * mm, "end": v(75.22, 233.27) * mm});
            skLineSegment(sketch, "E1293", {"start": v(75.22, 233.27) * mm, "end": v(75.26, 233) * mm});
            skLineSegment(sketch, "E1294", {"start": v(75.26, 233) * mm, "end": v(75.36, 232.74) * mm});
            skLineSegment(sketch, "E1295", {"start": v(75.36, 232.74) * mm, "end": v(75.53, 232.53) * mm});
            skLineSegment(sketch, "E1296", {"start": v(75.53, 232.53) * mm, "end": v(75.74, 232.36) * mm});
            skLineSegment(sketch, "E1297", {"start": v(75.74, 232.36) * mm, "end": v(76, 232.25) * mm});
            skLineSegment(sketch, "E1298", {"start": v(76, 232.25) * mm, "end": v(76.27, 232.2) * mm});
            skLineSegment(sketch, "E1299", {"start": v(76.27, 232.2) * mm, "end": v(77.33, 232.2) * mm});
            skLineSegment(sketch, "E1300", {"start": v(77.33, 232.2) * mm, "end": v(77.6, 232.25) * mm});
            skLineSegment(sketch, "E1301", {"start": v(77.6, 232.25) * mm, "end": v(77.86, 232.36) * mm});
            skLineSegment(sketch, "E1302", {"start": v(77.86, 232.36) * mm, "end": v(78.1, 232.53) * mm});
            skLineSegment(sketch, "E1303", {"start": v(78.1, 232.53) * mm, "end": v(78.26, 232.74) * mm});
            skLineSegment(sketch, "E1304", {"start": v(78.26, 232.74) * mm, "end": v(78.37, 233) * mm});
            skLineSegment(sketch, "E1305", {"start": v(78.37, 233) * mm, "end": v(78.4, 233.27) * mm});
            skLineSegment(sketch, "E1306", {"start": v(78.4, 233.27) * mm, "end": v(78.37, 233.54) * mm});
            skLineSegment(sketch, "E1307", {"start": v(78.37, 233.54) * mm, "end": v(78.26, 233.8) * mm});
            skLineSegment(sketch, "E1308", {"start": v(78.26, 233.8) * mm, "end": v(78.1, 234.03) * mm});
            skLineSegment(sketch, "E1309", {"start": v(78.1, 234.03) * mm, "end": v(77.86, 234.2) * mm});
            skLineSegment(sketch, "E1310", {"start": v(77.86, 234.2) * mm, "end": v(77.6, 234.3) * mm});
            skLineSegment(sketch, "E1311", {"start": v(77.6, 234.3) * mm, "end": v(77.33, 234.33) * mm});
            skLineSegment(sketch, "E1312", {"start": v(77.33, 234.33) * mm, "end": v(76.27, 234.33) * mm});
            skLineSegment(sketch, "E1313", {"start": v(75.53, 235.7) * mm, "end": v(75.36, 235.85) * mm});
            skLineSegment(sketch, "E1314", {"start": v(75.36, 235.85) * mm, "end": v(75.22, 235.7) * mm});
            skLineSegment(sketch, "E1315", {"start": v(75.22, 235.7) * mm, "end": v(75.36, 235.53) * mm});
            skLineSegment(sketch, "E1316", {"start": v(77.8, 238.26) * mm, "end": v(77.95, 237.97) * mm});
            skLineSegment(sketch, "E1317", {"start": v(77.95, 237.97) * mm, "end": v(78.4, 237.5) * mm});
            skLineSegment(sketch, "E1318", {"start": v(78.4, 237.5) * mm, "end": v(75.22, 237.5) * mm});
            skLineSegment(sketch, "E1319", {"start": v(80.63, 196.16) * mm, "end": v(81.7, 196.2) * mm});
            skLineSegment(sketch, "E1320", {"start": v(81.7, 196.2) * mm, "end": v(82.73, 196.33) * mm});
            skLineSegment(sketch, "E1321", {"start": v(82.73, 196.33) * mm, "end": v(83.75, 196.56) * mm});
            skLineSegment(sketch, "E1322", {"start": v(83.75, 196.56) * mm, "end": v(84.76, 196.86) * mm});
            skLineSegment(sketch, "E1323", {"start": v(84.76, 196.86) * mm, "end": v(85.74, 197.24) * mm});
            skLineSegment(sketch, "E1324", {"start": v(85.74, 197.24) * mm, "end": v(86.69, 197.7) * mm});
            skLineSegment(sketch, "E1325", {"start": v(86.69, 197.7) * mm, "end": v(87.58, 198.24) * mm});
            skLineSegment(sketch, "E1326", {"start": v(87.58, 198.24) * mm, "end": v(88.44, 198.85) * mm});
            skLineSegment(sketch, "E1327", {"start": v(88.44, 198.85) * mm, "end": v(89.23, 199.53) * mm});
            skLineSegment(sketch, "E1328", {"start": v(89.23, 199.53) * mm, "end": v(89.97, 200.27) * mm});
            skLineSegment(sketch, "E1329", {"start": v(89.97, 200.27) * mm, "end": v(90.67, 201.07) * mm});
            skLineSegment(sketch, "E1330", {"start": v(90.67, 201.07) * mm, "end": v(91.26, 201.92) * mm});
            skLineSegment(sketch, "E1331", {"start": v(91.26, 201.92) * mm, "end": v(91.81, 202.83) * mm});
            skLineSegment(sketch, "E1332", {"start": v(91.81, 202.83) * mm, "end": v(92.28, 203.76) * mm});
            skLineSegment(sketch, "E1333", {"start": v(92.28, 203.76) * mm, "end": v(92.66, 204.73) * mm});
            skLineSegment(sketch, "E1334", {"start": v(92.66, 204.73) * mm, "end": v(92.95, 205.75) * mm});
            skLineSegment(sketch, "E1335", {"start": v(92.95, 205.75) * mm, "end": v(93.17, 206.77) * mm});
            skLineSegment(sketch, "E1336", {"start": v(93.17, 206.77) * mm, "end": v(93.3, 207.82) * mm});
            skLineSegment(sketch, "E1337", {"start": v(93.3, 207.82) * mm, "end": v(93.33, 208.86) * mm});
            skLineSegment(sketch, "E1338", {"start": v(93.33, 208.86) * mm, "end": v(93.3, 209.92) * mm});
            skLineSegment(sketch, "E1339", {"start": v(93.3, 209.92) * mm, "end": v(93.17, 210.96) * mm});
            skLineSegment(sketch, "E1340", {"start": v(93.17, 210.96) * mm, "end": v(92.95, 211.97) * mm});
            skLineSegment(sketch, "E1341", {"start": v(92.95, 211.97) * mm, "end": v(92.66, 212.99) * mm});
            skLineSegment(sketch, "E1342", {"start": v(92.66, 212.99) * mm, "end": v(92.28, 213.96) * mm});
            skLineSegment(sketch, "E1343", {"start": v(92.28, 213.96) * mm, "end": v(91.81, 214.92) * mm});
            skLineSegment(sketch, "E1344", {"start": v(91.81, 214.92) * mm, "end": v(91.26, 215.8) * mm});
            skLineSegment(sketch, "E1345", {"start": v(91.26, 215.8) * mm, "end": v(90.67, 216.67) * mm});
            skLineSegment(sketch, "E1346", {"start": v(90.67, 216.67) * mm, "end": v(89.97, 217.48) * mm});
            skLineSegment(sketch, "E1347", {"start": v(89.97, 217.48) * mm, "end": v(89.23, 218.22) * mm});
            skLineSegment(sketch, "E1348", {"start": v(89.23, 218.22) * mm, "end": v(88.44, 218.9) * mm});
            skLineSegment(sketch, "E1349", {"start": v(88.44, 218.9) * mm, "end": v(87.58, 219.49) * mm});
            skLineSegment(sketch, "E1350", {"start": v(87.58, 219.49) * mm, "end": v(86.69, 220.04) * mm});
            skLineSegment(sketch, "E1351", {"start": v(86.69, 220.04) * mm, "end": v(85.74, 220.5) * mm});
            skLineSegment(sketch, "E1352", {"start": v(85.74, 220.5) * mm, "end": v(84.76, 220.88) * mm});
            skLineSegment(sketch, "E1353", {"start": v(84.76, 220.88) * mm, "end": v(83.75, 221.18) * mm});
            skLineSegment(sketch, "E1354", {"start": v(83.75, 221.18) * mm, "end": v(82.73, 221.4) * mm});
            skLineSegment(sketch, "E1355", {"start": v(82.73, 221.4) * mm, "end": v(81.7, 221.52) * mm});
            skLineSegment(sketch, "E1356", {"start": v(81.7, 221.52) * mm, "end": v(80.63, 221.56) * mm});
            skLineSegment(sketch, "E1357", {"start": v(80.63, 221.56) * mm, "end": v(79.6, 221.52) * mm});
            skLineSegment(sketch, "E1358", {"start": v(79.6, 221.52) * mm, "end": v(78.54, 221.4) * mm});
            skLineSegment(sketch, "E1359", {"start": v(78.54, 221.4) * mm, "end": v(77.52, 221.18) * mm});
            skLineSegment(sketch, "E1360", {"start": v(77.52, 221.18) * mm, "end": v(76.5, 220.88) * mm});
            skLineSegment(sketch, "E1361", {"start": v(76.5, 220.88) * mm, "end": v(75.53, 220.5) * mm});
            skLineSegment(sketch, "E1362", {"start": v(75.53, 220.5) * mm, "end": v(74.58, 220.04) * mm});
            skLineSegment(sketch, "E1363", {"start": v(74.58, 220.04) * mm, "end": v(73.7, 219.49) * mm});
            skLineSegment(sketch, "E1364", {"start": v(73.7, 219.49) * mm, "end": v(72.85, 218.9) * mm});
            skLineSegment(sketch, "E1365", {"start": v(72.85, 218.9) * mm, "end": v(72.04, 218.22) * mm});
            skLineSegment(sketch, "E1366", {"start": v(72.04, 218.22) * mm, "end": v(71.3, 217.48) * mm});
            skLineSegment(sketch, "E1367", {"start": v(71.3, 217.48) * mm, "end": v(70.62, 216.67) * mm});
            skLineSegment(sketch, "E1368", {"start": v(70.62, 216.67) * mm, "end": v(70, 215.8) * mm});
            skLineSegment(sketch, "E1369", {"start": v(70, 215.8) * mm, "end": v(69.46, 214.92) * mm});
            skLineSegment(sketch, "E1370", {"start": v(69.46, 214.92) * mm, "end": v(69.01, 213.96) * mm});
            skLineSegment(sketch, "E1371", {"start": v(69.01, 213.96) * mm, "end": v(68.63, 212.99) * mm});
            skLineSegment(sketch, "E1372", {"start": v(68.63, 212.99) * mm, "end": v(68.32, 211.97) * mm});
            skLineSegment(sketch, "E1373", {"start": v(68.32, 211.97) * mm, "end": v(68.1, 210.96) * mm});
            skLineSegment(sketch, "E1374", {"start": v(68.1, 210.96) * mm, "end": v(67.98, 209.92) * mm});
            skLineSegment(sketch, "E1375", {"start": v(67.98, 209.92) * mm, "end": v(67.93, 208.86) * mm});
            skLineSegment(sketch, "E1376", {"start": v(67.93, 208.86) * mm, "end": v(67.98, 207.82) * mm});
            skLineSegment(sketch, "E1377", {"start": v(67.98, 207.82) * mm, "end": v(68.1, 206.77) * mm});
            skLineSegment(sketch, "E1378", {"start": v(68.1, 206.77) * mm, "end": v(68.32, 205.75) * mm});
            skLineSegment(sketch, "E1379", {"start": v(68.32, 205.75) * mm, "end": v(68.63, 204.73) * mm});
            skLineSegment(sketch, "E1380", {"start": v(68.63, 204.73) * mm, "end": v(69.01, 203.76) * mm});
            skLineSegment(sketch, "E1381", {"start": v(69.01, 203.76) * mm, "end": v(69.46, 202.83) * mm});
            skLineSegment(sketch, "E1382", {"start": v(69.46, 202.83) * mm, "end": v(70, 201.92) * mm});
            skLineSegment(sketch, "E1383", {"start": v(70, 201.92) * mm, "end": v(70.62, 201.07) * mm});
            skLineSegment(sketch, "E1384", {"start": v(70.62, 201.07) * mm, "end": v(71.3, 200.27) * mm});
            skLineSegment(sketch, "E1385", {"start": v(71.3, 200.27) * mm, "end": v(72.04, 199.53) * mm});
            skLineSegment(sketch, "E1386", {"start": v(72.04, 199.53) * mm, "end": v(72.85, 198.85) * mm});
            skLineSegment(sketch, "E1387", {"start": v(72.85, 198.85) * mm, "end": v(73.7, 198.24) * mm});
            skLineSegment(sketch, "E1388", {"start": v(73.7, 198.24) * mm, "end": v(74.58, 197.7) * mm});
            skLineSegment(sketch, "E1389", {"start": v(74.58, 197.7) * mm, "end": v(75.53, 197.24) * mm});
            skLineSegment(sketch, "E1390", {"start": v(75.53, 197.24) * mm, "end": v(76.5, 196.86) * mm});
            skLineSegment(sketch, "E1391", {"start": v(76.5, 196.86) * mm, "end": v(77.52, 196.56) * mm});
            skLineSegment(sketch, "E1392", {"start": v(77.52, 196.56) * mm, "end": v(78.54, 196.33) * mm});
            skLineSegment(sketch, "E1393", {"start": v(78.54, 196.33) * mm, "end": v(79.6, 196.2) * mm});
            skLineSegment(sketch, "E1394", {"start": v(79.6, 196.2) * mm, "end": v(80.63, 196.16) * mm});
            skLineSegment(sketch, "E1395", {"start": v(119.7, 290.16) * mm, "end": v(119.86, 290.2) * mm});
            skLineSegment(sketch, "E1396", {"start": v(119.86, 290.2) * mm, "end": v(119.96, 290.31) * mm});
            skLineSegment(sketch, "E1397", {"start": v(119.96, 290.31) * mm, "end": v(120, 290.46) * mm});
            skLineSegment(sketch, "E1398", {"start": v(120, 290.46) * mm, "end": v(119.96, 290.6) * mm});
            skLineSegment(sketch, "E1399", {"start": v(119.96, 290.6) * mm, "end": v(119.86, 290.71) * mm});
            skLineSegment(sketch, "E1400", {"start": v(119.86, 290.71) * mm, "end": v(119.7, 290.76) * mm});
            skLineSegment(sketch, "E1401", {"start": v(119.7, 290.76) * mm, "end": v(119.54, 290.71) * mm});
            skLineSegment(sketch, "E1402", {"start": v(119.54, 290.71) * mm, "end": v(119.43, 290.6) * mm});
            skLineSegment(sketch, "E1403", {"start": v(119.43, 290.6) * mm, "end": v(119.4, 290.46) * mm});
            skLineSegment(sketch, "E1404", {"start": v(119.4, 290.46) * mm, "end": v(119.43, 290.31) * mm});
            skLineSegment(sketch, "E1405", {"start": v(119.43, 290.31) * mm, "end": v(119.54, 290.2) * mm});
            skLineSegment(sketch, "E1406", {"start": v(119.54, 290.2) * mm, "end": v(119.7, 290.16) * mm});
            skLineSegment(sketch, "E1407", {"start": v(117.89, 293.78) * mm, "end": v(117.61, 293.76) * mm});
            skLineSegment(sketch, "E1408", {"start": v(117.61, 293.76) * mm, "end": v(117.36, 293.66) * mm});
            skLineSegment(sketch, "E1409", {"start": v(117.36, 293.66) * mm, "end": v(117.15, 293.49) * mm});
            skLineSegment(sketch, "E1410", {"start": v(117.15, 293.49) * mm, "end": v(116.98, 293.25) * mm});
            skLineSegment(sketch, "E1411", {"start": v(116.98, 293.25) * mm, "end": v(116.87, 293) * mm});
            skLineSegment(sketch, "E1412", {"start": v(116.87, 293) * mm, "end": v(116.83, 292.72) * mm});
            skLineSegment(sketch, "E1413", {"start": v(116.83, 292.72) * mm, "end": v(116.87, 292.45) * mm});
            skLineSegment(sketch, "E1414", {"start": v(116.87, 292.45) * mm, "end": v(116.98, 292.2) * mm});
            skLineSegment(sketch, "E1415", {"start": v(116.98, 292.2) * mm, "end": v(117.15, 291.98) * mm});
            skLineSegment(sketch, "E1416", {"start": v(117.15, 291.98) * mm, "end": v(117.36, 291.81) * mm});
            skLineSegment(sketch, "E1417", {"start": v(117.36, 291.81) * mm, "end": v(117.61, 291.7) * mm});
            skLineSegment(sketch, "E1418", {"start": v(117.61, 291.7) * mm, "end": v(117.89, 291.67) * mm});
            skLineSegment(sketch, "E1419", {"start": v(117.89, 291.67) * mm, "end": v(118.95, 291.67) * mm});
            skLineSegment(sketch, "E1420", {"start": v(118.95, 291.67) * mm, "end": v(119.22, 291.7) * mm});
            skLineSegment(sketch, "E1421", {"start": v(119.22, 291.7) * mm, "end": v(119.48, 291.81) * mm});
            skLineSegment(sketch, "E1422", {"start": v(119.48, 291.81) * mm, "end": v(119.69, 291.98) * mm});
            skLineSegment(sketch, "E1423", {"start": v(119.69, 291.98) * mm, "end": v(119.86, 292.2) * mm});
            skLineSegment(sketch, "E1424", {"start": v(119.86, 292.2) * mm, "end": v(119.96, 292.45) * mm});
            skLineSegment(sketch, "E1425", {"start": v(119.96, 292.45) * mm, "end": v(120, 292.72) * mm});
            skLineSegment(sketch, "E1426", {"start": v(120, 292.72) * mm, "end": v(119.96, 293) * mm});
            skLineSegment(sketch, "E1427", {"start": v(119.96, 293) * mm, "end": v(119.86, 293.25) * mm});
            skLineSegment(sketch, "E1428", {"start": v(119.86, 293.25) * mm, "end": v(119.69, 293.49) * mm});
            skLineSegment(sketch, "E1429", {"start": v(119.69, 293.49) * mm, "end": v(119.48, 293.66) * mm});
            skLineSegment(sketch, "E1430", {"start": v(119.48, 293.66) * mm, "end": v(119.22, 293.76) * mm});
            skLineSegment(sketch, "E1431", {"start": v(119.22, 293.76) * mm, "end": v(118.95, 293.78) * mm});
            skLineSegment(sketch, "E1432", {"start": v(118.95, 293.78) * mm, "end": v(117.89, 293.78) * mm});
            skLineSegment(sketch, "E1433", {"start": v(120, 295.3) * mm, "end": v(116.83, 295.3) * mm});
            skLineSegment(sketch, "E1434", {"start": v(120, 295.3) * mm, "end": v(117.89, 296.8) * mm});
            skLineSegment(sketch, "E1435", {"start": v(117.89, 296.8) * mm, "end": v(117.89, 294.54) * mm});
            skLineSegment(sketch, "E1436", {"start": v(147.48, 246.73) * mm, "end": v(156.81, 252.13) * mm});
            skLineSegment(sketch, "E1437", {"start": v(144.73, 245.14) * mm, "end": v(146.1, 245.92) * mm});
            skLineSegment(sketch, "E1438", {"start": v(135.1, 239.57) * mm, "end": v(143.35, 244.34) * mm});
            skLineSegment(sketch, "E1439", {"start": v(132.34, 237.99) * mm, "end": v(133.72, 238.8) * mm});
            skLineSegment(sketch, "E1440", {"start": v(121.61, 231.8) * mm, "end": v(130.97, 237.2) * mm});
            skLineSegment(sketch, "E1441", {"start": v(171.93, 201.94) * mm, "end": v(171.16, 205.56) * mm});
            skLineSegment(sketch, "E1442", {"start": v(171.16, 205.56) * mm, "end": v(170.32, 209.18) * mm});
            skLineSegment(sketch, "E1443", {"start": v(170.32, 209.18) * mm, "end": v(169.39, 212.76) * mm});
            skLineSegment(sketch, "E1444", {"start": v(169.39, 212.76) * mm, "end": v(168.37, 216.33) * mm});
            skLineSegment(sketch, "E1445", {"start": v(168.37, 216.33) * mm, "end": v(167.27, 219.87) * mm});
            skLineSegment(sketch, "E1446", {"start": v(167.27, 219.87) * mm, "end": v(166.1, 223.38) * mm});
            skLineSegment(sketch, "E1447", {"start": v(166.1, 223.38) * mm, "end": v(164.86, 226.87) * mm});
            skLineSegment(sketch, "E1448", {"start": v(164.86, 226.87) * mm, "end": v(163.5, 230.33) * mm});
            skLineSegment(sketch, "E1449", {"start": v(163.5, 230.33) * mm, "end": v(162.1, 233.75) * mm});
            skLineSegment(sketch, "E1450", {"start": v(162.1, 233.75) * mm, "end": v(160.6, 237.14) * mm});
            skLineSegment(sketch, "E1451", {"start": v(160.6, 237.14) * mm, "end": v(159.04, 240.49) * mm});
            skLineSegment(sketch, "E1452", {"start": v(159.04, 240.49) * mm, "end": v(157.38, 243.8) * mm});
            skLineSegment(sketch, "E1453", {"start": v(157.38, 243.8) * mm, "end": v(155.65, 247.09) * mm});
            skLineSegment(sketch, "E1454", {"start": v(155.65, 247.09) * mm, "end": v(153.85, 250.33) * mm});
            skLineSegment(sketch, "E1455", {"start": v(153.85, 250.33) * mm, "end": v(151.97, 253.52) * mm});
            skLineSegment(sketch, "E1456", {"start": v(151.97, 253.52) * mm, "end": v(150.02, 256.68) * mm});
            skLineSegment(sketch, "E1457", {"start": v(150.02, 256.68) * mm, "end": v(148, 259.77) * mm});
            skLineSegment(sketch, "E1458", {"start": v(148, 259.77) * mm, "end": v(145.91, 262.84) * mm});
            skLineSegment(sketch, "E1459", {"start": v(145.91, 262.84) * mm, "end": v(143.75, 265.84) * mm});
            skLineSegment(sketch, "E1460", {"start": v(143.75, 265.84) * mm, "end": v(141.5, 268.8) * mm});
            skLineSegment(sketch, "E1461", {"start": v(141.5, 268.8) * mm, "end": v(139.22, 271.7) * mm});
            skLineSegment(sketch, "E1462", {"start": v(139.22, 271.7) * mm, "end": v(136.85, 274.56) * mm});
            skLineSegment(sketch, "E1463", {"start": v(136.85, 274.56) * mm, "end": v(134.42, 277.36) * mm});
            skLineSegment(sketch, "E1464", {"start": v(134.42, 277.36) * mm, "end": v(131.92, 280.09) * mm});
            skLineSegment(sketch, "E1465", {"start": v(131.92, 280.09) * mm, "end": v(129.36, 282.78) * mm});
            skLineSegment(sketch, "E1466", {"start": v(129.36, 282.78) * mm, "end": v(126.76, 285.4) * mm});
            skLineSegment(sketch, "E1467", {"start": v(126.76, 285.4) * mm, "end": v(124.07, 287.96) * mm});
            skLineSegment(sketch, "E1468", {"start": v(124.07, 287.96) * mm, "end": v(121.34, 290.46) * mm});
            skLineSegment(sketch, "E1469", {"start": v(14.64, 81.86) * mm, "end": v(15.7, 81.9) * mm});
            skLineSegment(sketch, "E1470", {"start": v(15.7, 81.9) * mm, "end": v(16.73, 82.03) * mm});
            skLineSegment(sketch, "E1471", {"start": v(16.73, 82.03) * mm, "end": v(17.77, 82.26) * mm});
            skLineSegment(sketch, "E1472", {"start": v(17.77, 82.26) * mm, "end": v(18.76, 82.56) * mm});
            skLineSegment(sketch, "E1473", {"start": v(18.76, 82.56) * mm, "end": v(19.74, 82.94) * mm});
            skLineSegment(sketch, "E1474", {"start": v(19.74, 82.94) * mm, "end": v(20.7, 83.4) * mm});
            skLineSegment(sketch, "E1475", {"start": v(20.7, 83.4) * mm, "end": v(21.6, 83.94) * mm});
            skLineSegment(sketch, "E1476", {"start": v(21.6, 83.94) * mm, "end": v(22.45, 84.55) * mm});
            skLineSegment(sketch, "E1477", {"start": v(22.45, 84.55) * mm, "end": v(23.25, 85.23) * mm});
            skLineSegment(sketch, "E1478", {"start": v(23.25, 85.23) * mm, "end": v(24, 85.97) * mm});
            skLineSegment(sketch, "E1479", {"start": v(24, 85.97) * mm, "end": v(24.67, 86.77) * mm});
            skLineSegment(sketch, "E1480", {"start": v(24.67, 86.77) * mm, "end": v(25.28, 87.62) * mm});
            skLineSegment(sketch, "E1481", {"start": v(25.28, 87.62) * mm, "end": v(25.81, 88.53) * mm});
            skLineSegment(sketch, "E1482", {"start": v(25.81, 88.53) * mm, "end": v(26.28, 89.46) * mm});
            skLineSegment(sketch, "E1483", {"start": v(26.28, 89.46) * mm, "end": v(26.66, 90.43) * mm});
            skLineSegment(sketch, "E1484", {"start": v(26.66, 90.43) * mm, "end": v(26.96, 91.45) * mm});
            skLineSegment(sketch, "E1485", {"start": v(26.96, 91.45) * mm, "end": v(27.17, 92.47) * mm});
            skLineSegment(sketch, "E1486", {"start": v(27.17, 92.47) * mm, "end": v(27.3, 93.52) * mm});
            skLineSegment(sketch, "E1487", {"start": v(27.3, 93.52) * mm, "end": v(27.34, 94.56) * mm});
            skLineSegment(sketch, "E1488", {"start": v(27.34, 94.56) * mm, "end": v(27.3, 95.62) * mm});
            skLineSegment(sketch, "E1489", {"start": v(27.3, 95.62) * mm, "end": v(27.17, 96.66) * mm});
            skLineSegment(sketch, "E1490", {"start": v(27.17, 96.66) * mm, "end": v(26.96, 97.67) * mm});
            skLineSegment(sketch, "E1491", {"start": v(26.96, 97.67) * mm, "end": v(26.66, 98.69) * mm});
            skLineSegment(sketch, "E1492", {"start": v(26.66, 98.69) * mm, "end": v(26.28, 99.66) * mm});
            skLineSegment(sketch, "E1493", {"start": v(26.28, 99.66) * mm, "end": v(25.81, 100.62) * mm});
            skLineSegment(sketch, "E1494", {"start": v(25.81, 100.62) * mm, "end": v(25.28, 101.5) * mm});
            skLineSegment(sketch, "E1495", {"start": v(25.28, 101.5) * mm, "end": v(24.67, 102.37) * mm});
            skLineSegment(sketch, "E1496", {"start": v(24.67, 102.37) * mm, "end": v(24, 103.18) * mm});
            skLineSegment(sketch, "E1497", {"start": v(24, 103.18) * mm, "end": v(23.25, 103.92) * mm});
            skLineSegment(sketch, "E1498", {"start": v(23.25, 103.92) * mm, "end": v(22.45, 104.6) * mm});
            skLineSegment(sketch, "E1499", {"start": v(22.45, 104.6) * mm, "end": v(21.6, 105.19) * mm});
            skLineSegment(sketch, "E1500", {"start": v(21.6, 105.19) * mm, "end": v(20.7, 105.74) * mm});
            skLineSegment(sketch, "E1501", {"start": v(20.7, 105.74) * mm, "end": v(19.74, 106.2) * mm});
            skLineSegment(sketch, "E1502", {"start": v(19.74, 106.2) * mm, "end": v(18.76, 106.58) * mm});
            skLineSegment(sketch, "E1503", {"start": v(18.76, 106.58) * mm, "end": v(17.77, 106.88) * mm});
            skLineSegment(sketch, "E1504", {"start": v(17.77, 106.88) * mm, "end": v(16.73, 107.1) * mm});
            skLineSegment(sketch, "E1505", {"start": v(16.73, 107.1) * mm, "end": v(15.7, 107.22) * mm});
            skLineSegment(sketch, "E1506", {"start": v(15.7, 107.22) * mm, "end": v(14.64, 107.26) * mm});
            skLineSegment(sketch, "E1507", {"start": v(14.64, 107.26) * mm, "end": v(13.6, 107.22) * mm});
            skLineSegment(sketch, "E1508", {"start": v(13.6, 107.22) * mm, "end": v(12.56, 107.1) * mm});
            skLineSegment(sketch, "E1509", {"start": v(12.56, 107.1) * mm, "end": v(11.53, 106.88) * mm});
            skLineSegment(sketch, "E1510", {"start": v(11.53, 106.88) * mm, "end": v(10.53, 106.58) * mm});
            skLineSegment(sketch, "E1511", {"start": v(10.53, 106.58) * mm, "end": v(9.54, 106.2) * mm});
            skLineSegment(sketch, "E1512", {"start": v(9.54, 106.2) * mm, "end": v(8.6, 105.74) * mm});
            skLineSegment(sketch, "E1513", {"start": v(8.6, 105.74) * mm, "end": v(7.7, 105.19) * mm});
            skLineSegment(sketch, "E1514", {"start": v(7.7, 105.19) * mm, "end": v(6.85, 104.6) * mm});
            skLineSegment(sketch, "E1515", {"start": v(6.85, 104.6) * mm, "end": v(6.04, 103.92) * mm});
            skLineSegment(sketch, "E1516", {"start": v(6.04, 103.92) * mm, "end": v(5.3, 103.18) * mm});
            skLineSegment(sketch, "E1517", {"start": v(5.3, 103.18) * mm, "end": v(4.62, 102.37) * mm});
            skLineSegment(sketch, "E1518", {"start": v(4.62, 102.37) * mm, "end": v(4.01, 101.5) * mm});
            skLineSegment(sketch, "E1519", {"start": v(4.01, 101.5) * mm, "end": v(3.48, 100.62) * mm});
            skLineSegment(sketch, "E1520", {"start": v(3.48, 100.62) * mm, "end": v(3.02, 99.66) * mm});
            skLineSegment(sketch, "E1521", {"start": v(3.02, 99.66) * mm, "end": v(2.64, 98.69) * mm});
            skLineSegment(sketch, "E1522", {"start": v(2.64, 98.69) * mm, "end": v(2.34, 97.67) * mm});
            skLineSegment(sketch, "E1523", {"start": v(2.34, 97.67) * mm, "end": v(2.13, 96.66) * mm});
            skLineSegment(sketch, "E1524", {"start": v(2.13, 96.66) * mm, "end": v(1.98, 95.62) * mm});
            skLineSegment(sketch, "E1525", {"start": v(1.98, 95.62) * mm, "end": v(1.94, 94.56) * mm});
            skLineSegment(sketch, "E1526", {"start": v(1.94, 94.56) * mm, "end": v(1.98, 93.52) * mm});
            skLineSegment(sketch, "E1527", {"start": v(1.98, 93.52) * mm, "end": v(2.13, 92.47) * mm});
            skLineSegment(sketch, "E1528", {"start": v(2.13, 92.47) * mm, "end": v(2.34, 91.45) * mm});
            skLineSegment(sketch, "E1529", {"start": v(2.34, 91.45) * mm, "end": v(2.64, 90.43) * mm});
            skLineSegment(sketch, "E1530", {"start": v(2.64, 90.43) * mm, "end": v(3.02, 89.46) * mm});
            skLineSegment(sketch, "E1531", {"start": v(3.02, 89.46) * mm, "end": v(3.48, 88.53) * mm});
            skLineSegment(sketch, "E1532", {"start": v(3.48, 88.53) * mm, "end": v(4.01, 87.62) * mm});
            skLineSegment(sketch, "E1533", {"start": v(4.01, 87.62) * mm, "end": v(4.62, 86.77) * mm});
            skLineSegment(sketch, "E1534", {"start": v(4.62, 86.77) * mm, "end": v(5.3, 85.97) * mm});
            skLineSegment(sketch, "E1535", {"start": v(5.3, 85.97) * mm, "end": v(6.04, 85.23) * mm});
            skLineSegment(sketch, "E1536", {"start": v(6.04, 85.23) * mm, "end": v(6.85, 84.55) * mm});
            skLineSegment(sketch, "E1537", {"start": v(6.85, 84.55) * mm, "end": v(7.7, 83.94) * mm});
            skLineSegment(sketch, "E1538", {"start": v(7.7, 83.94) * mm, "end": v(8.6, 83.4) * mm});
            skLineSegment(sketch, "E1539", {"start": v(8.6, 83.4) * mm, "end": v(9.54, 82.94) * mm});
            skLineSegment(sketch, "E1540", {"start": v(9.54, 82.94) * mm, "end": v(10.53, 82.56) * mm});
            skLineSegment(sketch, "E1541", {"start": v(10.53, 82.56) * mm, "end": v(11.53, 82.26) * mm});
            skLineSegment(sketch, "E1542", {"start": v(11.53, 82.26) * mm, "end": v(12.56, 82.03) * mm});
            skLineSegment(sketch, "E1543", {"start": v(12.56, 82.03) * mm, "end": v(13.6, 81.9) * mm});
            skLineSegment(sketch, "E1544", {"start": v(13.6, 81.9) * mm, "end": v(14.64, 81.86) * mm});
            skLineSegment(sketch, "E1545", {"start": v(-106.01, 56.46) * mm, "end": v(-144.11, 56.46) * mm});
            skLineSegment(sketch, "E1546", {"start": v(-106.01, 78.69) * mm, "end": v(-144.11, 78.69) * mm});
            skLineSegment(sketch, "E1547", {"start": v(-106.01, 129.49) * mm, "end": v(-144.11, 129.49) * mm});
            skLineSegment(sketch, "E1548", {"start": v(-79.03, 107.26) * mm, "end": v(-128.24, 107.26) * mm});
            skLineSegment(sketch, "E1549", {"start": v(-55.21, 86.62) * mm, "end": v(-4.41, 86.62) * mm});
            skLineSegment(sketch, "E1550", {"start": v(-99.66, 65.99) * mm, "end": v(-99.66, -13.39) * mm});
            skLineSegment(sketch, "E1551", {"start": v(-135.71, 61.7) * mm, "end": v(-135.86, 61.84) * mm});
            skLineSegment(sketch, "E1552", {"start": v(-135.86, 61.84) * mm, "end": v(-135.71, 61.99) * mm});
            skLineSegment(sketch, "E1553", {"start": v(-135.71, 61.99) * mm, "end": v(-135.56, 61.84) * mm});
            skLineSegment(sketch, "E1554", {"start": v(-135.56, 61.84) * mm, "end": v(-135.71, 61.7) * mm});
            skLineSegment(sketch, "E1555", {"start": v(-135.71, 61.7) * mm, "end": v(-136, 61.7) * mm});
            skLineSegment(sketch, "E1556", {"start": v(-136, 61.7) * mm, "end": v(-136.32, 61.84) * mm});
            skLineSegment(sketch, "E1557", {"start": v(-136.32, 61.84) * mm, "end": v(-136.47, 61.99) * mm});
            skLineSegment(sketch, "E1558", {"start": v(-135.71, 62.58) * mm, "end": v(-135.86, 62.75) * mm});
            skLineSegment(sketch, "E1559", {"start": v(-135.86, 62.75) * mm, "end": v(-135.71, 62.9) * mm});
            skLineSegment(sketch, "E1560", {"start": v(-135.71, 62.9) * mm, "end": v(-135.56, 62.75) * mm});
            skLineSegment(sketch, "E1561", {"start": v(-135.56, 62.75) * mm, "end": v(-135.71, 62.58) * mm});
            skLineSegment(sketch, "E1562", {"start": v(-135.71, 62.58) * mm, "end": v(-136, 62.58) * mm});
            skLineSegment(sketch, "E1563", {"start": v(-136, 62.58) * mm, "end": v(-136.32, 62.75) * mm});
            skLineSegment(sketch, "E1564", {"start": v(-136.32, 62.75) * mm, "end": v(-136.47, 62.9) * mm});
            skLineSegment(sketch, "E1565", {"start": v(-136.18, 64.1) * mm, "end": v(-136.18, 65.6) * mm});
            skLineSegment(sketch, "E1566", {"start": v(-136.18, 65.6) * mm, "end": v(-137.53, 65.75) * mm});
            skLineSegment(sketch, "E1567", {"start": v(-137.53, 65.75) * mm, "end": v(-137.38, 65.6) * mm});
            skLineSegment(sketch, "E1568", {"start": v(-137.38, 65.6) * mm, "end": v(-137.23, 65.16) * mm});
            skLineSegment(sketch, "E1569", {"start": v(-137.23, 65.16) * mm, "end": v(-137.23, 64.7) * mm});
            skLineSegment(sketch, "E1570", {"start": v(-137.23, 64.7) * mm, "end": v(-137.38, 64.25) * mm});
            skLineSegment(sketch, "E1571", {"start": v(-137.38, 64.25) * mm, "end": v(-137.68, 63.96) * mm});
            skLineSegment(sketch, "E1572", {"start": v(-137.68, 63.96) * mm, "end": v(-138.12, 63.8) * mm});
            skLineSegment(sketch, "E1573", {"start": v(-138.12, 63.8) * mm, "end": v(-138.44, 63.8) * mm});
            skLineSegment(sketch, "E1574", {"start": v(-138.44, 63.8) * mm, "end": v(-138.89, 63.96) * mm});
            skLineSegment(sketch, "E1575", {"start": v(-138.89, 63.96) * mm, "end": v(-139.18, 64.25) * mm});
            skLineSegment(sketch, "E1576", {"start": v(-139.18, 64.25) * mm, "end": v(-139.35, 64.7) * mm});
            skLineSegment(sketch, "E1577", {"start": v(-139.35, 64.7) * mm, "end": v(-139.35, 65.16) * mm});
            skLineSegment(sketch, "E1578", {"start": v(-139.35, 65.16) * mm, "end": v(-139.18, 65.6) * mm});
            skLineSegment(sketch, "E1579", {"start": v(-139.18, 65.6) * mm, "end": v(-139.03, 65.75) * mm});
            skLineSegment(sketch, "E1580", {"start": v(-139.03, 65.75) * mm, "end": v(-138.74, 65.92) * mm});
            skLineSegment(sketch, "E1581", {"start": v(-136.18, 68.93) * mm, "end": v(-136.18, 66.81) * mm});
            skLineSegment(sketch, "E1582", {"start": v(-136.18, 66.81) * mm, "end": v(-139.35, 68.34) * mm});
            skLineSegment(sketch, "E1583", {"start": v(-136.18, 71.22) * mm, "end": v(-136.32, 71.66) * mm});
            skLineSegment(sketch, "E1584", {"start": v(-136.32, 71.66) * mm, "end": v(-136.62, 71.8) * mm});
            skLineSegment(sketch, "E1585", {"start": v(-136.62, 71.8) * mm, "end": v(-136.92, 71.8) * mm});
            skLineSegment(sketch, "E1586", {"start": v(-136.92, 71.8) * mm, "end": v(-137.23, 71.66) * mm});
            skLineSegment(sketch, "E1587", {"start": v(-137.23, 71.66) * mm, "end": v(-137.38, 71.36) * mm});
            skLineSegment(sketch, "E1588", {"start": v(-137.38, 71.36) * mm, "end": v(-137.53, 70.75) * mm});
            skLineSegment(sketch, "E1589", {"start": v(-137.53, 70.75) * mm, "end": v(-137.68, 70.3) * mm});
            skLineSegment(sketch, "E1590", {"start": v(-137.68, 70.3) * mm, "end": v(-137.97, 69.99) * mm});
            skLineSegment(sketch, "E1591", {"start": v(-137.97, 69.99) * mm, "end": v(-138.3, 69.84) * mm});
            skLineSegment(sketch, "E1592", {"start": v(-138.3, 69.84) * mm, "end": v(-138.74, 69.84) * mm});
            skLineSegment(sketch, "E1593", {"start": v(-138.74, 69.84) * mm, "end": v(-139.03, 69.99) * mm});
            skLineSegment(sketch, "E1594", {"start": v(-139.03, 69.99) * mm, "end": v(-139.18, 70.16) * mm});
            skLineSegment(sketch, "E1595", {"start": v(-139.18, 70.16) * mm, "end": v(-139.35, 70.6) * mm});
            skLineSegment(sketch, "E1596", {"start": v(-139.35, 70.6) * mm, "end": v(-139.35, 71.22) * mm});
            skLineSegment(sketch, "E1597", {"start": v(-139.35, 71.22) * mm, "end": v(-139.18, 71.66) * mm});
            skLineSegment(sketch, "E1598", {"start": v(-139.18, 71.66) * mm, "end": v(-139.03, 71.8) * mm});
            skLineSegment(sketch, "E1599", {"start": v(-139.03, 71.8) * mm, "end": v(-138.74, 71.96) * mm});
            skLineSegment(sketch, "E1600", {"start": v(-138.74, 71.96) * mm, "end": v(-138.3, 71.96) * mm});
            skLineSegment(sketch, "E1601", {"start": v(-138.3, 71.96) * mm, "end": v(-137.97, 71.8) * mm});
            skLineSegment(sketch, "E1602", {"start": v(-137.97, 71.8) * mm, "end": v(-137.68, 71.51) * mm});
            skLineSegment(sketch, "E1603", {"start": v(-137.68, 71.51) * mm, "end": v(-137.53, 71.05) * mm});
            skLineSegment(sketch, "E1604", {"start": v(-137.53, 71.05) * mm, "end": v(-137.38, 70.45) * mm});
            skLineSegment(sketch, "E1605", {"start": v(-137.38, 70.45) * mm, "end": v(-137.23, 70.16) * mm});
            skLineSegment(sketch, "E1606", {"start": v(-137.23, 70.16) * mm, "end": v(-136.92, 69.99) * mm});
            skLineSegment(sketch, "E1607", {"start": v(-136.92, 69.99) * mm, "end": v(-136.62, 69.99) * mm});
            skLineSegment(sketch, "E1608", {"start": v(-136.62, 69.99) * mm, "end": v(-136.32, 70.16) * mm});
            skLineSegment(sketch, "E1609", {"start": v(-136.32, 70.16) * mm, "end": v(-136.18, 70.6) * mm});
            skLineSegment(sketch, "E1610", {"start": v(-136.18, 70.6) * mm, "end": v(-136.18, 71.22) * mm});
            skLineSegment(sketch, "E1611", {"start": v(-139.03, 73.33) * mm, "end": v(-139.18, 73.48) * mm});
            skLineSegment(sketch, "E1612", {"start": v(-139.18, 73.48) * mm, "end": v(-139.35, 73.33) * mm});
            skLineSegment(sketch, "E1613", {"start": v(-139.35, 73.33) * mm, "end": v(-139.18, 73.16) * mm});
            skLineSegment(sketch, "E1614", {"start": v(-51.76, 86.05) * mm, "end": v(-51.76, 87.2) * mm});
            skLineSegment(sketch, "E1615", {"start": v(-51.76, 87.2) * mm, "end": v(-55.21, 86.62) * mm});
            skLineSegment(sketch, "E1616", {"start": v(-4.41, 129.49) * mm, "end": v(-99.66, 129.49) * mm});
            skLineSegment(sketch, "E1617", {"start": v(-4.41, 78.69) * mm, "end": v(-99.66, 78.69) * mm});
            skLineSegment(sketch, "E1618", {"start": v(-55.21, 97.74) * mm, "end": v(-54.32, 97.78) * mm});
            skLineSegment(sketch, "E1619", {"start": v(-54.32, 97.78) * mm, "end": v(-53.46, 97.9) * mm});
            skLineSegment(sketch, "E1620", {"start": v(-53.46, 97.9) * mm, "end": v(-52.59, 98.1) * mm});
            skLineSegment(sketch, "E1621", {"start": v(-52.59, 98.1) * mm, "end": v(-51.76, 98.4) * mm});
            skLineSegment(sketch, "E1622", {"start": v(-51.76, 98.4) * mm, "end": v(-50.96, 98.73) * mm});
            skLineSegment(sketch, "E1623", {"start": v(-50.96, 98.73) * mm, "end": v(-50.2, 99.18) * mm});
            skLineSegment(sketch, "E1624", {"start": v(-50.2, 99.18) * mm, "end": v(-49.46, 99.66) * mm});
            skLineSegment(sketch, "E1625", {"start": v(-49.46, 99.66) * mm, "end": v(-48.78, 100.23) * mm});
            skLineSegment(sketch, "E1626", {"start": v(-48.78, 100.23) * mm, "end": v(-48.16, 100.85) * mm});
            skLineSegment(sketch, "E1627", {"start": v(-48.16, 100.85) * mm, "end": v(-47.61, 101.53) * mm});
            skLineSegment(sketch, "E1628", {"start": v(-47.61, 101.53) * mm, "end": v(-47.1, 102.25) * mm});
            skLineSegment(sketch, "E1629", {"start": v(-47.1, 102.25) * mm, "end": v(-46.68, 103.03) * mm});
            skLineSegment(sketch, "E1630", {"start": v(-46.68, 103.03) * mm, "end": v(-46.32, 103.83) * mm});
            skLineSegment(sketch, "E1631", {"start": v(-46.32, 103.83) * mm, "end": v(-46.05, 104.66) * mm});
            skLineSegment(sketch, "E1632", {"start": v(-46.05, 104.66) * mm, "end": v(-45.84, 105.53) * mm});
            skLineSegment(sketch, "E1633", {"start": v(-45.84, 105.53) * mm, "end": v(-45.73, 106.4) * mm});
            skLineSegment(sketch, "E1634", {"start": v(-45.73, 106.4) * mm, "end": v(-45.69, 107.26) * mm});
            skLineSegment(sketch, "E1635", {"start": v(-45.69, 107.26) * mm, "end": v(-45.73, 108.15) * mm});
            skLineSegment(sketch, "E1636", {"start": v(-45.73, 108.15) * mm, "end": v(-45.84, 109.02) * mm});
            skLineSegment(sketch, "E1637", {"start": v(-45.84, 109.02) * mm, "end": v(-46.05, 109.87) * mm});
            skLineSegment(sketch, "E1638", {"start": v(-46.05, 109.87) * mm, "end": v(-46.32, 110.71) * mm});
            skLineSegment(sketch, "E1639", {"start": v(-46.32, 110.71) * mm, "end": v(-46.68, 111.52) * mm});
            skLineSegment(sketch, "E1640", {"start": v(-46.68, 111.52) * mm, "end": v(-47.1, 112.28) * mm});
            skLineSegment(sketch, "E1641", {"start": v(-47.1, 112.28) * mm, "end": v(-47.61, 113) * mm});
            skLineSegment(sketch, "E1642", {"start": v(-47.61, 113) * mm, "end": v(-48.16, 113.68) * mm});
            skLineSegment(sketch, "E1643", {"start": v(-48.16, 113.68) * mm, "end": v(-48.78, 114.31) * mm});
            skLineSegment(sketch, "E1644", {"start": v(-48.78, 114.31) * mm, "end": v(-49.46, 114.86) * mm});
            skLineSegment(sketch, "E1645", {"start": v(-49.46, 114.86) * mm, "end": v(-50.2, 115.37) * mm});
            skLineSegment(sketch, "E1646", {"start": v(-50.2, 115.37) * mm, "end": v(-50.96, 115.8) * mm});
            skLineSegment(sketch, "E1647", {"start": v(-50.96, 115.8) * mm, "end": v(-51.76, 116.15) * mm});
            skLineSegment(sketch, "E1648", {"start": v(-51.76, 116.15) * mm, "end": v(-52.59, 116.43) * mm});
            skLineSegment(sketch, "E1649", {"start": v(-52.59, 116.43) * mm, "end": v(-53.46, 116.64) * mm});
            skLineSegment(sketch, "E1650", {"start": v(-53.46, 116.64) * mm, "end": v(-54.32, 116.74) * mm});
            skLineSegment(sketch, "E1651", {"start": v(-54.32, 116.74) * mm, "end": v(-55.21, 116.79) * mm});
            skLineSegment(sketch, "E1652", {"start": v(-55.21, 116.79) * mm, "end": v(-56.08, 116.74) * mm});
            skLineSegment(sketch, "E1653", {"start": v(-56.08, 116.74) * mm, "end": v(-56.95, 116.64) * mm});
            skLineSegment(sketch, "E1654", {"start": v(-56.95, 116.64) * mm, "end": v(-57.82, 116.43) * mm});
            skLineSegment(sketch, "E1655", {"start": v(-57.82, 116.43) * mm, "end": v(-58.64, 116.15) * mm});
            skLineSegment(sketch, "E1656", {"start": v(-58.64, 116.15) * mm, "end": v(-59.45, 115.8) * mm});
            skLineSegment(sketch, "E1657", {"start": v(-59.45, 115.8) * mm, "end": v(-60.23, 115.37) * mm});
            skLineSegment(sketch, "E1658", {"start": v(-60.23, 115.37) * mm, "end": v(-60.95, 114.86) * mm});
            skLineSegment(sketch, "E1659", {"start": v(-60.95, 114.86) * mm, "end": v(-61.63, 114.31) * mm});
            skLineSegment(sketch, "E1660", {"start": v(-61.63, 114.31) * mm, "end": v(-62.24, 113.68) * mm});
            skLineSegment(sketch, "E1661", {"start": v(-62.24, 113.68) * mm, "end": v(-62.81, 113) * mm});
            skLineSegment(sketch, "E1662", {"start": v(-62.81, 113) * mm, "end": v(-63.3, 112.28) * mm});
            skLineSegment(sketch, "E1663", {"start": v(-63.3, 112.28) * mm, "end": v(-63.72, 111.52) * mm});
            skLineSegment(sketch, "E1664", {"start": v(-63.72, 111.52) * mm, "end": v(-64.08, 110.71) * mm});
            skLineSegment(sketch, "E1665", {"start": v(-64.08, 110.71) * mm, "end": v(-64.36, 109.87) * mm});
            skLineSegment(sketch, "E1666", {"start": v(-64.36, 109.87) * mm, "end": v(-64.57, 109.02) * mm});
            skLineSegment(sketch, "E1667", {"start": v(-64.57, 109.02) * mm, "end": v(-64.7, 108.15) * mm});
            skLineSegment(sketch, "E1668", {"start": v(-64.7, 108.15) * mm, "end": v(-64.74, 107.26) * mm});
            skLineSegment(sketch, "E1669", {"start": v(-64.74, 107.26) * mm, "end": v(-64.7, 106.4) * mm});
            skLineSegment(sketch, "E1670", {"start": v(-64.7, 106.4) * mm, "end": v(-64.57, 105.53) * mm});
            skLineSegment(sketch, "E1671", {"start": v(-64.57, 105.53) * mm, "end": v(-64.36, 104.66) * mm});
            skLineSegment(sketch, "E1672", {"start": v(-64.36, 104.66) * mm, "end": v(-64.08, 103.83) * mm});
            skLineSegment(sketch, "E1673", {"start": v(-64.08, 103.83) * mm, "end": v(-63.72, 103.03) * mm});
            skLineSegment(sketch, "E1674", {"start": v(-63.72, 103.03) * mm, "end": v(-63.3, 102.25) * mm});
            skLineSegment(sketch, "E1675", {"start": v(-63.3, 102.25) * mm, "end": v(-62.81, 101.53) * mm});
            skLineSegment(sketch, "E1676", {"start": v(-62.81, 101.53) * mm, "end": v(-62.24, 100.85) * mm});
            skLineSegment(sketch, "E1677", {"start": v(-62.24, 100.85) * mm, "end": v(-61.63, 100.23) * mm});
            skLineSegment(sketch, "E1678", {"start": v(-61.63, 100.23) * mm, "end": v(-60.95, 99.66) * mm});
            skLineSegment(sketch, "E1679", {"start": v(-60.95, 99.66) * mm, "end": v(-60.23, 99.18) * mm});
            skLineSegment(sketch, "E1680", {"start": v(-60.23, 99.18) * mm, "end": v(-59.45, 98.73) * mm});
            skLineSegment(sketch, "E1681", {"start": v(-59.45, 98.73) * mm, "end": v(-58.64, 98.4) * mm});
            skLineSegment(sketch, "E1682", {"start": v(-58.64, 98.4) * mm, "end": v(-57.82, 98.1) * mm});
            skLineSegment(sketch, "E1683", {"start": v(-57.82, 98.1) * mm, "end": v(-56.95, 97.9) * mm});
            skLineSegment(sketch, "E1684", {"start": v(-56.95, 97.9) * mm, "end": v(-56.08, 97.78) * mm});
            skLineSegment(sketch, "E1685", {"start": v(-56.08, 97.78) * mm, "end": v(-55.21, 97.74) * mm});
            skLineSegment(sketch, "E1686", {"start": v(-17.11, 56.46) * mm, "end": v(-93.31, 56.46) * mm});
            skLineSegment(sketch, "E1687", {"start": v(-39.74, 107.26) * mm, "end": v(-70.66, 107.26) * mm});
            skLineSegment(sketch, "E1688", {"start": v(-99.66, 129.49) * mm, "end": v(-99.66, 78.69) * mm});
            skLineSegment(sketch, "E1689", {"start": v(-55.21, 122.71) * mm, "end": v(-55.21, 91.81) * mm});
            skLineSegment(sketch, "E1690", {"start": v(-55.21, 94.56) * mm, "end": v(-55.21, 83.45) * mm});
            skLineSegment(sketch, "E1691", {"start": v(-65.2, 113.7) * mm, "end": v(-68.23, 115.07) * mm});
            skLineSegment(sketch, "E1692", {"start": v(-65.65, 114.6) * mm, "end": v(-65.8, 114.9) * mm});
            skLineSegment(sketch, "E1693", {"start": v(-65.8, 114.9) * mm, "end": v(-66.11, 115.22) * mm});
            skLineSegment(sketch, "E1694", {"start": v(-66.11, 115.22) * mm, "end": v(-66.56, 115.37) * mm});
            skLineSegment(sketch, "E1695", {"start": v(-66.56, 115.37) * mm, "end": v(-66.85, 115.37) * mm});
            skLineSegment(sketch, "E1696", {"start": v(-66.85, 115.37) * mm, "end": v(-67.32, 115.22) * mm});
            skLineSegment(sketch, "E1697", {"start": v(-67.32, 115.22) * mm, "end": v(-67.62, 114.9) * mm});
            skLineSegment(sketch, "E1698", {"start": v(-67.62, 114.9) * mm, "end": v(-67.77, 114.6) * mm});
            skLineSegment(sketch, "E1699", {"start": v(-67.77, 114.6) * mm, "end": v(-67.77, 114.16) * mm});
            skLineSegment(sketch, "E1700", {"start": v(-67.77, 114.16) * mm, "end": v(-67.62, 113.84) * mm});
            skLineSegment(sketch, "E1701", {"start": v(-67.62, 113.84) * mm, "end": v(-67.32, 113.55) * mm});
            skLineSegment(sketch, "E1702", {"start": v(-67.32, 113.55) * mm, "end": v(-66.85, 113.4) * mm});
            skLineSegment(sketch, "E1703", {"start": v(-66.85, 113.4) * mm, "end": v(-66.56, 113.4) * mm});
            skLineSegment(sketch, "E1704", {"start": v(-66.56, 113.4) * mm, "end": v(-66.11, 113.55) * mm});
            skLineSegment(sketch, "E1705", {"start": v(-66.11, 113.55) * mm, "end": v(-65.8, 113.84) * mm});
            skLineSegment(sketch, "E1706", {"start": v(-65.8, 113.84) * mm, "end": v(-65.65, 114.16) * mm});
            skLineSegment(sketch, "E1707", {"start": v(-65.65, 114.16) * mm, "end": v(-65.65, 114.6) * mm});
            skLineSegment(sketch, "E1708", {"start": v(-65.06, 117.63) * mm, "end": v(-65.2, 118.08) * mm});
            skLineSegment(sketch, "E1709", {"start": v(-65.2, 118.08) * mm, "end": v(-65.5, 118.25) * mm});
            skLineSegment(sketch, "E1710", {"start": v(-65.5, 118.25) * mm, "end": v(-65.8, 118.25) * mm});
            skLineSegment(sketch, "E1711", {"start": v(-65.8, 118.25) * mm, "end": v(-66.11, 118.08) * mm});
            skLineSegment(sketch, "E1712", {"start": v(-66.11, 118.08) * mm, "end": v(-66.26, 117.78) * mm});
            skLineSegment(sketch, "E1713", {"start": v(-66.26, 117.78) * mm, "end": v(-66.41, 117.19) * mm});
            skLineSegment(sketch, "E1714", {"start": v(-66.41, 117.19) * mm, "end": v(-66.56, 116.72) * mm});
            skLineSegment(sketch, "E1715", {"start": v(-66.56, 116.72) * mm, "end": v(-66.85, 116.43) * mm});
            skLineSegment(sketch, "E1716", {"start": v(-66.85, 116.43) * mm, "end": v(-67.17, 116.28) * mm});
            skLineSegment(sketch, "E1717", {"start": v(-67.17, 116.28) * mm, "end": v(-67.62, 116.28) * mm});
            skLineSegment(sketch, "E1718", {"start": v(-67.62, 116.28) * mm, "end": v(-67.91, 116.43) * mm});
            skLineSegment(sketch, "E1719", {"start": v(-67.91, 116.43) * mm, "end": v(-68.08, 116.58) * mm});
            skLineSegment(sketch, "E1720", {"start": v(-68.08, 116.58) * mm, "end": v(-68.23, 117.02) * mm});
            skLineSegment(sketch, "E1721", {"start": v(-68.23, 117.02) * mm, "end": v(-68.23, 117.63) * mm});
            skLineSegment(sketch, "E1722", {"start": v(-68.23, 117.63) * mm, "end": v(-68.08, 118.08) * mm});
            skLineSegment(sketch, "E1723", {"start": v(-68.08, 118.08) * mm, "end": v(-67.91, 118.25) * mm});
            skLineSegment(sketch, "E1724", {"start": v(-67.91, 118.25) * mm, "end": v(-67.62, 118.4) * mm});
            skLineSegment(sketch, "E1725", {"start": v(-67.62, 118.4) * mm, "end": v(-67.17, 118.4) * mm});
            skLineSegment(sketch, "E1726", {"start": v(-67.17, 118.4) * mm, "end": v(-66.85, 118.25) * mm});
            skLineSegment(sketch, "E1727", {"start": v(-66.85, 118.25) * mm, "end": v(-66.56, 117.93) * mm});
            skLineSegment(sketch, "E1728", {"start": v(-66.56, 117.93) * mm, "end": v(-66.41, 117.49) * mm});
            skLineSegment(sketch, "E1729", {"start": v(-66.41, 117.49) * mm, "end": v(-66.26, 116.87) * mm});
            skLineSegment(sketch, "E1730", {"start": v(-66.26, 116.87) * mm, "end": v(-66.11, 116.58) * mm});
            skLineSegment(sketch, "E1731", {"start": v(-66.11, 116.58) * mm, "end": v(-65.8, 116.43) * mm});
            skLineSegment(sketch, "E1732", {"start": v(-65.8, 116.43) * mm, "end": v(-65.5, 116.43) * mm});
            skLineSegment(sketch, "E1733", {"start": v(-65.5, 116.43) * mm, "end": v(-65.2, 116.58) * mm});
            skLineSegment(sketch, "E1734", {"start": v(-65.2, 116.58) * mm, "end": v(-65.06, 117.02) * mm});
            skLineSegment(sketch, "E1735", {"start": v(-65.06, 117.02) * mm, "end": v(-65.06, 117.63) * mm});
            skLineSegment(sketch, "E1736", {"start": v(-65.06, 121.42) * mm, "end": v(-65.06, 119.3) * mm});
            skLineSegment(sketch, "E1737", {"start": v(-65.06, 119.3) * mm, "end": v(-68.23, 120.8) * mm});
            skLineSegment(sketch, "E1738", {"start": v(-67.93, 122.78) * mm, "end": v(-68.08, 122.93) * mm});
            skLineSegment(sketch, "E1739", {"start": v(-68.08, 122.93) * mm, "end": v(-68.23, 122.78) * mm});
            skLineSegment(sketch, "E1740", {"start": v(-68.23, 122.78) * mm, "end": v(-68.08, 122.63) * mm});
            skLineSegment(sketch, "E1741", {"start": v(-4.41, 164.75) * mm, "end": v(-4.41, 58.07) * mm});
            skLineSegment(sketch, "E1742", {"start": v(-42.87, 145.13) * mm, "end": v(-42.72, 145.17) * mm});
            skLineSegment(sketch, "E1743", {"start": v(-42.72, 145.17) * mm, "end": v(-42.62, 145.28) * mm});
            skLineSegment(sketch, "E1744", {"start": v(-42.62, 145.28) * mm, "end": v(-42.58, 145.43) * mm});
            skLineSegment(sketch, "E1745", {"start": v(-42.58, 145.43) * mm, "end": v(-42.62, 145.57) * mm});
            skLineSegment(sketch, "E1746", {"start": v(-42.62, 145.57) * mm, "end": v(-42.72, 145.7) * mm});
            skLineSegment(sketch, "E1747", {"start": v(-42.72, 145.7) * mm, "end": v(-42.87, 145.72) * mm});
            skLineSegment(sketch, "E1748", {"start": v(-42.87, 145.72) * mm, "end": v(-43.02, 145.7) * mm});
            skLineSegment(sketch, "E1749", {"start": v(-43.02, 145.7) * mm, "end": v(-43.13, 145.57) * mm});
            skLineSegment(sketch, "E1750", {"start": v(-43.13, 145.57) * mm, "end": v(-43.17, 145.43) * mm});
            skLineSegment(sketch, "E1751", {"start": v(-43.17, 145.43) * mm, "end": v(-43.13, 145.28) * mm});
            skLineSegment(sketch, "E1752", {"start": v(-43.13, 145.28) * mm, "end": v(-43.02, 145.17) * mm});
            skLineSegment(sketch, "E1753", {"start": v(-43.02, 145.17) * mm, "end": v(-42.87, 145.13) * mm});
            skLineSegment(sketch, "E1754", {"start": v(-42.58, 146.95) * mm, "end": v(-42.58, 148.45) * mm});
            skLineSegment(sketch, "E1755", {"start": v(-42.58, 148.45) * mm, "end": v(-43.93, 148.6) * mm});
            skLineSegment(sketch, "E1756", {"start": v(-43.93, 148.6) * mm, "end": v(-43.78, 148.45) * mm});
            skLineSegment(sketch, "E1757", {"start": v(-43.78, 148.45) * mm, "end": v(-43.64, 148) * mm});
            skLineSegment(sketch, "E1758", {"start": v(-43.64, 148) * mm, "end": v(-43.64, 147.54) * mm});
            skLineSegment(sketch, "E1759", {"start": v(-43.64, 147.54) * mm, "end": v(-43.78, 147.1) * mm});
            skLineSegment(sketch, "E1760", {"start": v(-43.78, 147.1) * mm, "end": v(-44.08, 146.78) * mm});
            skLineSegment(sketch, "E1761", {"start": v(-44.08, 146.78) * mm, "end": v(-44.55, 146.63) * mm});
            skLineSegment(sketch, "E1762", {"start": v(-44.55, 146.63) * mm, "end": v(-44.84, 146.63) * mm});
            skLineSegment(sketch, "E1763", {"start": v(-44.84, 146.63) * mm, "end": v(-45.29, 146.78) * mm});
            skLineSegment(sketch, "E1764", {"start": v(-45.29, 146.78) * mm, "end": v(-45.6, 147.1) * mm});
            skLineSegment(sketch, "E1765", {"start": v(-45.6, 147.1) * mm, "end": v(-45.75, 147.54) * mm});
            skLineSegment(sketch, "E1766", {"start": v(-45.75, 147.54) * mm, "end": v(-45.75, 148) * mm});
            skLineSegment(sketch, "E1767", {"start": v(-45.75, 148) * mm, "end": v(-45.6, 148.45) * mm});
            skLineSegment(sketch, "E1768", {"start": v(-45.6, 148.45) * mm, "end": v(-45.46, 148.6) * mm});
            skLineSegment(sketch, "E1769", {"start": v(-45.46, 148.6) * mm, "end": v(-45.14, 148.75) * mm});
            skLineSegment(sketch, "E1770", {"start": v(-42.58, 150.27) * mm, "end": v(-45.75, 150.27) * mm});
            skLineSegment(sketch, "E1771", {"start": v(-42.58, 150.27) * mm, "end": v(-44.7, 151.78) * mm});
            skLineSegment(sketch, "E1772", {"start": v(-44.7, 151.78) * mm, "end": v(-44.7, 149.51) * mm});
            skLineSegment(sketch, "E1773", {"start": v(-43.17, 154.19) * mm, "end": v(-43.02, 153.9) * mm});
            skLineSegment(sketch, "E1774", {"start": v(-43.02, 153.9) * mm, "end": v(-42.58, 153.45) * mm});
            skLineSegment(sketch, "E1775", {"start": v(-42.58, 153.45) * mm, "end": v(-45.75, 153.45) * mm});
            skLineSegment(sketch, "E1776", {"start": v(-41.65, 143.52) * mm, "end": v(-40.67, 141.91) * mm});
            skLineSegment(sketch, "E1777", {"start": v(-40.67, 141.91) * mm, "end": v(-39.63, 140.35) * mm});
            skLineSegment(sketch, "E1778", {"start": v(-39.63, 140.35) * mm, "end": v(-38.53, 138.82) * mm});
            skLineSegment(sketch, "E1779", {"start": v(-38.53, 138.82) * mm, "end": v(-37.37, 137.36) * mm});
            skLineSegment(sketch, "E1780", {"start": v(-37.37, 137.36) * mm, "end": v(-36.12, 135.94) * mm});
            skLineSegment(sketch, "E1781", {"start": v(-36.12, 135.94) * mm, "end": v(-34.83, 134.57) * mm});
            skLineSegment(sketch, "E1782", {"start": v(-34.83, 134.57) * mm, "end": v(-33.48, 133.28) * mm});
            skLineSegment(sketch, "E1783", {"start": v(-33.48, 133.28) * mm, "end": v(-32.08, 132.03) * mm});
            skLineSegment(sketch, "E1784", {"start": v(-32.08, 132.03) * mm, "end": v(-30.62, 130.84) * mm});
            skLineSegment(sketch, "E1785", {"start": v(-30.62, 130.84) * mm, "end": v(-29.1, 129.72) * mm});
            skLineSegment(sketch, "E1786", {"start": v(-29.1, 129.72) * mm, "end": v(-27.55, 128.68) * mm});
            skLineSegment(sketch, "E1787", {"start": v(-27.55, 128.68) * mm, "end": v(-25.94, 127.69) * mm});
            skLineSegment(sketch, "E1788", {"start": v(-25.94, 127.69) * mm, "end": v(-24.29, 126.78) * mm});
            skLineSegment(sketch, "E1789", {"start": v(-24.29, 126.78) * mm, "end": v(-22.6, 125.95) * mm});
            skLineSegment(sketch, "E1790", {"start": v(-22.6, 125.95) * mm, "end": v(-20.88, 125.2) * mm});
            skLineSegment(sketch, "E1791", {"start": v(-20.88, 125.2) * mm, "end": v(-19.15, 124.51) * mm});
            skLineSegment(sketch, "E1792", {"start": v(-19.15, 124.51) * mm, "end": v(-17.37, 123.9) * mm});
            skLineSegment(sketch, "E1793", {"start": v(-17.37, 123.9) * mm, "end": v(-15.55, 123.37) * mm});
            skLineSegment(sketch, "E1794", {"start": v(-15.55, 123.37) * mm, "end": v(-13.73, 122.93) * mm});
            skLineSegment(sketch, "E1795", {"start": v(-13.73, 122.93) * mm, "end": v(-11.89, 122.54) * mm});
            skLineSegment(sketch, "E1796", {"start": v(-11.89, 122.54) * mm, "end": v(-10.02, 122.27) * mm});
            skLineSegment(sketch, "E1797", {"start": v(-10.02, 122.27) * mm, "end": v(-8.16, 122.06) * mm});
            skLineSegment(sketch, "E1798", {"start": v(-8.16, 122.06) * mm, "end": v(-6.28, 121.93) * mm});
            skLineSegment(sketch, "E1799", {"start": v(-6.28, 121.93) * mm, "end": v(-4.41, 121.89) * mm});
            skLineSegment(sketch, "E1800", {"start": v(-7.78, 122.78) * mm, "end": v(-7.88, 121.63) * mm});
            skLineSegment(sketch, "E1801", {"start": v(-7.88, 121.63) * mm, "end": v(-4.41, 121.89) * mm});
            skLineSegment(sketch, "E1802", {"start": v(-7.84, 87.2) * mm, "end": v(-7.84, 86.05) * mm});
            skLineSegment(sketch, "E1803", {"start": v(-7.84, 86.05) * mm, "end": v(-4.41, 86.62) * mm});
            skLineSegment(sketch, "E1804", {"start": v(-47.72, -4.98) * mm, "end": v(-47.87, -5.15) * mm});
            skLineSegment(sketch, "E1805", {"start": v(-47.87, -5.15) * mm, "end": v(-48.02, -4.98) * mm});
            skLineSegment(sketch, "E1806", {"start": v(-48.02, -4.98) * mm, "end": v(-47.87, -4.84) * mm});
            skLineSegment(sketch, "E1807", {"start": v(-47.87, -4.84) * mm, "end": v(-47.72, -4.98) * mm});
            skLineSegment(sketch, "E1808", {"start": v(-47.72, -4.98) * mm, "end": v(-47.72, -5.3) * mm});
            skLineSegment(sketch, "E1809", {"start": v(-47.72, -5.3) * mm, "end": v(-47.87, -5.6) * mm});
            skLineSegment(sketch, "E1810", {"start": v(-47.87, -5.6) * mm, "end": v(-48.02, -5.75) * mm});
            skLineSegment(sketch, "E1811", {"start": v(-48.63, -4.98) * mm, "end": v(-48.78, -5.15) * mm});
            skLineSegment(sketch, "E1812", {"start": v(-48.78, -5.15) * mm, "end": v(-48.93, -4.98) * mm});
            skLineSegment(sketch, "E1813", {"start": v(-48.93, -4.98) * mm, "end": v(-48.78, -4.84) * mm});
            skLineSegment(sketch, "E1814", {"start": v(-48.78, -4.84) * mm, "end": v(-48.63, -4.98) * mm});
            skLineSegment(sketch, "E1815", {"start": v(-48.63, -4.98) * mm, "end": v(-48.63, -5.3) * mm});
            skLineSegment(sketch, "E1816", {"start": v(-48.63, -5.3) * mm, "end": v(-48.78, -5.6) * mm});
            skLineSegment(sketch, "E1817", {"start": v(-48.78, -5.6) * mm, "end": v(-48.93, -5.75) * mm});
            skLineSegment(sketch, "E1818", {"start": v(-50.13, -5.45) * mm, "end": v(-51.66, -5.45) * mm});
            skLineSegment(sketch, "E1819", {"start": v(-51.66, -5.45) * mm, "end": v(-51.8, -6.8) * mm});
            skLineSegment(sketch, "E1820", {"start": v(-51.8, -6.8) * mm, "end": v(-51.66, -6.66) * mm});
            skLineSegment(sketch, "E1821", {"start": v(-51.66, -6.66) * mm, "end": v(-51.2, -6.5) * mm});
            skLineSegment(sketch, "E1822", {"start": v(-51.2, -6.5) * mm, "end": v(-50.75, -6.5) * mm});
            skLineSegment(sketch, "E1823", {"start": v(-50.75, -6.5) * mm, "end": v(-50.28, -6.66) * mm});
            skLineSegment(sketch, "E1824", {"start": v(-50.28, -6.66) * mm, "end": v(-49.99, -6.95) * mm});
            skLineSegment(sketch, "E1825", {"start": v(-49.99, -6.95) * mm, "end": v(-49.84, -7.42) * mm});
            skLineSegment(sketch, "E1826", {"start": v(-49.84, -7.42) * mm, "end": v(-49.84, -7.72) * mm});
            skLineSegment(sketch, "E1827", {"start": v(-49.84, -7.72) * mm, "end": v(-49.99, -8.16) * mm});
            skLineSegment(sketch, "E1828", {"start": v(-49.99, -8.16) * mm, "end": v(-50.28, -8.48) * mm});
            skLineSegment(sketch, "E1829", {"start": v(-50.28, -8.48) * mm, "end": v(-50.75, -8.63) * mm});
            skLineSegment(sketch, "E1830", {"start": v(-50.75, -8.63) * mm, "end": v(-51.2, -8.63) * mm});
            skLineSegment(sketch, "E1831", {"start": v(-51.2, -8.63) * mm, "end": v(-51.66, -8.48) * mm});
            skLineSegment(sketch, "E1832", {"start": v(-51.66, -8.48) * mm, "end": v(-51.8, -8.33) * mm});
            skLineSegment(sketch, "E1833", {"start": v(-51.8, -8.33) * mm, "end": v(-51.95, -8.01) * mm});
            skLineSegment(sketch, "E1834", {"start": v(-54.98, -5.45) * mm, "end": v(-52.86, -5.45) * mm});
            skLineSegment(sketch, "E1835", {"start": v(-52.86, -5.45) * mm, "end": v(-54.37, -8.63) * mm});
            skLineSegment(sketch, "E1836", {"start": v(-56.34, -8.33) * mm, "end": v(-56.48, -8.48) * mm});
            skLineSegment(sketch, "E1837", {"start": v(-56.48, -8.48) * mm, "end": v(-56.34, -8.63) * mm});
            skLineSegment(sketch, "E1838", {"start": v(-56.34, -8.63) * mm, "end": v(-56.19, -8.48) * mm});
            skLineSegment(sketch, "E1839", {"start": v(-59.21, -5.45) * mm, "end": v(-57.54, -5.45) * mm});
            skLineSegment(sketch, "E1840", {"start": v(-57.54, -5.45) * mm, "end": v(-58.45, -6.66) * mm});
            skLineSegment(sketch, "E1841", {"start": v(-58.45, -6.66) * mm, "end": v(-58, -6.66) * mm});
            skLineSegment(sketch, "E1842", {"start": v(-58, -6.66) * mm, "end": v(-57.69, -6.8) * mm});
            skLineSegment(sketch, "E1843", {"start": v(-57.69, -6.8) * mm, "end": v(-57.54, -6.95) * mm});
            skLineSegment(sketch, "E1844", {"start": v(-57.54, -6.95) * mm, "end": v(-57.4, -7.42) * mm});
            skLineSegment(sketch, "E1845", {"start": v(-57.4, -7.42) * mm, "end": v(-57.4, -7.72) * mm});
            skLineSegment(sketch, "E1846", {"start": v(-57.4, -7.72) * mm, "end": v(-57.54, -8.16) * mm});
            skLineSegment(sketch, "E1847", {"start": v(-57.54, -8.16) * mm, "end": v(-57.86, -8.48) * mm});
            skLineSegment(sketch, "E1848", {"start": v(-57.86, -8.48) * mm, "end": v(-58.3, -8.63) * mm});
            skLineSegment(sketch, "E1849", {"start": v(-58.3, -8.63) * mm, "end": v(-58.75, -8.63) * mm});
            skLineSegment(sketch, "E1850", {"start": v(-58.75, -8.63) * mm, "end": v(-59.21, -8.48) * mm});
            skLineSegment(sketch, "E1851", {"start": v(-59.21, -8.48) * mm, "end": v(-59.36, -8.33) * mm});
            skLineSegment(sketch, "E1852", {"start": v(-59.36, -8.33) * mm, "end": v(-59.51, -8.01) * mm});
            skLineSegment(sketch, "E1853", {"start": v(-4.41, -10.21) * mm, "end": v(-99.66, -10.21) * mm});
            skLineSegment(sketch, "E1854", {"start": v(-25.41, 91.85) * mm, "end": v(-25.58, 91.68) * mm});
            skLineSegment(sketch, "E1855", {"start": v(-25.58, 91.68) * mm, "end": v(-25.73, 91.85) * mm});
            skLineSegment(sketch, "E1856", {"start": v(-25.73, 91.85) * mm, "end": v(-25.58, 92) * mm});
            skLineSegment(sketch, "E1857", {"start": v(-25.58, 92) * mm, "end": v(-25.41, 91.85) * mm});
            skLineSegment(sketch, "E1858", {"start": v(-25.41, 91.85) * mm, "end": v(-25.41, 91.54) * mm});
            skLineSegment(sketch, "E1859", {"start": v(-25.41, 91.54) * mm, "end": v(-25.58, 91.24) * mm});
            skLineSegment(sketch, "E1860", {"start": v(-25.58, 91.24) * mm, "end": v(-25.73, 91.1) * mm});
            skLineSegment(sketch, "E1861", {"start": v(-26.32, 91.85) * mm, "end": v(-26.47, 91.68) * mm});
            skLineSegment(sketch, "E1862", {"start": v(-26.47, 91.68) * mm, "end": v(-26.64, 91.85) * mm});
            skLineSegment(sketch, "E1863", {"start": v(-26.64, 91.85) * mm, "end": v(-26.47, 92) * mm});
            skLineSegment(sketch, "E1864", {"start": v(-26.47, 92) * mm, "end": v(-26.32, 91.85) * mm});
            skLineSegment(sketch, "E1865", {"start": v(-26.32, 91.85) * mm, "end": v(-26.32, 91.54) * mm});
            skLineSegment(sketch, "E1866", {"start": v(-26.32, 91.54) * mm, "end": v(-26.47, 91.24) * mm});
            skLineSegment(sketch, "E1867", {"start": v(-26.47, 91.24) * mm, "end": v(-26.64, 91.1) * mm});
            skLineSegment(sketch, "E1868", {"start": v(-29.64, 89.27) * mm, "end": v(-29.62, 89) * mm});
            skLineSegment(sketch, "E1869", {"start": v(-29.62, 89) * mm, "end": v(-29.52, 88.74) * mm});
            skLineSegment(sketch, "E1870", {"start": v(-29.52, 88.74) * mm, "end": v(-29.35, 88.53) * mm});
            skLineSegment(sketch, "E1871", {"start": v(-29.35, 88.53) * mm, "end": v(-29.11, 88.36) * mm});
            skLineSegment(sketch, "E1872", {"start": v(-29.11, 88.36) * mm, "end": v(-28.86, 88.25) * mm});
            skLineSegment(sketch, "E1873", {"start": v(-28.86, 88.25) * mm, "end": v(-28.59, 88.21) * mm});
            skLineSegment(sketch, "E1874", {"start": v(-28.59, 88.21) * mm, "end": v(-28.33, 88.25) * mm});
            skLineSegment(sketch, "E1875", {"start": v(-28.33, 88.25) * mm, "end": v(-28.06, 88.36) * mm});
            skLineSegment(sketch, "E1876", {"start": v(-28.06, 88.36) * mm, "end": v(-27.84, 88.53) * mm});
            skLineSegment(sketch, "E1877", {"start": v(-27.84, 88.53) * mm, "end": v(-27.68, 88.74) * mm});
            skLineSegment(sketch, "E1878", {"start": v(-27.68, 88.74) * mm, "end": v(-27.57, 89) * mm});
            skLineSegment(sketch, "E1879", {"start": v(-27.57, 89) * mm, "end": v(-27.53, 89.27) * mm});
            skLineSegment(sketch, "E1880", {"start": v(-27.53, 89.27) * mm, "end": v(-27.53, 90.33) * mm});
            skLineSegment(sketch, "E1881", {"start": v(-27.53, 90.33) * mm, "end": v(-27.57, 90.6) * mm});
            skLineSegment(sketch, "E1882", {"start": v(-27.57, 90.6) * mm, "end": v(-27.68, 90.86) * mm});
            skLineSegment(sketch, "E1883", {"start": v(-27.68, 90.86) * mm, "end": v(-27.84, 91.1) * mm});
            skLineSegment(sketch, "E1884", {"start": v(-27.84, 91.1) * mm, "end": v(-28.06, 91.24) * mm});
            skLineSegment(sketch, "E1885", {"start": v(-28.06, 91.24) * mm, "end": v(-28.33, 91.34) * mm});
            skLineSegment(sketch, "E1886", {"start": v(-28.33, 91.34) * mm, "end": v(-28.59, 91.39) * mm});
            skLineSegment(sketch, "E1887", {"start": v(-28.59, 91.39) * mm, "end": v(-28.86, 91.34) * mm});
            skLineSegment(sketch, "E1888", {"start": v(-28.86, 91.34) * mm, "end": v(-29.11, 91.24) * mm});
            skLineSegment(sketch, "E1889", {"start": v(-29.11, 91.24) * mm, "end": v(-29.35, 91.1) * mm});
            skLineSegment(sketch, "E1890", {"start": v(-29.35, 91.1) * mm, "end": v(-29.52, 90.86) * mm});
            skLineSegment(sketch, "E1891", {"start": v(-29.52, 90.86) * mm, "end": v(-29.62, 90.6) * mm});
            skLineSegment(sketch, "E1892", {"start": v(-29.62, 90.6) * mm, "end": v(-29.64, 90.33) * mm});
            skLineSegment(sketch, "E1893", {"start": v(-29.64, 90.33) * mm, "end": v(-29.64, 89.27) * mm});
            skLineSegment(sketch, "E1894", {"start": v(-31.02, 88.5) * mm, "end": v(-31.17, 88.36) * mm});
            skLineSegment(sketch, "E1895", {"start": v(-31.17, 88.36) * mm, "end": v(-31.02, 88.21) * mm});
            skLineSegment(sketch, "E1896", {"start": v(-31.02, 88.21) * mm, "end": v(-30.87, 88.36) * mm});
            skLineSegment(sketch, "E1897", {"start": v(-34.05, 90.63) * mm, "end": v(-34.05, 90.8) * mm});
            skLineSegment(sketch, "E1898", {"start": v(-34.05, 90.8) * mm, "end": v(-33.88, 91.1) * mm});
            skLineSegment(sketch, "E1899", {"start": v(-33.88, 91.1) * mm, "end": v(-33.73, 91.24) * mm});
            skLineSegment(sketch, "E1900", {"start": v(-33.73, 91.24) * mm, "end": v(-33.43, 91.39) * mm});
            skLineSegment(sketch, "E1901", {"start": v(-33.43, 91.39) * mm, "end": v(-32.82, 91.39) * mm});
            skLineSegment(sketch, "E1902", {"start": v(-32.82, 91.39) * mm, "end": v(-32.52, 91.24) * mm});
            skLineSegment(sketch, "E1903", {"start": v(-32.52, 91.24) * mm, "end": v(-32.37, 91.1) * mm});
            skLineSegment(sketch, "E1904", {"start": v(-32.37, 91.1) * mm, "end": v(-32.23, 90.8) * mm});
            skLineSegment(sketch, "E1905", {"start": v(-32.23, 90.8) * mm, "end": v(-32.23, 90.48) * mm});
            skLineSegment(sketch, "E1906", {"start": v(-32.23, 90.48) * mm, "end": v(-32.37, 90.18) * mm});
            skLineSegment(sketch, "E1907", {"start": v(-32.37, 90.18) * mm, "end": v(-32.67, 89.74) * mm});
            skLineSegment(sketch, "E1908", {"start": v(-32.67, 89.74) * mm, "end": v(-34.2, 88.21) * mm});
            skLineSegment(sketch, "E1909", {"start": v(-34.2, 88.21) * mm, "end": v(-32.08, 88.21) * mm});
            skLineSegment(sketch, "E1910", {"start": v(-4.41, 45.35) * mm, "end": v(-4.41, -13.39) * mm});
            skLineSegment(sketch, "E1911", {"start": v(208.31, 56.46) * mm, "end": v(59.09, 56.46) * mm});
            skLineSegment(sketch, "E1912", {"start": v(112.96, 53.9) * mm, "end": v(119.9, 45.65) * mm});
            skLineSegment(sketch, "E1913", {"start": v(110.92, 56.34) * mm, "end": v(111.94, 55.13) * mm});
            skLineSegment(sketch, "E1914", {"start": v(103.77, 64.84) * mm, "end": v(109.89, 57.56) * mm});
            skLineSegment(sketch, "E1915", {"start": v(101.74, 67.28) * mm, "end": v(102.75, 66.07) * mm});
            skLineSegment(sketch, "E1916", {"start": v(93.78, 76.78) * mm, "end": v(100.72, 68.5) * mm});
            skLineSegment(sketch, "E1917", {"start": v(73.95, 21.8) * mm, "end": v(77.37, 23.2) * mm});
            skLineSegment(sketch, "E1918", {"start": v(77.37, 23.2) * mm, "end": v(80.76, 24.7) * mm});
            skLineSegment(sketch, "E1919", {"start": v(80.76, 24.7) * mm, "end": v(84.13, 26.26) * mm});
            skLineSegment(sketch, "E1920", {"start": v(84.13, 26.26) * mm, "end": v(87.45, 27.9) * mm});
            skLineSegment(sketch, "E1921", {"start": v(87.45, 27.9) * mm, "end": v(90.73, 29.62) * mm});
            skLineSegment(sketch, "E1922", {"start": v(90.73, 29.62) * mm, "end": v(93.97, 31.42) * mm});
            skLineSegment(sketch, "E1923", {"start": v(93.97, 31.42) * mm, "end": v(97.17, 33.3) * mm});
            skLineSegment(sketch, "E1924", {"start": v(97.17, 33.3) * mm, "end": v(100.32, 35.23) * mm});
            skLineSegment(sketch, "E1925", {"start": v(100.32, 35.23) * mm, "end": v(103.43, 37.26) * mm});
            skLineSegment(sketch, "E1926", {"start": v(103.43, 37.26) * mm, "end": v(106.5, 39.34) * mm});
            skLineSegment(sketch, "E1927", {"start": v(106.5, 39.34) * mm, "end": v(109.5, 41.5) * mm});
            skLineSegment(sketch, "E1928", {"start": v(109.5, 41.5) * mm, "end": v(112.47, 43.74) * mm});
            skLineSegment(sketch, "E1929", {"start": v(112.47, 43.74) * mm, "end": v(115.4, 46.03) * mm});
            skLineSegment(sketch, "E1930", {"start": v(115.4, 46.03) * mm, "end": v(118.25, 48.4) * mm});
            skLineSegment(sketch, "E1931", {"start": v(118.25, 48.4) * mm, "end": v(121.04, 50.81) * mm});
            skLineSegment(sketch, "E1932", {"start": v(121.04, 50.81) * mm, "end": v(123.8, 53.3) * mm});
            skLineSegment(sketch, "E1933", {"start": v(123.8, 53.3) * mm, "end": v(126.48, 55.87) * mm});
            skLineSegment(sketch, "E1934", {"start": v(126.48, 55.87) * mm, "end": v(129.1, 58.47) * mm});
            skLineSegment(sketch, "E1935", {"start": v(129.1, 58.47) * mm, "end": v(131.67, 61.16) * mm});
            skLineSegment(sketch, "E1936", {"start": v(131.67, 61.16) * mm, "end": v(134.16, 63.9) * mm});
            skLineSegment(sketch, "E1937", {"start": v(134.16, 63.9) * mm, "end": v(136.6, 66.69) * mm});
            skLineSegment(sketch, "E1938", {"start": v(136.6, 66.69) * mm, "end": v(138.97, 69.52) * mm});
            skLineSegment(sketch, "E1939", {"start": v(138.97, 69.52) * mm, "end": v(141.28, 72.42) * mm});
            skLineSegment(sketch, "E1940", {"start": v(141.28, 72.42) * mm, "end": v(143.52, 75.39) * mm});
            skLineSegment(sketch, "E1941", {"start": v(143.52, 75.39) * mm, "end": v(145.7, 78.4) * mm});
            skLineSegment(sketch, "E1942", {"start": v(145.7, 78.4) * mm, "end": v(147.8, 81.44) * mm});
            skLineSegment(sketch, "E1943", {"start": v(-208.33, -330.19) * mm, "end": v(-208.33, -331.1) * mm});
            skLineSegment(sketch, "E1944", {"start": v(-208.33, -331.1) * mm, "end": v(-208.18, -331.1) * mm});
            skLineSegment(sketch, "E1945", {"start": v(-208.18, -331.1) * mm, "end": v(-208.02, -331.01) * mm});
            skLineSegment(sketch, "E1946", {"start": v(-208.02, -331.01) * mm, "end": v(-207.95, -330.95) * mm});
            skLineSegment(sketch, "E1947", {"start": v(-207.95, -330.95) * mm, "end": v(-207.87, -330.8) * mm});
            skLineSegment(sketch, "E1948", {"start": v(-207.87, -330.8) * mm, "end": v(-207.87, -330.57) * mm});
            skLineSegment(sketch, "E1949", {"start": v(-207.87, -330.57) * mm, "end": v(-207.95, -330.42) * mm});
            skLineSegment(sketch, "E1950", {"start": v(-207.95, -330.42) * mm, "end": v(-208.1, -330.27) * mm});
            skLineSegment(sketch, "E1951", {"start": v(-208.1, -330.27) * mm, "end": v(-208.33, -330.19) * mm});
            skLineSegment(sketch, "E1952", {"start": v(-208.33, -330.19) * mm, "end": v(-208.48, -330.19) * mm});
            skLineSegment(sketch, "E1953", {"start": v(-208.48, -330.19) * mm, "end": v(-208.7, -330.27) * mm});
            skLineSegment(sketch, "E1954", {"start": v(-208.7, -330.27) * mm, "end": v(-208.86, -330.42) * mm});
            skLineSegment(sketch, "E1955", {"start": v(-208.86, -330.42) * mm, "end": v(-208.93, -330.57) * mm});
            skLineSegment(sketch, "E1956", {"start": v(-208.93, -330.57) * mm, "end": v(-208.93, -330.8) * mm});
            skLineSegment(sketch, "E1957", {"start": v(-208.93, -330.8) * mm, "end": v(-208.86, -330.95) * mm});
            skLineSegment(sketch, "E1958", {"start": v(-208.86, -330.95) * mm, "end": v(-208.7, -331.1) * mm});
            skLineSegment(sketch, "E1959", {"start": v(-207.87, -329.13) * mm, "end": v(-207.87, -329.66) * mm});
            skLineSegment(sketch, "E1960", {"start": v(-207.34, -329.36) * mm, "end": v(-208.63, -329.36) * mm});
            skLineSegment(sketch, "E1961", {"start": v(-208.63, -329.36) * mm, "end": v(-208.86, -329.43) * mm});
            skLineSegment(sketch, "E1962", {"start": v(-208.86, -329.43) * mm, "end": v(-208.93, -329.6) * mm});
            skLineSegment(sketch, "E1963", {"start": v(-208.93, -329.6) * mm, "end": v(-208.93, -329.74) * mm});
            skLineSegment(sketch, "E1964", {"start": v(-208.1, -328.6) * mm, "end": v(-207.95, -328.45) * mm});
            skLineSegment(sketch, "E1965", {"start": v(-207.95, -328.45) * mm, "end": v(-207.87, -328.3) * mm});
            skLineSegment(sketch, "E1966", {"start": v(-207.87, -328.3) * mm, "end": v(-207.87, -328.07) * mm});
            skLineSegment(sketch, "E1967", {"start": v(-207.87, -328.07) * mm, "end": v(-207.95, -327.92) * mm});
            skLineSegment(sketch, "E1968", {"start": v(-207.95, -327.92) * mm, "end": v(-208.1, -327.78) * mm});
            skLineSegment(sketch, "E1969", {"start": v(-208.1, -327.78) * mm, "end": v(-208.33, -327.7) * mm});
            skLineSegment(sketch, "E1970", {"start": v(-208.33, -327.7) * mm, "end": v(-208.48, -327.7) * mm});
            skLineSegment(sketch, "E1971", {"start": v(-208.48, -327.7) * mm, "end": v(-208.7, -327.78) * mm});
            skLineSegment(sketch, "E1972", {"start": v(-208.7, -327.78) * mm, "end": v(-208.86, -327.92) * mm});
            skLineSegment(sketch, "E1973", {"start": v(-208.86, -327.92) * mm, "end": v(-208.93, -328.07) * mm});
            skLineSegment(sketch, "E1974", {"start": v(-208.93, -328.07) * mm, "end": v(-208.93, -328.3) * mm});
            skLineSegment(sketch, "E1975", {"start": v(-208.93, -328.3) * mm, "end": v(-208.86, -328.45) * mm});
            skLineSegment(sketch, "E1976", {"start": v(-208.86, -328.45) * mm, "end": v(-208.7, -328.6) * mm});
            skLineSegment(sketch, "E1977", {"start": v(-207.87, -328.6) * mm, "end": v(-208.93, -328.6) * mm});
            skLineSegment(sketch, "E1978", {"start": v(-208.93, -326.1) * mm, "end": v(-207.34, -326.1) * mm});
            skLineSegment(sketch, "E1979", {"start": v(-207.34, -326.1) * mm, "end": v(-207.34, -326.63) * mm});
            skLineSegment(sketch, "E1980", {"start": v(-207.34, -326.63) * mm, "end": v(-207.42, -326.87) * mm});
            skLineSegment(sketch, "E1981", {"start": v(-207.42, -326.87) * mm, "end": v(-207.57, -327.01) * mm});
            skLineSegment(sketch, "E1982", {"start": v(-207.57, -327.01) * mm, "end": v(-207.72, -327.1) * mm});
            skLineSegment(sketch, "E1983", {"start": v(-207.72, -327.1) * mm, "end": v(-207.95, -327.16) * mm});
            skLineSegment(sketch, "E1984", {"start": v(-207.95, -327.16) * mm, "end": v(-208.33, -327.16) * mm});
            skLineSegment(sketch, "E1985", {"start": v(-208.33, -327.16) * mm, "end": v(-208.54, -327.1) * mm});
            skLineSegment(sketch, "E1986", {"start": v(-208.54, -327.1) * mm, "end": v(-208.7, -327.01) * mm});
            skLineSegment(sketch, "E1987", {"start": v(-208.7, -327.01) * mm, "end": v(-208.86, -326.87) * mm});
            skLineSegment(sketch, "E1988", {"start": v(-208.86, -326.87) * mm, "end": v(-208.93, -326.63) * mm});
            skLineSegment(sketch, "E1989", {"start": v(-208.93, -326.63) * mm, "end": v(-208.93, -326.1) * mm});
            skLineSegment(sketch, "E1990", {"start": v(122.52, 151.75) * mm, "end": v(127.2, 150.9) * mm});
            skLineSegment(sketch, "E1991", {"start": v(119.4, 152.3) * mm, "end": v(120.96, 152.03) * mm});
            skLineSegment(sketch, "E1992", {"start": v(108.45, 154.23) * mm, "end": v(117.82, 152.58) * mm});
            skLineSegment(sketch, "E1993", {"start": v(105.31, 154.78) * mm, "end": v(106.88, 154.5) * mm});
            skLineSegment(sketch, "E1994", {"start": v(94.37, 156.7) * mm, "end": v(103.75, 155.06) * mm});
            skLineSegment(sketch, "E1995", {"start": v(91.26, 157.26) * mm, "end": v(92.8, 156.98) * mm});
            skLineSegment(sketch, "E1996", {"start": v(80.32, 159.18) * mm, "end": v(89.7, 157.53) * mm});
            skLineSegment(sketch, "E1997", {"start": v(77.18, 159.73) * mm, "end": v(78.75, 159.46) * mm});
            skLineSegment(sketch, "E1998", {"start": v(66.24, 161.66) * mm, "end": v(75.62, 160) * mm});
            skLineSegment(sketch, "E1999", {"start": v(63.1, 162.21) * mm, "end": v(64.67, 161.94) * mm});
            skLineSegment(sketch, "E2000", {"start": v(52.17, 164.16) * mm, "end": v(61.54, 162.49) * mm});
            skLineSegment(sketch, "E2001", {"start": v(49.03, 164.7) * mm, "end": v(50.6, 164.43) * mm});
            skLineSegment(sketch, "E2002", {"start": v(38.09, 166.63) * mm, "end": v(47.47, 164.98) * mm});
            skLineSegment(sketch, "E2003", {"start": v(34.98, 167.18) * mm, "end": v(36.52, 166.9) * mm});
            skLineSegment(sketch, "E2004", {"start": v(24.03, 169.11) * mm, "end": v(33.41, 167.46) * mm});
            skLineSegment(sketch, "E2005", {"start": v(20.9, 169.66) * mm, "end": v(22.47, 169.39) * mm});
            skLineSegment(sketch, "E2006", {"start": v(14.64, 170.76) * mm, "end": v(19.34, 169.94) * mm});
            skLineSegment(sketch, "E2007", {"start": v(14.64, 170.76) * mm, "end": v(59.7, 65.73) * mm});
            skLineSegment(sketch, "E2008", {"start": v(14.64, 51.7) * mm, "end": v(14.64, 7.25) * mm});
            skLineSegment(sketch, "E2009", {"start": v(58.1, 72.13) * mm, "end": v(56.1, 71.26) * mm});
            skLineSegment(sketch, "E2010", {"start": v(56.1, 71.26) * mm, "end": v(59.7, 65.73) * mm});
            skLineSegment(sketch, "E2011", {"start": v(85.06, 86.86) * mm, "end": v(88.1, 83.22) * mm});
            skLineSegment(sketch, "E2012", {"start": v(83, 89.3) * mm, "end": v(84.04, 88.06) * mm});
            skLineSegment(sketch, "E2013", {"start": v(75.87, 97.8) * mm, "end": v(81.99, 90.5) * mm});
            skLineSegment(sketch, "E2014", {"start": v(73.82, 100.23) * mm, "end": v(74.86, 99) * mm});
            skLineSegment(sketch, "E2015", {"start": v(66.69, 108.74) * mm, "end": v(72.8, 101.44) * mm});
            skLineSegment(sketch, "E2016", {"start": v(64.65, 111.18) * mm, "end": v(65.67, 109.97) * mm});
            skLineSegment(sketch, "E2017", {"start": v(57.5, 119.69) * mm, "end": v(63.62, 112.38) * mm});
            skLineSegment(sketch, "E2018", {"start": v(55.47, 122.12) * mm, "end": v(56.48, 120.91) * mm});
            skLineSegment(sketch, "E2019", {"start": v(48.31, 130.63) * mm, "end": v(54.45, 123.35) * mm});
            skLineSegment(sketch, "E2020", {"start": v(46.28, 133.06) * mm, "end": v(47.3, 131.86) * mm});
            skLineSegment(sketch, "E2021", {"start": v(39.13, 141.57) * mm, "end": v(45.26, 134.3) * mm});
            skLineSegment(sketch, "E2022", {"start": v(37.1, 144) * mm, "end": v(38.11, 142.8) * mm});
            skLineSegment(sketch, "E2023", {"start": v(29.94, 152.52) * mm, "end": v(36.08, 145.24) * mm});
            skLineSegment(sketch, "E2024", {"start": v(27.9, 154.95) * mm, "end": v(28.92, 153.74) * mm});
            skLineSegment(sketch, "E2025", {"start": v(20.78, 163.46) * mm, "end": v(26.9, 156.18) * mm});
            skLineSegment(sketch, "E2026", {"start": v(18.72, 165.9) * mm, "end": v(19.74, 164.69) * mm});
            skLineSegment(sketch, "E2027", {"start": v(14.64, 170.76) * mm, "end": v(17.7, 167.12) * mm});
            skLineSegment(sketch, "E2028", {"start": v(53.56, 131.77) * mm, "end": v(54.26, 131.8) * mm});
            skLineSegment(sketch, "E2029", {"start": v(54.26, 131.8) * mm, "end": v(54.98, 131.92) * mm});
            skLineSegment(sketch, "E2030", {"start": v(54.98, 131.92) * mm, "end": v(55.66, 132.11) * mm});
            skLineSegment(sketch, "E2031", {"start": v(55.66, 132.11) * mm, "end": v(56.31, 132.39) * mm});
            skLineSegment(sketch, "E2032", {"start": v(56.31, 132.39) * mm, "end": v(56.93, 132.73) * mm});
            skLineSegment(sketch, "E2033", {"start": v(56.93, 132.73) * mm, "end": v(57.52, 133.15) * mm});
            skLineSegment(sketch, "E2034", {"start": v(57.52, 133.15) * mm, "end": v(58.05, 133.61) * mm});
            skLineSegment(sketch, "E2035", {"start": v(58.05, 133.61) * mm, "end": v(58.52, 134.14) * mm});
            skLineSegment(sketch, "E2036", {"start": v(58.52, 134.14) * mm, "end": v(58.94, 134.74) * mm});
            skLineSegment(sketch, "E2037", {"start": v(58.94, 134.74) * mm, "end": v(59.28, 135.35) * mm});
            skLineSegment(sketch, "E2038", {"start": v(59.28, 135.35) * mm, "end": v(59.55, 136) * mm});
            skLineSegment(sketch, "E2039", {"start": v(59.55, 136) * mm, "end": v(59.74, 136.7) * mm});
            skLineSegment(sketch, "E2040", {"start": v(59.74, 136.7) * mm, "end": v(59.87, 137.4) * mm});
            skLineSegment(sketch, "E2041", {"start": v(59.87, 137.4) * mm, "end": v(59.91, 138.12) * mm});
            skLineSegment(sketch, "E2042", {"start": v(59.91, 138.12) * mm, "end": v(59.87, 138.82) * mm});
            skLineSegment(sketch, "E2043", {"start": v(59.87, 138.82) * mm, "end": v(59.74, 139.52) * mm});
            skLineSegment(sketch, "E2044", {"start": v(59.74, 139.52) * mm, "end": v(59.55, 140.22) * mm});
            skLineSegment(sketch, "E2045", {"start": v(59.55, 140.22) * mm, "end": v(59.28, 140.87) * mm});
            skLineSegment(sketch, "E2046", {"start": v(59.28, 140.87) * mm, "end": v(58.94, 141.49) * mm});
            skLineSegment(sketch, "E2047", {"start": v(58.94, 141.49) * mm, "end": v(58.52, 142.08) * mm});
            skLineSegment(sketch, "E2048", {"start": v(58.52, 142.08) * mm, "end": v(58.05, 142.61) * mm});
            skLineSegment(sketch, "E2049", {"start": v(58.05, 142.61) * mm, "end": v(57.52, 143.08) * mm});
            skLineSegment(sketch, "E2050", {"start": v(57.52, 143.08) * mm, "end": v(56.93, 143.5) * mm});
            skLineSegment(sketch, "E2051", {"start": v(56.93, 143.5) * mm, "end": v(56.31, 143.84) * mm});
            skLineSegment(sketch, "E2052", {"start": v(56.31, 143.84) * mm, "end": v(55.66, 144.11) * mm});
            skLineSegment(sketch, "E2053", {"start": v(55.66, 144.11) * mm, "end": v(54.98, 144.3) * mm});
            skLineSegment(sketch, "E2054", {"start": v(54.98, 144.3) * mm, "end": v(54.26, 144.43) * mm});
            skLineSegment(sketch, "E2055", {"start": v(54.26, 144.43) * mm, "end": v(53.56, 144.47) * mm});
            skLineSegment(sketch, "E2056", {"start": v(53.56, 144.47) * mm, "end": v(52.84, 144.43) * mm});
            skLineSegment(sketch, "E2057", {"start": v(52.84, 144.43) * mm, "end": v(52.14, 144.3) * mm});
            skLineSegment(sketch, "E2058", {"start": v(52.14, 144.3) * mm, "end": v(51.47, 144.11) * mm});
            skLineSegment(sketch, "E2059", {"start": v(51.47, 144.11) * mm, "end": v(50.81, 143.84) * mm});
            skLineSegment(sketch, "E2060", {"start": v(50.81, 143.84) * mm, "end": v(50.18, 143.5) * mm});
            skLineSegment(sketch, "E2061", {"start": v(50.18, 143.5) * mm, "end": v(49.6, 143.08) * mm});
            skLineSegment(sketch, "E2062", {"start": v(49.6, 143.08) * mm, "end": v(49.07, 142.61) * mm});
            skLineSegment(sketch, "E2063", {"start": v(49.07, 142.61) * mm, "end": v(48.59, 142.08) * mm});
            skLineSegment(sketch, "E2064", {"start": v(48.59, 142.08) * mm, "end": v(48.19, 141.49) * mm});
            skLineSegment(sketch, "E2065", {"start": v(48.19, 141.49) * mm, "end": v(47.85, 140.87) * mm});
            skLineSegment(sketch, "E2066", {"start": v(47.85, 140.87) * mm, "end": v(47.57, 140.22) * mm});
            skLineSegment(sketch, "E2067", {"start": v(47.57, 140.22) * mm, "end": v(47.36, 139.52) * mm});
            skLineSegment(sketch, "E2068", {"start": v(47.36, 139.52) * mm, "end": v(47.25, 138.82) * mm});
            skLineSegment(sketch, "E2069", {"start": v(47.25, 138.82) * mm, "end": v(47.21, 138.12) * mm});
            skLineSegment(sketch, "E2070", {"start": v(47.21, 138.12) * mm, "end": v(47.25, 137.4) * mm});
            skLineSegment(sketch, "E2071", {"start": v(47.25, 137.4) * mm, "end": v(47.36, 136.7) * mm});
            skLineSegment(sketch, "E2072", {"start": v(47.36, 136.7) * mm, "end": v(47.57, 136) * mm});
            skLineSegment(sketch, "E2073", {"start": v(47.57, 136) * mm, "end": v(47.85, 135.35) * mm});
            skLineSegment(sketch, "E2074", {"start": v(47.85, 135.35) * mm, "end": v(48.19, 134.74) * mm});
            skLineSegment(sketch, "E2075", {"start": v(48.19, 134.74) * mm, "end": v(48.59, 134.14) * mm});
            skLineSegment(sketch, "E2076", {"start": v(48.59, 134.14) * mm, "end": v(49.07, 133.61) * mm});
            skLineSegment(sketch, "E2077", {"start": v(49.07, 133.61) * mm, "end": v(49.6, 133.15) * mm});
            skLineSegment(sketch, "E2078", {"start": v(49.6, 133.15) * mm, "end": v(50.18, 132.73) * mm});
            skLineSegment(sketch, "E2079", {"start": v(50.18, 132.73) * mm, "end": v(50.81, 132.39) * mm});
            skLineSegment(sketch, "E2080", {"start": v(50.81, 132.39) * mm, "end": v(51.47, 132.11) * mm});
            skLineSegment(sketch, "E2081", {"start": v(51.47, 132.11) * mm, "end": v(52.14, 131.92) * mm});
            skLineSegment(sketch, "E2082", {"start": v(52.14, 131.92) * mm, "end": v(52.84, 131.8) * mm});
            skLineSegment(sketch, "E2083", {"start": v(52.84, 131.8) * mm, "end": v(53.56, 131.77) * mm});
            skLineSegment(sketch, "E2084", {"start": v(63.62, 99.68) * mm, "end": v(64.67, 99.73) * mm});
            skLineSegment(sketch, "E2085", {"start": v(64.67, 99.73) * mm, "end": v(65.71, 99.87) * mm});
            skLineSegment(sketch, "E2086", {"start": v(65.71, 99.87) * mm, "end": v(66.75, 100.09) * mm});
            skLineSegment(sketch, "E2087", {"start": v(66.75, 100.09) * mm, "end": v(67.74, 100.38) * mm});
            skLineSegment(sketch, "E2088", {"start": v(67.74, 100.38) * mm, "end": v(68.72, 100.76) * mm});
            skLineSegment(sketch, "E2089", {"start": v(68.72, 100.76) * mm, "end": v(69.67, 101.23) * mm});
            skLineSegment(sketch, "E2090", {"start": v(69.67, 101.23) * mm, "end": v(70.58, 101.76) * mm});
            skLineSegment(sketch, "E2091", {"start": v(70.58, 101.76) * mm, "end": v(71.43, 102.37) * mm});
            skLineSegment(sketch, "E2092", {"start": v(71.43, 102.37) * mm, "end": v(72.23, 103.05) * mm});
            skLineSegment(sketch, "E2093", {"start": v(72.23, 103.05) * mm, "end": v(72.97, 103.8) * mm});
            skLineSegment(sketch, "E2094", {"start": v(72.97, 103.8) * mm, "end": v(73.65, 104.6) * mm});
            skLineSegment(sketch, "E2095", {"start": v(73.65, 104.6) * mm, "end": v(74.26, 105.44) * mm});
            skLineSegment(sketch, "E2096", {"start": v(74.26, 105.44) * mm, "end": v(74.8, 106.35) * mm});
            skLineSegment(sketch, "E2097", {"start": v(74.8, 106.35) * mm, "end": v(75.26, 107.28) * mm});
            skLineSegment(sketch, "E2098", {"start": v(75.26, 107.28) * mm, "end": v(75.64, 108.28) * mm});
            skLineSegment(sketch, "E2099", {"start": v(75.64, 108.28) * mm, "end": v(75.94, 109.27) * mm});
            skLineSegment(sketch, "E2100", {"start": v(75.94, 109.27) * mm, "end": v(76.15, 110.31) * mm});
            skLineSegment(sketch, "E2101", {"start": v(76.15, 110.31) * mm, "end": v(76.27, 111.35) * mm});
            skLineSegment(sketch, "E2102", {"start": v(76.27, 111.35) * mm, "end": v(76.32, 112.38) * mm});
            skLineSegment(sketch, "E2103", {"start": v(76.32, 112.38) * mm, "end": v(76.27, 113.44) * mm});
            skLineSegment(sketch, "E2104", {"start": v(76.27, 113.44) * mm, "end": v(76.15, 114.48) * mm});
            skLineSegment(sketch, "E2105", {"start": v(76.15, 114.48) * mm, "end": v(75.94, 115.52) * mm});
            skLineSegment(sketch, "E2106", {"start": v(75.94, 115.52) * mm, "end": v(75.64, 116.51) * mm});
            skLineSegment(sketch, "E2107", {"start": v(75.64, 116.51) * mm, "end": v(75.26, 117.49) * mm});
            skLineSegment(sketch, "E2108", {"start": v(75.26, 117.49) * mm, "end": v(74.8, 118.44) * mm});
            skLineSegment(sketch, "E2109", {"start": v(74.8, 118.44) * mm, "end": v(74.26, 119.35) * mm});
            skLineSegment(sketch, "E2110", {"start": v(74.26, 119.35) * mm, "end": v(73.65, 120.2) * mm});
            skLineSegment(sketch, "E2111", {"start": v(73.65, 120.2) * mm, "end": v(72.97, 121) * mm});
            skLineSegment(sketch, "E2112", {"start": v(72.97, 121) * mm, "end": v(72.23, 121.74) * mm});
            skLineSegment(sketch, "E2113", {"start": v(72.23, 121.74) * mm, "end": v(71.43, 122.42) * mm});
            skLineSegment(sketch, "E2114", {"start": v(71.43, 122.42) * mm, "end": v(70.58, 123.03) * mm});
            skLineSegment(sketch, "E2115", {"start": v(70.58, 123.03) * mm, "end": v(69.67, 123.56) * mm});
            skLineSegment(sketch, "E2116", {"start": v(69.67, 123.56) * mm, "end": v(68.72, 124.03) * mm});
            skLineSegment(sketch, "E2117", {"start": v(68.72, 124.03) * mm, "end": v(67.74, 124.4) * mm});
            skLineSegment(sketch, "E2118", {"start": v(67.74, 124.4) * mm, "end": v(66.75, 124.7) * mm});
            skLineSegment(sketch, "E2119", {"start": v(66.75, 124.7) * mm, "end": v(65.71, 124.92) * mm});
            skLineSegment(sketch, "E2120", {"start": v(65.71, 124.92) * mm, "end": v(64.67, 125.04) * mm});
            skLineSegment(sketch, "E2121", {"start": v(64.67, 125.04) * mm, "end": v(63.62, 125.08) * mm});
            skLineSegment(sketch, "E2122", {"start": v(63.62, 125.08) * mm, "end": v(62.58, 125.04) * mm});
            skLineSegment(sketch, "E2123", {"start": v(62.58, 125.04) * mm, "end": v(61.54, 124.92) * mm});
            skLineSegment(sketch, "E2124", {"start": v(61.54, 124.92) * mm, "end": v(60.5, 124.7) * mm});
            skLineSegment(sketch, "E2125", {"start": v(60.5, 124.7) * mm, "end": v(59.51, 124.4) * mm});
            skLineSegment(sketch, "E2126", {"start": v(59.51, 124.4) * mm, "end": v(58.52, 124.03) * mm});
            skLineSegment(sketch, "E2127", {"start": v(58.52, 124.03) * mm, "end": v(57.58, 123.56) * mm});
            skLineSegment(sketch, "E2128", {"start": v(57.58, 123.56) * mm, "end": v(56.67, 123.03) * mm});
            skLineSegment(sketch, "E2129", {"start": v(56.67, 123.03) * mm, "end": v(55.83, 122.42) * mm});
            skLineSegment(sketch, "E2130", {"start": v(55.83, 122.42) * mm, "end": v(55.02, 121.74) * mm});
            skLineSegment(sketch, "E2131", {"start": v(55.02, 121.74) * mm, "end": v(54.28, 121) * mm});
            skLineSegment(sketch, "E2132", {"start": v(54.28, 121) * mm, "end": v(53.6, 120.2) * mm});
            skLineSegment(sketch, "E2133", {"start": v(53.6, 120.2) * mm, "end": v(53, 119.35) * mm});
            skLineSegment(sketch, "E2134", {"start": v(53, 119.35) * mm, "end": v(52.46, 118.44) * mm});
            skLineSegment(sketch, "E2135", {"start": v(52.46, 118.44) * mm, "end": v(52, 117.49) * mm});
            skLineSegment(sketch, "E2136", {"start": v(52, 117.49) * mm, "end": v(51.61, 116.51) * mm});
            skLineSegment(sketch, "E2137", {"start": v(51.61, 116.51) * mm, "end": v(51.32, 115.52) * mm});
            skLineSegment(sketch, "E2138", {"start": v(51.32, 115.52) * mm, "end": v(51.1, 114.48) * mm});
            skLineSegment(sketch, "E2139", {"start": v(51.1, 114.48) * mm, "end": v(50.96, 113.44) * mm});
            skLineSegment(sketch, "E2140", {"start": v(50.96, 113.44) * mm, "end": v(50.92, 112.38) * mm});
            skLineSegment(sketch, "E2141", {"start": v(50.92, 112.38) * mm, "end": v(50.96, 111.35) * mm});
            skLineSegment(sketch, "E2142", {"start": v(50.96, 111.35) * mm, "end": v(51.1, 110.31) * mm});
            skLineSegment(sketch, "E2143", {"start": v(51.1, 110.31) * mm, "end": v(51.32, 109.27) * mm});
            skLineSegment(sketch, "E2144", {"start": v(51.32, 109.27) * mm, "end": v(51.61, 108.28) * mm});
            skLineSegment(sketch, "E2145", {"start": v(51.61, 108.28) * mm, "end": v(52, 107.28) * mm});
            skLineSegment(sketch, "E2146", {"start": v(52, 107.28) * mm, "end": v(52.46, 106.35) * mm});
            skLineSegment(sketch, "E2147", {"start": v(52.46, 106.35) * mm, "end": v(53, 105.44) * mm});
            skLineSegment(sketch, "E2148", {"start": v(53, 105.44) * mm, "end": v(53.6, 104.6) * mm});
            skLineSegment(sketch, "E2149", {"start": v(53.6, 104.6) * mm, "end": v(54.28, 103.8) * mm});
            skLineSegment(sketch, "E2150", {"start": v(54.28, 103.8) * mm, "end": v(55.02, 103.05) * mm});
            skLineSegment(sketch, "E2151", {"start": v(55.02, 103.05) * mm, "end": v(55.83, 102.37) * mm});
            skLineSegment(sketch, "E2152", {"start": v(55.83, 102.37) * mm, "end": v(56.67, 101.76) * mm});
            skLineSegment(sketch, "E2153", {"start": v(56.67, 101.76) * mm, "end": v(57.58, 101.23) * mm});
            skLineSegment(sketch, "E2154", {"start": v(57.58, 101.23) * mm, "end": v(58.52, 100.76) * mm});
            skLineSegment(sketch, "E2155", {"start": v(58.52, 100.76) * mm, "end": v(59.51, 100.38) * mm});
            skLineSegment(sketch, "E2156", {"start": v(59.51, 100.38) * mm, "end": v(60.5, 100.09) * mm});
            skLineSegment(sketch, "E2157", {"start": v(60.5, 100.09) * mm, "end": v(61.54, 99.87) * mm});
            skLineSegment(sketch, "E2158", {"start": v(61.54, 99.87) * mm, "end": v(62.58, 99.73) * mm});
            skLineSegment(sketch, "E2159", {"start": v(62.58, 99.73) * mm, "end": v(63.62, 99.68) * mm});
            skLineSegment(sketch, "E2160", {"start": v(26.93, 105.31) * mm, "end": v(23.9, 106.67) * mm});
            skLineSegment(sketch, "E2161", {"start": v(26.47, 106.22) * mm, "end": v(26.32, 106.52) * mm});
            skLineSegment(sketch, "E2162", {"start": v(26.32, 106.52) * mm, "end": v(26.02, 106.84) * mm});
            skLineSegment(sketch, "E2163", {"start": v(26.02, 106.84) * mm, "end": v(25.56, 106.99) * mm});
            skLineSegment(sketch, "E2164", {"start": v(25.56, 106.99) * mm, "end": v(25.26, 106.99) * mm});
            skLineSegment(sketch, "E2165", {"start": v(25.26, 106.99) * mm, "end": v(24.82, 106.84) * mm});
            skLineSegment(sketch, "E2166", {"start": v(24.82, 106.84) * mm, "end": v(24.5, 106.52) * mm});
            skLineSegment(sketch, "E2167", {"start": v(24.5, 106.52) * mm, "end": v(24.35, 106.22) * mm});
            skLineSegment(sketch, "E2168", {"start": v(24.35, 106.22) * mm, "end": v(24.35, 105.78) * mm});
            skLineSegment(sketch, "E2169", {"start": v(24.35, 105.78) * mm, "end": v(24.5, 105.46) * mm});
            skLineSegment(sketch, "E2170", {"start": v(24.5, 105.46) * mm, "end": v(24.82, 105.17) * mm});
            skLineSegment(sketch, "E2171", {"start": v(24.82, 105.17) * mm, "end": v(25.26, 105.02) * mm});
            skLineSegment(sketch, "E2172", {"start": v(25.26, 105.02) * mm, "end": v(25.56, 105.02) * mm});
            skLineSegment(sketch, "E2173", {"start": v(25.56, 105.02) * mm, "end": v(26.02, 105.17) * mm});
            skLineSegment(sketch, "E2174", {"start": v(26.02, 105.17) * mm, "end": v(26.32, 105.46) * mm});
            skLineSegment(sketch, "E2175", {"start": v(26.32, 105.46) * mm, "end": v(26.47, 105.78) * mm});
            skLineSegment(sketch, "E2176", {"start": v(26.47, 105.78) * mm, "end": v(26.47, 106.22) * mm});
            skLineSegment(sketch, "E2177", {"start": v(26.47, 109.4) * mm, "end": v(26.62, 109.1) * mm});
            skLineSegment(sketch, "E2178", {"start": v(26.62, 109.1) * mm, "end": v(27.08, 108.64) * mm});
            skLineSegment(sketch, "E2179", {"start": v(27.08, 108.64) * mm, "end": v(23.9, 108.64) * mm});
            skLineSegment(sketch, "E2180", {"start": v(27.08, 112.13) * mm, "end": v(27.08, 110.46) * mm});
            skLineSegment(sketch, "E2181", {"start": v(27.08, 110.46) * mm, "end": v(25.88, 111.37) * mm});
            skLineSegment(sketch, "E2182", {"start": v(25.88, 111.37) * mm, "end": v(25.88, 110.9) * mm});
            skLineSegment(sketch, "E2183", {"start": v(25.88, 110.9) * mm, "end": v(25.73, 110.6) * mm});
            skLineSegment(sketch, "E2184", {"start": v(25.73, 110.6) * mm, "end": v(25.56, 110.46) * mm});
            skLineSegment(sketch, "E2185", {"start": v(25.56, 110.46) * mm, "end": v(25.11, 110.31) * mm});
            skLineSegment(sketch, "E2186", {"start": v(25.11, 110.31) * mm, "end": v(24.82, 110.31) * mm});
            skLineSegment(sketch, "E2187", {"start": v(24.82, 110.31) * mm, "end": v(24.35, 110.46) * mm});
            skLineSegment(sketch, "E2188", {"start": v(24.35, 110.46) * mm, "end": v(24.06, 110.75) * mm});
            skLineSegment(sketch, "E2189", {"start": v(24.06, 110.75) * mm, "end": v(23.9, 111.22) * mm});
            skLineSegment(sketch, "E2190", {"start": v(23.9, 111.22) * mm, "end": v(23.9, 111.66) * mm});
            skLineSegment(sketch, "E2191", {"start": v(23.9, 111.66) * mm, "end": v(24.06, 112.13) * mm});
            skLineSegment(sketch, "E2192", {"start": v(24.06, 112.13) * mm, "end": v(24.2, 112.28) * mm});
            skLineSegment(sketch, "E2193", {"start": v(24.2, 112.28) * mm, "end": v(24.5, 112.43) * mm});
            skLineSegment(sketch, "E2194", {"start": v(24.97, 115.45) * mm, "end": v(24.7, 115.41) * mm});
            skLineSegment(sketch, "E2195", {"start": v(24.7, 115.41) * mm, "end": v(24.44, 115.3) * mm});
            skLineSegment(sketch, "E2196", {"start": v(24.44, 115.3) * mm, "end": v(24.2, 115.14) * mm});
            skLineSegment(sketch, "E2197", {"start": v(24.2, 115.14) * mm, "end": v(24.03, 114.92) * mm});
            skLineSegment(sketch, "E2198", {"start": v(24.03, 114.92) * mm, "end": v(23.93, 114.67) * mm});
            skLineSegment(sketch, "E2199", {"start": v(23.93, 114.67) * mm, "end": v(23.9, 114.4) * mm});
            skLineSegment(sketch, "E2200", {"start": v(23.9, 114.4) * mm, "end": v(23.93, 114.12) * mm});
            skLineSegment(sketch, "E2201", {"start": v(23.93, 114.12) * mm, "end": v(24.03, 113.87) * mm});
            skLineSegment(sketch, "E2202", {"start": v(24.03, 113.87) * mm, "end": v(24.2, 113.63) * mm});
            skLineSegment(sketch, "E2203", {"start": v(24.2, 113.63) * mm, "end": v(24.44, 113.46) * mm});
            skLineSegment(sketch, "E2204", {"start": v(24.44, 113.46) * mm, "end": v(24.7, 113.36) * mm});
            skLineSegment(sketch, "E2205", {"start": v(24.7, 113.36) * mm, "end": v(24.97, 113.34) * mm});
            skLineSegment(sketch, "E2206", {"start": v(24.97, 113.34) * mm, "end": v(26.02, 113.34) * mm});
            skLineSegment(sketch, "E2207", {"start": v(26.02, 113.34) * mm, "end": v(26.3, 113.36) * mm});
            skLineSegment(sketch, "E2208", {"start": v(26.3, 113.36) * mm, "end": v(26.55, 113.46) * mm});
            skLineSegment(sketch, "E2209", {"start": v(26.55, 113.46) * mm, "end": v(26.77, 113.63) * mm});
            skLineSegment(sketch, "E2210", {"start": v(26.77, 113.63) * mm, "end": v(26.93, 113.87) * mm});
            skLineSegment(sketch, "E2211", {"start": v(26.93, 113.87) * mm, "end": v(27.04, 114.12) * mm});
            skLineSegment(sketch, "E2212", {"start": v(27.04, 114.12) * mm, "end": v(27.08, 114.4) * mm});
            skLineSegment(sketch, "E2213", {"start": v(27.08, 114.4) * mm, "end": v(27.04, 114.67) * mm});
            skLineSegment(sketch, "E2214", {"start": v(27.04, 114.67) * mm, "end": v(26.93, 114.92) * mm});
            skLineSegment(sketch, "E2215", {"start": v(26.93, 114.92) * mm, "end": v(26.77, 115.14) * mm});
            skLineSegment(sketch, "E2216", {"start": v(26.77, 115.14) * mm, "end": v(26.55, 115.3) * mm});
            skLineSegment(sketch, "E2217", {"start": v(26.55, 115.3) * mm, "end": v(26.3, 115.41) * mm});
            skLineSegment(sketch, "E2218", {"start": v(26.3, 115.41) * mm, "end": v(26.02, 115.45) * mm});
            skLineSegment(sketch, "E2219", {"start": v(26.02, 115.45) * mm, "end": v(24.97, 115.45) * mm});
            skLineSegment(sketch, "E2220", {"start": v(24.2, 116.8) * mm, "end": v(24.06, 116.96) * mm});
            skLineSegment(sketch, "E2221", {"start": v(24.06, 116.96) * mm, "end": v(23.9, 116.8) * mm});
            skLineSegment(sketch, "E2222", {"start": v(23.9, 116.8) * mm, "end": v(24.06, 116.66) * mm});
            skLineSegment(sketch, "E2223", {"start": v(26.47, 119.37) * mm, "end": v(26.62, 119.07) * mm});
            skLineSegment(sketch, "E2224", {"start": v(26.62, 119.07) * mm, "end": v(27.08, 118.63) * mm});
            skLineSegment(sketch, "E2225", {"start": v(27.08, 118.63) * mm, "end": v(23.9, 118.63) * mm});
            skLineSegment(sketch, "E2226", {"start": v(54.15, 88.97) * mm, "end": v(54.3, 89.36) * mm});
            skLineSegment(sketch, "E2227", {"start": v(54.3, 89.36) * mm, "end": v(54.26, 89.84) * mm});
            skLineSegment(sketch, "E2228", {"start": v(54.26, 89.84) * mm, "end": v(54.03, 90.4) * mm});
            skLineSegment(sketch, "E2229", {"start": v(54.03, 90.4) * mm, "end": v(53.71, 90.75) * mm});
            skLineSegment(sketch, "E2230", {"start": v(53.71, 90.75) * mm, "end": v(53.3, 90.9) * mm});
            skLineSegment(sketch, "E2231", {"start": v(53.3, 90.9) * mm, "end": v(53.03, 90.8) * mm});
            skLineSegment(sketch, "E2232", {"start": v(53.03, 90.8) * mm, "end": v(52.82, 90.52) * mm});
            skLineSegment(sketch, "E2233", {"start": v(52.82, 90.52) * mm, "end": v(52.74, 90.33) * mm});
            skLineSegment(sketch, "E2234", {"start": v(52.74, 90.33) * mm, "end": v(52.72, 90) * mm});
            skLineSegment(sketch, "E2235", {"start": v(52.72, 90) * mm, "end": v(52.8, 89.04) * mm});
            skLineSegment(sketch, "E2236", {"start": v(52.8, 89.04) * mm, "end": v(52.78, 88.7) * mm});
            skLineSegment(sketch, "E2237", {"start": v(52.78, 88.7) * mm, "end": v(52.72, 88.5) * mm});
            skLineSegment(sketch, "E2238", {"start": v(52.72, 88.5) * mm, "end": v(52.48, 88.25) * mm});
            skLineSegment(sketch, "E2239", {"start": v(52.48, 88.25) * mm, "end": v(52.08, 88.06) * mm});
            skLineSegment(sketch, "E2240", {"start": v(52.08, 88.06) * mm, "end": v(51.68, 88.21) * mm});
            skLineSegment(sketch, "E2241", {"start": v(51.68, 88.21) * mm, "end": v(51.36, 88.57) * mm});
            skLineSegment(sketch, "E2242", {"start": v(51.36, 88.57) * mm, "end": v(51.1, 89.12) * mm});
            skLineSegment(sketch, "E2243", {"start": v(51.1, 89.12) * mm, "end": v(51.06, 89.6) * mm});
            skLineSegment(sketch, "E2244", {"start": v(51.06, 89.6) * mm, "end": v(51.23, 90.01) * mm});
            skLineSegment(sketch, "E2245", {"start": v(52.4, 94.14) * mm, "end": v(50.32, 93.23) * mm});
            skLineSegment(sketch, "E2246", {"start": v(50.32, 93.23) * mm, "end": v(49.96, 92.91) * mm});
            skLineSegment(sketch, "E2247", {"start": v(49.96, 92.91) * mm, "end": v(49.82, 92.53) * mm});
            skLineSegment(sketch, "E2248", {"start": v(49.82, 92.53) * mm, "end": v(49.86, 92.04) * mm});
            skLineSegment(sketch, "E2249", {"start": v(49.86, 92.04) * mm, "end": v(49.96, 91.77) * mm});
            skLineSegment(sketch, "E2250", {"start": v(49.96, 91.77) * mm, "end": v(50.28, 91.4) * mm});
            skLineSegment(sketch, "E2251", {"start": v(50.28, 91.4) * mm, "end": v(50.68, 91.26) * mm});
            skLineSegment(sketch, "E2252", {"start": v(50.68, 91.26) * mm, "end": v(51.17, 91.3) * mm});
            skLineSegment(sketch, "E2253", {"start": v(51.17, 91.3) * mm, "end": v(53.24, 92.2) * mm});
            skLineSegment(sketch, "E2254", {"start": v(51.45, 96.36) * mm, "end": v(51.91, 95.24) * mm});
            skLineSegment(sketch, "E2255", {"start": v(48.76, 94.54) * mm, "end": v(51.68, 95.81) * mm});
            skLineSegment(sketch, "E2256", {"start": v(48.52, 95.1) * mm, "end": v(49.01, 94) * mm});
            skLineSegment(sketch, "E2257", {"start": v(47.25, 98.01) * mm, "end": v(50.18, 99.26) * mm});
            skLineSegment(sketch, "E2258", {"start": v(50.18, 99.26) * mm, "end": v(50.6, 98.3) * mm});
            skLineSegment(sketch, "E2259", {"start": v(50.6, 98.3) * mm, "end": v(50.64, 97.82) * mm});
            skLineSegment(sketch, "E2260", {"start": v(50.64, 97.82) * mm, "end": v(50.47, 97.42) * mm});
            skLineSegment(sketch, "E2261", {"start": v(50.47, 97.42) * mm, "end": v(50.26, 97.17) * mm});
            skLineSegment(sketch, "E2262", {"start": v(50.26, 97.17) * mm, "end": v(49.9, 96.85) * mm});
            skLineSegment(sketch, "E2263", {"start": v(49.9, 96.85) * mm, "end": v(49.22, 96.55) * mm});
            skLineSegment(sketch, "E2264", {"start": v(49.22, 96.55) * mm, "end": v(48.74, 96.5) * mm});
            skLineSegment(sketch, "E2265", {"start": v(48.74, 96.5) * mm, "end": v(48.4, 96.53) * mm});
            skLineSegment(sketch, "E2266", {"start": v(48.4, 96.53) * mm, "end": v(48, 96.68) * mm});
            skLineSegment(sketch, "E2267", {"start": v(48, 96.68) * mm, "end": v(47.68, 97.04) * mm});
            skLineSegment(sketch, "E2268", {"start": v(47.68, 97.04) * mm, "end": v(47.25, 98.01) * mm});
            skLineSegment(sketch, "E2269", {"start": v(47.09, 101.06) * mm, "end": v(47.7, 99.68) * mm});
            skLineSegment(sketch, "E2270", {"start": v(45.94, 101.06) * mm, "end": v(49.33, 101.2) * mm});
            skLineSegment(sketch, "E2271", {"start": v(49.33, 101.2) * mm, "end": v(46.9, 98.84) * mm});
            skLineSegment(sketch, "E2272", {"start": v(46.62, 103.66) * mm, "end": v(45.52, 102.03) * mm});
            skLineSegment(sketch, "E2273", {"start": v(44.67, 103.96) * mm, "end": v(47.6, 105.23) * mm});
            skLineSegment(sketch, "E2274", {"start": v(47.6, 105.23) * mm, "end": v(48.12, 103.98) * mm});
            skLineSegment(sketch, "E2275", {"start": v(48.12, 103.98) * mm, "end": v(48.16, 103.52) * mm});
            skLineSegment(sketch, "E2276", {"start": v(48.16, 103.52) * mm, "end": v(48.08, 103.3) * mm});
            skLineSegment(sketch, "E2277", {"start": v(48.08, 103.3) * mm, "end": v(47.87, 103.05) * mm});
            skLineSegment(sketch, "E2278", {"start": v(47.87, 103.05) * mm, "end": v(47.6, 102.92) * mm});
            skLineSegment(sketch, "E2279", {"start": v(47.6, 102.92) * mm, "end": v(47.25, 102.94) * mm});
            skLineSegment(sketch, "E2280", {"start": v(47.25, 102.94) * mm, "end": v(47.06, 103.03) * mm});
            skLineSegment(sketch, "E2281", {"start": v(47.06, 103.03) * mm, "end": v(46.75, 103.39) * mm});
            skLineSegment(sketch, "E2282", {"start": v(46.75, 103.39) * mm, "end": v(46.2, 104.64) * mm});
            skLineSegment(sketch, "E2283", {"start": v(42.39, 109.23) * mm, "end": v(43.17, 107.43) * mm});
            skLineSegment(sketch, "E2284", {"start": v(43.91, 109.9) * mm, "end": v(44.4, 108.79) * mm});
            skLineSegment(sketch, "E2285", {"start": v(42.39, 109.23) * mm, "end": v(45.29, 110.5) * mm});
            skLineSegment(sketch, "E2286", {"start": v(45.29, 110.5) * mm, "end": v(46.07, 108.7) * mm});
            skLineSegment(sketch, "E2287", {"start": v(41.05, 112.3) * mm, "end": v(43.97, 113.55) * mm});
            skLineSegment(sketch, "E2288", {"start": v(43.97, 113.55) * mm, "end": v(41.9, 110.35) * mm});
            skLineSegment(sketch, "E2289", {"start": v(41.9, 110.35) * mm, "end": v(44.82, 111.62) * mm});
            skLineSegment(sketch, "E2290", {"start": v(43, 115.77) * mm, "end": v(43.49, 114.67) * mm});
            skLineSegment(sketch, "E2291", {"start": v(40.33, 113.95) * mm, "end": v(43.25, 115.22) * mm});
            skLineSegment(sketch, "E2292", {"start": v(40.1, 114.5) * mm, "end": v(40.57, 113.4) * mm});
            skLineSegment(sketch, "E2293", {"start": v(41.98, 118.12) * mm, "end": v(39.06, 116.87) * mm});
            skLineSegment(sketch, "E2294", {"start": v(39.06, 116.87) * mm, "end": v(39.78, 115.2) * mm});
            skLineSegment(sketch, "E2295", {"start": v(39.76, 119.48) * mm, "end": v(38.64, 117.85) * mm});
            skLineSegment(sketch, "E2296", {"start": v(37.81, 119.77) * mm, "end": v(40.71, 121.04) * mm});
            skLineSegment(sketch, "E2297", {"start": v(40.71, 121.04) * mm, "end": v(41.26, 119.8) * mm});
            skLineSegment(sketch, "E2298", {"start": v(41.26, 119.8) * mm, "end": v(41.3, 119.33) * mm});
            skLineSegment(sketch, "E2299", {"start": v(41.3, 119.33) * mm, "end": v(41.22, 119.12) * mm});
            skLineSegment(sketch, "E2300", {"start": v(41.22, 119.12) * mm, "end": v(41.01, 118.86) * mm});
            skLineSegment(sketch, "E2301", {"start": v(41.01, 118.86) * mm, "end": v(40.74, 118.73) * mm});
            skLineSegment(sketch, "E2302", {"start": v(40.74, 118.73) * mm, "end": v(40.4, 118.76) * mm});
            skLineSegment(sketch, "E2303", {"start": v(40.4, 118.76) * mm, "end": v(40.18, 118.84) * mm});
            skLineSegment(sketch, "E2304", {"start": v(40.18, 118.84) * mm, "end": v(39.87, 119.2) * mm});
            skLineSegment(sketch, "E2305", {"start": v(39.87, 119.2) * mm, "end": v(39.34, 120.45) * mm});
            skLineSegment(sketch, "E2306", {"start": v(36.65, 122.42) * mm, "end": v(37.43, 120.62) * mm});
            skLineSegment(sketch, "E2307", {"start": v(38.2, 123.07) * mm, "end": v(38.66, 121.97) * mm});
            skLineSegment(sketch, "E2308", {"start": v(36.65, 122.42) * mm, "end": v(39.57, 123.69) * mm});
            skLineSegment(sketch, "E2309", {"start": v(39.57, 123.69) * mm, "end": v(40.35, 121.87) * mm});
            skLineSegment(sketch, "E2310", {"start": v(38.5, 126.16) * mm, "end": v(39.34, 124.24) * mm});
            skLineSegment(sketch, "E2311", {"start": v(38.91, 125.21) * mm, "end": v(36, 123.94) * mm});
            skLineSegment(sketch, "E2312", {"start": v(34.26, 127.96) * mm, "end": v(37.16, 129.23) * mm});
            skLineSegment(sketch, "E2313", {"start": v(37.16, 129.23) * mm, "end": v(35.08, 126.02) * mm});
            skLineSegment(sketch, "E2314", {"start": v(35.08, 126.02) * mm, "end": v(38, 127.29) * mm});
            skLineSegment(sketch, "E2315", {"start": v(33.12, 130.59) * mm, "end": v(33.9, 128.79) * mm});
            skLineSegment(sketch, "E2316", {"start": v(34.64, 131.27) * mm, "end": v(35.1, 130.14) * mm});
            skLineSegment(sketch, "E2317", {"start": v(33.12, 130.59) * mm, "end": v(36.02, 131.86) * mm});
            skLineSegment(sketch, "E2318", {"start": v(36.02, 131.86) * mm, "end": v(36.8, 130.06) * mm});
            skLineSegment(sketch, "E2319", {"start": v(34.96, 132.39) * mm, "end": v(35.19, 132.64) * mm});
            skLineSegment(sketch, "E2320", {"start": v(35.19, 132.64) * mm, "end": v(35.34, 133.04) * mm});
            skLineSegment(sketch, "E2321", {"start": v(35.34, 133.04) * mm, "end": v(35.36, 133.38) * mm});
            skLineSegment(sketch, "E2322", {"start": v(35.36, 133.38) * mm, "end": v(35.1, 133.93) * mm});
            skLineSegment(sketch, "E2323", {"start": v(35.1, 133.93) * mm, "end": v(34.85, 134.16) * mm});
            skLineSegment(sketch, "E2324", {"start": v(34.85, 134.16) * mm, "end": v(34.45, 134.31) * mm});
            skLineSegment(sketch, "E2325", {"start": v(34.45, 134.31) * mm, "end": v(34.11, 134.33) * mm});
            skLineSegment(sketch, "E2326", {"start": v(34.11, 134.33) * mm, "end": v(33.64, 134.3) * mm});
            skLineSegment(sketch, "E2327", {"start": v(33.64, 134.3) * mm, "end": v(32.95, 134) * mm});
            skLineSegment(sketch, "E2328", {"start": v(32.95, 134) * mm, "end": v(32.59, 133.68) * mm});
            skLineSegment(sketch, "E2329", {"start": v(32.59, 133.68) * mm, "end": v(32.37, 133.4) * mm});
            skLineSegment(sketch, "E2330", {"start": v(32.37, 133.4) * mm, "end": v(32.23, 133.02) * mm});
            skLineSegment(sketch, "E2331", {"start": v(32.23, 133.02) * mm, "end": v(32.2, 132.68) * mm});
            skLineSegment(sketch, "E2332", {"start": v(32.2, 132.68) * mm, "end": v(32.44, 132.11) * mm});
            skLineSegment(sketch, "E2333", {"start": v(32.44, 132.11) * mm, "end": v(32.71, 131.9) * mm});
            skLineSegment(sketch, "E2334", {"start": v(32.71, 131.9) * mm, "end": v(33.1, 131.75) * mm});
            skLineSegment(sketch, "E2335", {"start": v(33.1, 131.75) * mm, "end": v(33.43, 131.73) * mm});
            skLineSegment(sketch, "E2336", {"start": v(33.6, 138.57) * mm, "end": v(33.41, 138.63) * mm});
            skLineSegment(sketch, "E2337", {"start": v(33.41, 138.63) * mm, "end": v(33.48, 138.84) * mm});
            skLineSegment(sketch, "E2338", {"start": v(33.48, 138.84) * mm, "end": v(33.69, 138.76) * mm});
            skLineSegment(sketch, "E2339", {"start": v(33.69, 138.76) * mm, "end": v(33.6, 138.57) * mm});
            skLineSegment(sketch, "E2340", {"start": v(33.6, 138.57) * mm, "end": v(33.33, 138.44) * mm});
            skLineSegment(sketch, "E2341", {"start": v(33.33, 138.44) * mm, "end": v(32.99, 138.46) * mm});
            skLineSegment(sketch, "E2342", {"start": v(32.99, 138.46) * mm, "end": v(32.8, 138.53) * mm});
            skLineSegment(sketch, "E2343", {"start": v(33.24, 139.4) * mm, "end": v(33.05, 139.48) * mm});
            skLineSegment(sketch, "E2344", {"start": v(33.05, 139.48) * mm, "end": v(33.12, 139.67) * mm});
            skLineSegment(sketch, "E2345", {"start": v(33.12, 139.67) * mm, "end": v(33.33, 139.58) * mm});
            skLineSegment(sketch, "E2346", {"start": v(33.33, 139.58) * mm, "end": v(33.24, 139.4) * mm});
            skLineSegment(sketch, "E2347", {"start": v(33.24, 139.4) * mm, "end": v(32.97, 139.27) * mm});
            skLineSegment(sketch, "E2348", {"start": v(32.97, 139.27) * mm, "end": v(32.63, 139.29) * mm});
            skLineSegment(sketch, "E2349", {"start": v(32.63, 139.29) * mm, "end": v(32.44, 139.37) * mm});
            skLineSegment(sketch, "E2350", {"start": v(32.23, 140.6) * mm, "end": v(31.61, 141.98) * mm});
            skLineSegment(sketch, "E2351", {"start": v(31.61, 141.98) * mm, "end": v(30.32, 141.57) * mm});
            skLineSegment(sketch, "E2352", {"start": v(30.32, 141.57) * mm, "end": v(30.51, 141.5) * mm});
            skLineSegment(sketch, "E2353", {"start": v(30.51, 141.5) * mm, "end": v(30.83, 141.15) * mm});
            skLineSegment(sketch, "E2354", {"start": v(30.83, 141.15) * mm, "end": v(31.02, 140.73) * mm});
            skLineSegment(sketch, "E2355", {"start": v(31.02, 140.73) * mm, "end": v(31.06, 140.26) * mm});
            skLineSegment(sketch, "E2356", {"start": v(31.06, 140.26) * mm, "end": v(30.9, 139.86) * mm});
            skLineSegment(sketch, "E2357", {"start": v(30.9, 139.86) * mm, "end": v(30.53, 139.54) * mm});
            skLineSegment(sketch, "E2358", {"start": v(30.53, 139.54) * mm, "end": v(30.26, 139.41) * mm});
            skLineSegment(sketch, "E2359", {"start": v(30.26, 139.41) * mm, "end": v(29.8, 139.37) * mm});
            skLineSegment(sketch, "E2360", {"start": v(29.8, 139.37) * mm, "end": v(29.39, 139.52) * mm});
            skLineSegment(sketch, "E2361", {"start": v(29.39, 139.52) * mm, "end": v(29.07, 139.88) * mm});
            skLineSegment(sketch, "E2362", {"start": v(29.07, 139.88) * mm, "end": v(28.88, 140.3) * mm});
            skLineSegment(sketch, "E2363", {"start": v(28.88, 140.3) * mm, "end": v(28.84, 140.77) * mm});
            skLineSegment(sketch, "E2364", {"start": v(28.84, 140.77) * mm, "end": v(28.92, 140.98) * mm});
            skLineSegment(sketch, "E2365", {"start": v(28.92, 140.98) * mm, "end": v(29.14, 141.23) * mm});
            skLineSegment(sketch, "E2366", {"start": v(28.33, 142.36) * mm, "end": v(28.12, 142.44) * mm});
            skLineSegment(sketch, "E2367", {"start": v(28.12, 142.44) * mm, "end": v(28.06, 142.25) * mm});
            skLineSegment(sketch, "E2368", {"start": v(28.06, 142.25) * mm, "end": v(28.25, 142.17) * mm});
            skLineSegment(sketch, "E2369", {"start": v(30.3, 145.02) * mm, "end": v(27.38, 143.77) * mm});
            skLineSegment(sketch, "E2370", {"start": v(30.3, 145.02) * mm, "end": v(27.76, 145.57) * mm});
            skLineSegment(sketch, "E2371", {"start": v(27.76, 145.57) * mm, "end": v(28.65, 143.5) * mm});
            skLineSegment(sketch, "E2372", {"start": v(14.64, 61.22) * mm, "end": v(14.64, 56.46) * mm});
            skLineSegment(sketch, "E2373", {"start": v(14.64, 64.4) * mm, "end": v(14.64, 62.81) * mm});
            skLineSegment(sketch, "E2374", {"start": v(14.64, 75.51) * mm, "end": v(14.64, 65.99) * mm});
            skLineSegment(sketch, "E2375", {"start": v(14.64, 78.69) * mm, "end": v(14.64, 77.1) * mm});
            skLineSegment(sketch, "E2376", {"start": v(14.64, 89.8) * mm, "end": v(14.64, 80.27) * mm});
            skLineSegment(sketch, "E2377", {"start": v(14.64, 92.97) * mm, "end": v(14.64, 91.39) * mm});
            skLineSegment(sketch, "E2378", {"start": v(14.64, 104.09) * mm, "end": v(14.64, 94.56) * mm});
            skLineSegment(sketch, "E2379", {"start": v(14.64, 107.26) * mm, "end": v(14.64, 105.67) * mm});
            skLineSegment(sketch, "E2380", {"start": v(14.64, 118.37) * mm, "end": v(14.64, 108.85) * mm});
            skLineSegment(sketch, "E2381", {"start": v(14.64, 121.55) * mm, "end": v(14.64, 119.96) * mm});
            skLineSegment(sketch, "E2382", {"start": v(14.64, 132.66) * mm, "end": v(14.64, 123.14) * mm});
            skLineSegment(sketch, "E2383", {"start": v(14.64, 135.84) * mm, "end": v(14.64, 134.25) * mm});
            skLineSegment(sketch, "E2384", {"start": v(14.64, 146.95) * mm, "end": v(14.64, 137.42) * mm});
            skLineSegment(sketch, "E2385", {"start": v(14.64, 150.12) * mm, "end": v(14.64, 148.54) * mm});
            skLineSegment(sketch, "E2386", {"start": v(14.64, 161.24) * mm, "end": v(14.64, 151.71) * mm});
            skLineSegment(sketch, "E2387", {"start": v(14.64, 164.41) * mm, "end": v(14.64, 162.82) * mm});
            skLineSegment(sketch, "E2388", {"start": v(14.64, 170.76) * mm, "end": v(14.64, 166) * mm});
            skLineSegment(sketch, "E2389", {"start": v(56.55, 146.17) * mm, "end": v(53.54, 147.52) * mm});
            skLineSegment(sketch, "E2390", {"start": v(56.1, 147.08) * mm, "end": v(55.95, 147.37) * mm});
            skLineSegment(sketch, "E2391", {"start": v(55.95, 147.37) * mm, "end": v(55.66, 147.67) * mm});
            skLineSegment(sketch, "E2392", {"start": v(55.66, 147.67) * mm, "end": v(55.2, 147.84) * mm});
            skLineSegment(sketch, "E2393", {"start": v(55.2, 147.84) * mm, "end": v(54.9, 147.84) * mm});
            skLineSegment(sketch, "E2394", {"start": v(54.9, 147.84) * mm, "end": v(54.43, 147.67) * mm});
            skLineSegment(sketch, "E2395", {"start": v(54.43, 147.67) * mm, "end": v(54.13, 147.37) * mm});
            skLineSegment(sketch, "E2396", {"start": v(54.13, 147.37) * mm, "end": v(53.99, 147.08) * mm});
            skLineSegment(sketch, "E2397", {"start": v(53.99, 147.08) * mm, "end": v(53.99, 146.61) * mm});
            skLineSegment(sketch, "E2398", {"start": v(53.99, 146.61) * mm, "end": v(54.13, 146.31) * mm});
            skLineSegment(sketch, "E2399", {"start": v(54.13, 146.31) * mm, "end": v(54.43, 146.02) * mm});
            skLineSegment(sketch, "E2400", {"start": v(54.43, 146.02) * mm, "end": v(54.9, 145.87) * mm});
            skLineSegment(sketch, "E2401", {"start": v(54.9, 145.87) * mm, "end": v(55.2, 145.87) * mm});
            skLineSegment(sketch, "E2402", {"start": v(55.2, 145.87) * mm, "end": v(55.66, 146.02) * mm});
            skLineSegment(sketch, "E2403", {"start": v(55.66, 146.02) * mm, "end": v(55.95, 146.31) * mm});
            skLineSegment(sketch, "E2404", {"start": v(55.95, 146.31) * mm, "end": v(56.1, 146.61) * mm});
            skLineSegment(sketch, "E2405", {"start": v(56.1, 146.61) * mm, "end": v(56.1, 147.08) * mm});
            skLineSegment(sketch, "E2406", {"start": v(56.72, 150.55) * mm, "end": v(56.72, 148.9) * mm});
            skLineSegment(sketch, "E2407", {"start": v(56.72, 148.9) * mm, "end": v(55.49, 149.79) * mm});
            skLineSegment(sketch, "E2408", {"start": v(55.49, 149.79) * mm, "end": v(55.49, 149.34) * mm});
            skLineSegment(sketch, "E2409", {"start": v(55.49, 149.34) * mm, "end": v(55.34, 149.05) * mm});
            skLineSegment(sketch, "E2410", {"start": v(55.34, 149.05) * mm, "end": v(55.2, 148.9) * mm});
            skLineSegment(sketch, "E2411", {"start": v(55.2, 148.9) * mm, "end": v(54.75, 148.73) * mm});
            skLineSegment(sketch, "E2412", {"start": v(54.75, 148.73) * mm, "end": v(54.43, 148.73) * mm});
            skLineSegment(sketch, "E2413", {"start": v(54.43, 148.73) * mm, "end": v(53.99, 148.9) * mm});
            skLineSegment(sketch, "E2414", {"start": v(53.99, 148.9) * mm, "end": v(53.69, 149.2) * mm});
            skLineSegment(sketch, "E2415", {"start": v(53.69, 149.2) * mm, "end": v(53.54, 149.64) * mm});
            skLineSegment(sketch, "E2416", {"start": v(53.54, 149.64) * mm, "end": v(53.54, 150.1) * mm});
            skLineSegment(sketch, "E2417", {"start": v(53.54, 150.1) * mm, "end": v(53.69, 150.55) * mm});
            skLineSegment(sketch, "E2418", {"start": v(53.69, 150.55) * mm, "end": v(53.84, 150.7) * mm});
            skLineSegment(sketch, "E2419", {"start": v(53.84, 150.7) * mm, "end": v(54.13, 150.84) * mm});
            skLineSegment(sketch, "E2420", {"start": v(56.72, 152.07) * mm, "end": v(56.7, 153.57) * mm});
            skLineSegment(sketch, "E2421", {"start": v(56.7, 153.57) * mm, "end": v(55.34, 153.72) * mm});
            skLineSegment(sketch, "E2422", {"start": v(55.34, 153.72) * mm, "end": v(55.49, 153.57) * mm});
            skLineSegment(sketch, "E2423", {"start": v(55.49, 153.57) * mm, "end": v(55.66, 153.13) * mm});
            skLineSegment(sketch, "E2424", {"start": v(55.66, 153.13) * mm, "end": v(55.66, 152.66) * mm});
            skLineSegment(sketch, "E2425", {"start": v(55.66, 152.66) * mm, "end": v(55.49, 152.22) * mm});
            skLineSegment(sketch, "E2426", {"start": v(55.49, 152.22) * mm, "end": v(55.2, 151.9) * mm});
            skLineSegment(sketch, "E2427", {"start": v(55.2, 151.9) * mm, "end": v(54.75, 151.75) * mm});
            skLineSegment(sketch, "E2428", {"start": v(54.75, 151.75) * mm, "end": v(54.43, 151.75) * mm});
            skLineSegment(sketch, "E2429", {"start": v(54.43, 151.75) * mm, "end": v(53.99, 151.9) * mm});
            skLineSegment(sketch, "E2430", {"start": v(53.99, 151.9) * mm, "end": v(53.69, 152.22) * mm});
            skLineSegment(sketch, "E2431", {"start": v(53.69, 152.22) * mm, "end": v(53.54, 152.66) * mm});
            skLineSegment(sketch, "E2432", {"start": v(53.54, 152.66) * mm, "end": v(53.54, 153.13) * mm});
            skLineSegment(sketch, "E2433", {"start": v(53.54, 153.13) * mm, "end": v(53.69, 153.57) * mm});
            skLineSegment(sketch, "E2434", {"start": v(53.69, 153.57) * mm, "end": v(53.84, 153.72) * mm});
            skLineSegment(sketch, "E2435", {"start": v(53.84, 153.72) * mm, "end": v(54.13, 153.87) * mm});
            skLineSegment(sketch, "E2436", {"start": v(53.84, 155.25) * mm, "end": v(53.69, 155.4) * mm});
            skLineSegment(sketch, "E2437", {"start": v(53.69, 155.4) * mm, "end": v(53.52, 155.25) * mm});
            skLineSegment(sketch, "E2438", {"start": v(53.52, 155.25) * mm, "end": v(53.69, 155.08) * mm});
            skLineSegment(sketch, "E2439", {"start": v(19.4, 170.76) * mm, "end": v(9.87, 170.76) * mm});
            skLineSegment(sketch, "E2440", {"start": v(46.87, 143.73) * mm, "end": v(53.56, 138.12) * mm});
            skLineSegment(sketch, "E2441", {"start": v(44.44, 145.76) * mm, "end": v(45.65, 144.75) * mm});
            skLineSegment(sketch, "E2442", {"start": v(35.93, 152.92) * mm, "end": v(43.23, 146.78) * mm});
            skLineSegment(sketch, "E2443", {"start": v(33.5, 154.95) * mm, "end": v(34.7, 153.93) * mm});
            skLineSegment(sketch, "E2444", {"start": v(24.99, 162.08) * mm, "end": v(32.27, 155.97) * mm});
            skLineSegment(sketch, "E2445", {"start": v(22.55, 164.14) * mm, "end": v(23.76, 163.12) * mm});
            skLineSegment(sketch, "E2446", {"start": v(14.64, 170.76) * mm, "end": v(21.33, 165.15) * mm});
            skLineSegment(sketch, "E2447", {"start": v(82.48, 111.94) * mm, "end": v(79.45, 113.3) * mm});
            skLineSegment(sketch, "E2448", {"start": v(82.03, 112.85) * mm, "end": v(81.88, 113.15) * mm});
            skLineSegment(sketch, "E2449", {"start": v(81.88, 113.15) * mm, "end": v(81.57, 113.44) * mm});
            skLineSegment(sketch, "E2450", {"start": v(81.57, 113.44) * mm, "end": v(81.12, 113.6) * mm});
            skLineSegment(sketch, "E2451", {"start": v(81.12, 113.6) * mm, "end": v(80.82, 113.6) * mm});
            skLineSegment(sketch, "E2452", {"start": v(80.82, 113.6) * mm, "end": v(80.36, 113.44) * mm});
            skLineSegment(sketch, "E2453", {"start": v(80.36, 113.44) * mm, "end": v(80.06, 113.15) * mm});
            skLineSegment(sketch, "E2454", {"start": v(80.06, 113.15) * mm, "end": v(79.91, 112.85) * mm});
            skLineSegment(sketch, "E2455", {"start": v(79.91, 112.85) * mm, "end": v(79.91, 112.38) * mm});
            skLineSegment(sketch, "E2456", {"start": v(79.91, 112.38) * mm, "end": v(80.06, 112.09) * mm});
            skLineSegment(sketch, "E2457", {"start": v(80.06, 112.09) * mm, "end": v(80.36, 111.8) * mm});
            skLineSegment(sketch, "E2458", {"start": v(80.36, 111.8) * mm, "end": v(80.82, 111.64) * mm});
            skLineSegment(sketch, "E2459", {"start": v(80.82, 111.64) * mm, "end": v(81.12, 111.64) * mm});
            skLineSegment(sketch, "E2460", {"start": v(81.12, 111.64) * mm, "end": v(81.57, 111.8) * mm});
            skLineSegment(sketch, "E2461", {"start": v(81.57, 111.8) * mm, "end": v(81.88, 112.09) * mm});
            skLineSegment(sketch, "E2462", {"start": v(81.88, 112.09) * mm, "end": v(82.03, 112.38) * mm});
            skLineSegment(sketch, "E2463", {"start": v(82.03, 112.38) * mm, "end": v(82.03, 112.85) * mm});
            skLineSegment(sketch, "E2464", {"start": v(82.03, 116.03) * mm, "end": v(82.18, 115.7) * mm});
            skLineSegment(sketch, "E2465", {"start": v(82.18, 115.7) * mm, "end": v(82.62, 115.26) * mm});
            skLineSegment(sketch, "E2466", {"start": v(82.62, 115.26) * mm, "end": v(79.45, 115.26) * mm});
            skLineSegment(sketch, "E2467", {"start": v(82.62, 118.73) * mm, "end": v(82.62, 117.08) * mm});
            skLineSegment(sketch, "E2468", {"start": v(82.62, 117.08) * mm, "end": v(81.42, 118) * mm});
            skLineSegment(sketch, "E2469", {"start": v(81.42, 118) * mm, "end": v(81.42, 117.53) * mm});
            skLineSegment(sketch, "E2470", {"start": v(81.42, 117.53) * mm, "end": v(81.27, 117.23) * mm});
            skLineSegment(sketch, "E2471", {"start": v(81.27, 117.23) * mm, "end": v(81.12, 117.08) * mm});
            skLineSegment(sketch, "E2472", {"start": v(81.12, 117.08) * mm, "end": v(80.68, 116.94) * mm});
            skLineSegment(sketch, "E2473", {"start": v(80.68, 116.94) * mm, "end": v(80.36, 116.94) * mm});
            skLineSegment(sketch, "E2474", {"start": v(80.36, 116.94) * mm, "end": v(79.91, 117.08) * mm});
            skLineSegment(sketch, "E2475", {"start": v(79.91, 117.08) * mm, "end": v(79.62, 117.38) * mm});
            skLineSegment(sketch, "E2476", {"start": v(79.62, 117.38) * mm, "end": v(79.45, 117.82) * mm});
            skLineSegment(sketch, "E2477", {"start": v(79.45, 117.82) * mm, "end": v(79.45, 118.29) * mm});
            skLineSegment(sketch, "E2478", {"start": v(79.45, 118.29) * mm, "end": v(79.62, 118.73) * mm});
            skLineSegment(sketch, "E2479", {"start": v(79.62, 118.73) * mm, "end": v(79.77, 118.88) * mm});
            skLineSegment(sketch, "E2480", {"start": v(79.77, 118.88) * mm, "end": v(80.06, 119.05) * mm});
            skLineSegment(sketch, "E2481", {"start": v(80.5, 122.06) * mm, "end": v(80.23, 122.04) * mm});
            skLineSegment(sketch, "E2482", {"start": v(80.23, 122.04) * mm, "end": v(79.98, 121.93) * mm});
            skLineSegment(sketch, "E2483", {"start": v(79.98, 121.93) * mm, "end": v(79.77, 121.76) * mm});
            skLineSegment(sketch, "E2484", {"start": v(79.77, 121.76) * mm, "end": v(79.6, 121.53) * mm});
            skLineSegment(sketch, "E2485", {"start": v(79.6, 121.53) * mm, "end": v(79.5, 121.27) * mm});
            skLineSegment(sketch, "E2486", {"start": v(79.5, 121.27) * mm, "end": v(79.45, 121) * mm});
            skLineSegment(sketch, "E2487", {"start": v(79.45, 121) * mm, "end": v(79.5, 120.72) * mm});
            skLineSegment(sketch, "E2488", {"start": v(79.5, 120.72) * mm, "end": v(79.6, 120.47) * mm});
            skLineSegment(sketch, "E2489", {"start": v(79.6, 120.47) * mm, "end": v(79.77, 120.26) * mm});
            skLineSegment(sketch, "E2490", {"start": v(79.77, 120.26) * mm, "end": v(79.98, 120.09) * mm});
            skLineSegment(sketch, "E2491", {"start": v(79.98, 120.09) * mm, "end": v(80.23, 119.98) * mm});
            skLineSegment(sketch, "E2492", {"start": v(80.23, 119.98) * mm, "end": v(80.5, 119.94) * mm});
            skLineSegment(sketch, "E2493", {"start": v(80.5, 119.94) * mm, "end": v(81.57, 119.94) * mm});
            skLineSegment(sketch, "E2494", {"start": v(81.57, 119.94) * mm, "end": v(81.84, 119.98) * mm});
            skLineSegment(sketch, "E2495", {"start": v(81.84, 119.98) * mm, "end": v(82.1, 120.09) * mm});
            skLineSegment(sketch, "E2496", {"start": v(82.1, 120.09) * mm, "end": v(82.33, 120.26) * mm});
            skLineSegment(sketch, "E2497", {"start": v(82.33, 120.26) * mm, "end": v(82.5, 120.47) * mm});
            skLineSegment(sketch, "E2498", {"start": v(82.5, 120.47) * mm, "end": v(82.6, 120.75) * mm});
            skLineSegment(sketch, "E2499", {"start": v(82.6, 120.75) * mm, "end": v(82.62, 121) * mm});
            skLineSegment(sketch, "E2500", {"start": v(82.62, 121) * mm, "end": v(82.6, 121.27) * mm});
            skLineSegment(sketch, "E2501", {"start": v(82.6, 121.27) * mm, "end": v(82.5, 121.53) * mm});
            skLineSegment(sketch, "E2502", {"start": v(82.5, 121.53) * mm, "end": v(82.33, 121.76) * mm});
            skLineSegment(sketch, "E2503", {"start": v(82.33, 121.76) * mm, "end": v(82.1, 121.93) * mm});
            skLineSegment(sketch, "E2504", {"start": v(82.1, 121.93) * mm, "end": v(81.84, 122.04) * mm});
            skLineSegment(sketch, "E2505", {"start": v(81.84, 122.04) * mm, "end": v(81.57, 122.06) * mm});
            skLineSegment(sketch, "E2506", {"start": v(81.57, 122.06) * mm, "end": v(80.5, 122.06) * mm});
            skLineSegment(sketch, "E2507", {"start": v(79.77, 123.43) * mm, "end": v(79.6, 123.58) * mm});
            skLineSegment(sketch, "E2508", {"start": v(79.6, 123.58) * mm, "end": v(79.45, 123.43) * mm});
            skLineSegment(sketch, "E2509", {"start": v(79.45, 123.43) * mm, "end": v(79.6, 123.29) * mm});
            skLineSegment(sketch, "E2510", {"start": v(82.03, 126) * mm, "end": v(82.18, 125.7) * mm});
            skLineSegment(sketch, "E2511", {"start": v(82.18, 125.7) * mm, "end": v(82.62, 125.23) * mm});
            skLineSegment(sketch, "E2512", {"start": v(82.62, 125.23) * mm, "end": v(79.45, 125.23) * mm});
            skLineSegment(sketch, "E2513", {"start": v(89.7, 144.83) * mm, "end": v(90.73, 144.88) * mm});
            skLineSegment(sketch, "E2514", {"start": v(90.73, 144.88) * mm, "end": v(91.77, 145) * mm});
            skLineSegment(sketch, "E2515", {"start": v(91.77, 145) * mm, "end": v(92.8, 145.21) * mm});
            skLineSegment(sketch, "E2516", {"start": v(92.8, 145.21) * mm, "end": v(93.8, 145.53) * mm});
            skLineSegment(sketch, "E2517", {"start": v(93.8, 145.53) * mm, "end": v(94.8, 145.91) * mm});
            skLineSegment(sketch, "E2518", {"start": v(94.8, 145.91) * mm, "end": v(95.73, 146.36) * mm});
            skLineSegment(sketch, "E2519", {"start": v(95.73, 146.36) * mm, "end": v(96.64, 146.9) * mm});
            skLineSegment(sketch, "E2520", {"start": v(96.64, 146.9) * mm, "end": v(97.48, 147.52) * mm});
            skLineSegment(sketch, "E2521", {"start": v(97.48, 147.52) * mm, "end": v(98.29, 148.2) * mm});
            skLineSegment(sketch, "E2522", {"start": v(98.29, 148.2) * mm, "end": v(99.03, 148.94) * mm});
            skLineSegment(sketch, "E2523", {"start": v(99.03, 148.94) * mm, "end": v(99.7, 149.74) * mm});
            skLineSegment(sketch, "E2524", {"start": v(99.7, 149.74) * mm, "end": v(100.32, 150.6) * mm});
            skLineSegment(sketch, "E2525", {"start": v(100.32, 150.6) * mm, "end": v(100.85, 151.48) * mm});
            skLineSegment(sketch, "E2526", {"start": v(100.85, 151.48) * mm, "end": v(101.31, 152.43) * mm});
            skLineSegment(sketch, "E2527", {"start": v(101.31, 152.43) * mm, "end": v(101.7, 153.4) * mm});
            skLineSegment(sketch, "E2528", {"start": v(101.7, 153.4) * mm, "end": v(102, 154.42) * mm});
            skLineSegment(sketch, "E2529", {"start": v(102, 154.42) * mm, "end": v(102.2, 155.44) * mm});
            skLineSegment(sketch, "E2530", {"start": v(102.2, 155.44) * mm, "end": v(102.35, 156.5) * mm});
            skLineSegment(sketch, "E2531", {"start": v(102.35, 156.5) * mm, "end": v(102.4, 157.53) * mm});
            skLineSegment(sketch, "E2532", {"start": v(102.4, 157.53) * mm, "end": v(102.35, 158.6) * mm});
            skLineSegment(sketch, "E2533", {"start": v(102.35, 158.6) * mm, "end": v(102.2, 159.63) * mm});
            skLineSegment(sketch, "E2534", {"start": v(102.2, 159.63) * mm, "end": v(102, 160.64) * mm});
            skLineSegment(sketch, "E2535", {"start": v(102, 160.64) * mm, "end": v(101.7, 161.66) * mm});
            skLineSegment(sketch, "E2536", {"start": v(101.7, 161.66) * mm, "end": v(101.31, 162.63) * mm});
            skLineSegment(sketch, "E2537", {"start": v(101.31, 162.63) * mm, "end": v(100.85, 163.59) * mm});
            skLineSegment(sketch, "E2538", {"start": v(100.85, 163.59) * mm, "end": v(100.32, 164.48) * mm});
            skLineSegment(sketch, "E2539", {"start": v(100.32, 164.48) * mm, "end": v(99.7, 165.34) * mm});
            skLineSegment(sketch, "E2540", {"start": v(99.7, 165.34) * mm, "end": v(99.03, 166.13) * mm});
            skLineSegment(sketch, "E2541", {"start": v(99.03, 166.13) * mm, "end": v(98.29, 166.87) * mm});
            skLineSegment(sketch, "E2542", {"start": v(98.29, 166.87) * mm, "end": v(97.48, 167.57) * mm});
            skLineSegment(sketch, "E2543", {"start": v(97.48, 167.57) * mm, "end": v(96.64, 168.16) * mm});
            skLineSegment(sketch, "E2544", {"start": v(96.64, 168.16) * mm, "end": v(95.73, 168.7) * mm});
            skLineSegment(sketch, "E2545", {"start": v(95.73, 168.7) * mm, "end": v(94.8, 169.17) * mm});
            skLineSegment(sketch, "E2546", {"start": v(94.8, 169.17) * mm, "end": v(93.8, 169.56) * mm});
            skLineSegment(sketch, "E2547", {"start": v(93.8, 169.56) * mm, "end": v(92.8, 169.85) * mm});
            skLineSegment(sketch, "E2548", {"start": v(92.8, 169.85) * mm, "end": v(91.77, 170.06) * mm});
            skLineSegment(sketch, "E2549", {"start": v(91.77, 170.06) * mm, "end": v(90.73, 170.2) * mm});
            skLineSegment(sketch, "E2550", {"start": v(90.73, 170.2) * mm, "end": v(89.7, 170.23) * mm});
            skLineSegment(sketch, "E2551", {"start": v(89.7, 170.23) * mm, "end": v(88.64, 170.2) * mm});
            skLineSegment(sketch, "E2552", {"start": v(88.64, 170.2) * mm, "end": v(87.6, 170.06) * mm});
            skLineSegment(sketch, "E2553", {"start": v(87.6, 170.06) * mm, "end": v(86.56, 169.85) * mm});
            skLineSegment(sketch, "E2554", {"start": v(86.56, 169.85) * mm, "end": v(85.57, 169.56) * mm});
            skLineSegment(sketch, "E2555", {"start": v(85.57, 169.56) * mm, "end": v(84.6, 169.17) * mm});
            skLineSegment(sketch, "E2556", {"start": v(84.6, 169.17) * mm, "end": v(83.64, 168.7) * mm});
            skLineSegment(sketch, "E2557", {"start": v(83.64, 168.7) * mm, "end": v(82.75, 168.16) * mm});
            skLineSegment(sketch, "E2558", {"start": v(82.75, 168.16) * mm, "end": v(81.88, 167.57) * mm});
            skLineSegment(sketch, "E2559", {"start": v(81.88, 167.57) * mm, "end": v(81.08, 166.87) * mm});
            skLineSegment(sketch, "E2560", {"start": v(81.08, 166.87) * mm, "end": v(80.34, 166.13) * mm});
            skLineSegment(sketch, "E2561", {"start": v(80.34, 166.13) * mm, "end": v(79.66, 165.34) * mm});
            skLineSegment(sketch, "E2562", {"start": v(79.66, 165.34) * mm, "end": v(79.05, 164.48) * mm});
            skLineSegment(sketch, "E2563", {"start": v(79.05, 164.48) * mm, "end": v(78.52, 163.59) * mm});
            skLineSegment(sketch, "E2564", {"start": v(78.52, 163.59) * mm, "end": v(78.05, 162.63) * mm});
            skLineSegment(sketch, "E2565", {"start": v(78.05, 162.63) * mm, "end": v(77.67, 161.66) * mm});
            skLineSegment(sketch, "E2566", {"start": v(77.67, 161.66) * mm, "end": v(77.37, 160.64) * mm});
            skLineSegment(sketch, "E2567", {"start": v(77.37, 160.64) * mm, "end": v(77.16, 159.63) * mm});
            skLineSegment(sketch, "E2568", {"start": v(77.16, 159.63) * mm, "end": v(77.04, 158.6) * mm});
            skLineSegment(sketch, "E2569", {"start": v(77.04, 158.6) * mm, "end": v(77, 157.53) * mm});
            skLineSegment(sketch, "E2570", {"start": v(77, 157.53) * mm, "end": v(77.04, 156.5) * mm});
            skLineSegment(sketch, "E2571", {"start": v(77.04, 156.5) * mm, "end": v(77.16, 155.44) * mm});
            skLineSegment(sketch, "E2572", {"start": v(77.16, 155.44) * mm, "end": v(77.37, 154.42) * mm});
            skLineSegment(sketch, "E2573", {"start": v(77.37, 154.42) * mm, "end": v(77.67, 153.4) * mm});
            skLineSegment(sketch, "E2574", {"start": v(77.67, 153.4) * mm, "end": v(78.05, 152.43) * mm});
            skLineSegment(sketch, "E2575", {"start": v(78.05, 152.43) * mm, "end": v(78.52, 151.48) * mm});
            skLineSegment(sketch, "E2576", {"start": v(78.52, 151.48) * mm, "end": v(79.05, 150.6) * mm});
            skLineSegment(sketch, "E2577", {"start": v(79.05, 150.6) * mm, "end": v(79.66, 149.74) * mm});
            skLineSegment(sketch, "E2578", {"start": v(79.66, 149.74) * mm, "end": v(80.34, 148.94) * mm});
            skLineSegment(sketch, "E2579", {"start": v(80.34, 148.94) * mm, "end": v(81.08, 148.2) * mm});
            skLineSegment(sketch, "E2580", {"start": v(81.08, 148.2) * mm, "end": v(81.88, 147.52) * mm});
            skLineSegment(sketch, "E2581", {"start": v(81.88, 147.52) * mm, "end": v(82.75, 146.9) * mm});
            skLineSegment(sketch, "E2582", {"start": v(82.75, 146.9) * mm, "end": v(83.64, 146.36) * mm});
            skLineSegment(sketch, "E2583", {"start": v(83.64, 146.36) * mm, "end": v(84.6, 145.91) * mm});
            skLineSegment(sketch, "E2584", {"start": v(84.6, 145.91) * mm, "end": v(85.57, 145.53) * mm});
            skLineSegment(sketch, "E2585", {"start": v(85.57, 145.53) * mm, "end": v(86.56, 145.21) * mm});
            skLineSegment(sketch, "E2586", {"start": v(86.56, 145.21) * mm, "end": v(87.6, 145) * mm});
            skLineSegment(sketch, "E2587", {"start": v(87.6, 145) * mm, "end": v(88.64, 144.88) * mm});
            skLineSegment(sketch, "E2588", {"start": v(88.64, 144.88) * mm, "end": v(89.7, 144.83) * mm});
            skLineSegment(sketch, "E2589", {"start": v(128.94, 50.11) * mm, "end": v(128.94, -13.39) * mm});
            skLineSegment(sketch, "E2590", {"start": v(71.22, 16.88) * mm, "end": v(71.36, 16.92) * mm});
            skLineSegment(sketch, "E2591", {"start": v(71.36, 16.92) * mm, "end": v(71.47, 17.03) * mm});
            skLineSegment(sketch, "E2592", {"start": v(71.47, 17.03) * mm, "end": v(71.51, 17.18) * mm});
            skLineSegment(sketch, "E2593", {"start": v(71.51, 17.18) * mm, "end": v(71.47, 17.32) * mm});
            skLineSegment(sketch, "E2594", {"start": v(71.47, 17.32) * mm, "end": v(71.36, 17.43) * mm});
            skLineSegment(sketch, "E2595", {"start": v(71.36, 17.43) * mm, "end": v(71.22, 17.47) * mm});
            skLineSegment(sketch, "E2596", {"start": v(71.22, 17.47) * mm, "end": v(71.05, 17.43) * mm});
            skLineSegment(sketch, "E2597", {"start": v(71.05, 17.43) * mm, "end": v(70.94, 17.32) * mm});
            skLineSegment(sketch, "E2598", {"start": v(70.94, 17.32) * mm, "end": v(70.9, 17.18) * mm});
            skLineSegment(sketch, "E2599", {"start": v(70.9, 17.18) * mm, "end": v(70.94, 17.03) * mm});
            skLineSegment(sketch, "E2600", {"start": v(70.94, 17.03) * mm, "end": v(71.05, 16.92) * mm});
            skLineSegment(sketch, "E2601", {"start": v(71.05, 16.92) * mm, "end": v(71.22, 16.88) * mm});
            skLineSegment(sketch, "E2602", {"start": v(69.4, 20.5) * mm, "end": v(69.12, 20.46) * mm});
            skLineSegment(sketch, "E2603", {"start": v(69.12, 20.46) * mm, "end": v(68.87, 20.35) * mm});
            skLineSegment(sketch, "E2604", {"start": v(68.87, 20.35) * mm, "end": v(68.65, 20.18) * mm});
            skLineSegment(sketch, "E2605", {"start": v(68.65, 20.18) * mm, "end": v(68.48, 19.97) * mm});
            skLineSegment(sketch, "E2606", {"start": v(68.48, 19.97) * mm, "end": v(68.38, 19.72) * mm});
            skLineSegment(sketch, "E2607", {"start": v(68.38, 19.72) * mm, "end": v(68.34, 19.44) * mm});
            skLineSegment(sketch, "E2608", {"start": v(68.34, 19.44) * mm, "end": v(68.38, 19.17) * mm});
            skLineSegment(sketch, "E2609", {"start": v(68.38, 19.17) * mm, "end": v(68.48, 18.91) * mm});
            skLineSegment(sketch, "E2610", {"start": v(68.48, 18.91) * mm, "end": v(68.65, 18.7) * mm});
            skLineSegment(sketch, "E2611", {"start": v(68.65, 18.7) * mm, "end": v(68.87, 18.53) * mm});
            skLineSegment(sketch, "E2612", {"start": v(68.87, 18.53) * mm, "end": v(69.12, 18.43) * mm});
            skLineSegment(sketch, "E2613", {"start": v(69.12, 18.43) * mm, "end": v(69.4, 18.38) * mm});
            skLineSegment(sketch, "E2614", {"start": v(69.4, 18.38) * mm, "end": v(70.45, 18.38) * mm});
            skLineSegment(sketch, "E2615", {"start": v(70.45, 18.38) * mm, "end": v(70.73, 18.43) * mm});
            skLineSegment(sketch, "E2616", {"start": v(70.73, 18.43) * mm, "end": v(70.98, 18.53) * mm});
            skLineSegment(sketch, "E2617", {"start": v(70.98, 18.53) * mm, "end": v(71.2, 18.7) * mm});
            skLineSegment(sketch, "E2618", {"start": v(71.2, 18.7) * mm, "end": v(71.36, 18.91) * mm});
            skLineSegment(sketch, "E2619", {"start": v(71.36, 18.91) * mm, "end": v(71.47, 19.17) * mm});
            skLineSegment(sketch, "E2620", {"start": v(71.47, 19.17) * mm, "end": v(71.51, 19.44) * mm});
            skLineSegment(sketch, "E2621", {"start": v(71.51, 19.44) * mm, "end": v(71.47, 19.72) * mm});
            skLineSegment(sketch, "E2622", {"start": v(71.47, 19.72) * mm, "end": v(71.36, 19.97) * mm});
            skLineSegment(sketch, "E2623", {"start": v(71.36, 19.97) * mm, "end": v(71.2, 20.18) * mm});
            skLineSegment(sketch, "E2624", {"start": v(71.2, 20.18) * mm, "end": v(70.98, 20.35) * mm});
            skLineSegment(sketch, "E2625", {"start": v(70.98, 20.35) * mm, "end": v(70.73, 20.46) * mm});
            skLineSegment(sketch, "E2626", {"start": v(70.73, 20.46) * mm, "end": v(70.45, 20.5) * mm});
            skLineSegment(sketch, "E2627", {"start": v(70.45, 20.5) * mm, "end": v(69.4, 20.5) * mm});
            skLineSegment(sketch, "E2628", {"start": v(71.51, 22.02) * mm, "end": v(68.34, 22.02) * mm});
            skLineSegment(sketch, "E2629", {"start": v(71.51, 22.02) * mm, "end": v(69.4, 23.53) * mm});
            skLineSegment(sketch, "E2630", {"start": v(69.4, 23.53) * mm, "end": v(69.4, 21.26) * mm});
            skLineSegment(sketch, "E2631", {"start": v(114.76, 46.5) * mm, "end": v(115.43, 45.56) * mm});
            skLineSegment(sketch, "E2632", {"start": v(115.43, 45.56) * mm, "end": v(117.87, 48.06) * mm});
            skLineSegment(sketch, "E2633", {"start": v(152.11, 82.3) * mm, "end": v(152.26, 82.35) * mm});
            skLineSegment(sketch, "E2634", {"start": v(152.26, 82.35) * mm, "end": v(152.37, 82.45) * mm});
            skLineSegment(sketch, "E2635", {"start": v(152.37, 82.45) * mm, "end": v(152.41, 82.6) * mm});
            skLineSegment(sketch, "E2636", {"start": v(152.41, 82.6) * mm, "end": v(152.37, 82.75) * mm});
            skLineSegment(sketch, "E2637", {"start": v(152.37, 82.75) * mm, "end": v(152.26, 82.88) * mm});
            skLineSegment(sketch, "E2638", {"start": v(152.26, 82.88) * mm, "end": v(152.11, 82.92) * mm});
            skLineSegment(sketch, "E2639", {"start": v(152.11, 82.92) * mm, "end": v(151.97, 82.88) * mm});
            skLineSegment(sketch, "E2640", {"start": v(151.97, 82.88) * mm, "end": v(151.86, 82.75) * mm});
            skLineSegment(sketch, "E2641", {"start": v(151.86, 82.75) * mm, "end": v(151.82, 82.6) * mm});
            skLineSegment(sketch, "E2642", {"start": v(151.82, 82.6) * mm, "end": v(151.86, 82.45) * mm});
            skLineSegment(sketch, "E2643", {"start": v(151.86, 82.45) * mm, "end": v(151.97, 82.35) * mm});
            skLineSegment(sketch, "E2644", {"start": v(151.97, 82.35) * mm, "end": v(152.11, 82.3) * mm});
            skLineSegment(sketch, "E2645", {"start": v(150.3, 85.93) * mm, "end": v(150.02, 85.9) * mm});
            skLineSegment(sketch, "E2646", {"start": v(150.02, 85.9) * mm, "end": v(149.76, 85.8) * mm});
            skLineSegment(sketch, "E2647", {"start": v(149.76, 85.8) * mm, "end": v(149.55, 85.63) * mm});
            skLineSegment(sketch, "E2648", {"start": v(149.55, 85.63) * mm, "end": v(149.38, 85.4) * mm});
            skLineSegment(sketch, "E2649", {"start": v(149.38, 85.4) * mm, "end": v(149.28, 85.14) * mm});
            skLineSegment(sketch, "E2650", {"start": v(149.28, 85.14) * mm, "end": v(149.24, 84.87) * mm});
            skLineSegment(sketch, "E2651", {"start": v(149.24, 84.87) * mm, "end": v(149.28, 84.6) * mm});
            skLineSegment(sketch, "E2652", {"start": v(149.28, 84.6) * mm, "end": v(149.38, 84.34) * mm});
            skLineSegment(sketch, "E2653", {"start": v(149.38, 84.34) * mm, "end": v(149.55, 84.13) * mm});
            skLineSegment(sketch, "E2654", {"start": v(149.55, 84.13) * mm, "end": v(149.76, 83.96) * mm});
            skLineSegment(sketch, "E2655", {"start": v(149.76, 83.96) * mm, "end": v(150.02, 83.85) * mm});
            skLineSegment(sketch, "E2656", {"start": v(150.02, 83.85) * mm, "end": v(150.3, 83.8) * mm});
            skLineSegment(sketch, "E2657", {"start": v(150.3, 83.8) * mm, "end": v(151.35, 83.8) * mm});
            skLineSegment(sketch, "E2658", {"start": v(151.35, 83.8) * mm, "end": v(151.63, 83.85) * mm});
            skLineSegment(sketch, "E2659", {"start": v(151.63, 83.85) * mm, "end": v(151.88, 83.96) * mm});
            skLineSegment(sketch, "E2660", {"start": v(151.88, 83.96) * mm, "end": v(152.11, 84.13) * mm});
            skLineSegment(sketch, "E2661", {"start": v(152.11, 84.13) * mm, "end": v(152.26, 84.34) * mm});
            skLineSegment(sketch, "E2662", {"start": v(152.26, 84.34) * mm, "end": v(152.37, 84.6) * mm});
            skLineSegment(sketch, "E2663", {"start": v(152.37, 84.6) * mm, "end": v(152.41, 84.87) * mm});
            skLineSegment(sketch, "E2664", {"start": v(152.41, 84.87) * mm, "end": v(152.37, 85.14) * mm});
            skLineSegment(sketch, "E2665", {"start": v(152.37, 85.14) * mm, "end": v(152.26, 85.4) * mm});
            skLineSegment(sketch, "E2666", {"start": v(152.26, 85.4) * mm, "end": v(152.11, 85.63) * mm});
            skLineSegment(sketch, "E2667", {"start": v(152.11, 85.63) * mm, "end": v(151.88, 85.8) * mm});
            skLineSegment(sketch, "E2668", {"start": v(151.88, 85.8) * mm, "end": v(151.63, 85.9) * mm});
            skLineSegment(sketch, "E2669", {"start": v(151.63, 85.9) * mm, "end": v(151.35, 85.93) * mm});
            skLineSegment(sketch, "E2670", {"start": v(151.35, 85.93) * mm, "end": v(150.3, 85.93) * mm});
            skLineSegment(sketch, "E2671", {"start": v(152.41, 87.45) * mm, "end": v(149.24, 87.45) * mm});
            skLineSegment(sketch, "E2672", {"start": v(152.41, 87.45) * mm, "end": v(150.3, 88.95) * mm});
            skLineSegment(sketch, "E2673", {"start": v(150.3, 88.95) * mm, "end": v(150.3, 86.69) * mm});
            skLineSegment(sketch, "E2674", {"start": v(128.94, 113.61) * mm, "end": v(128.94, 62.81) * mm});
            skLineSegment(sketch, "E2675", {"start": v(165.03, 143.25) * mm, "end": v(175.65, 141.36) * mm});
            skLineSegment(sketch, "E2676", {"start": v(161.9, 143.8) * mm, "end": v(163.46, 143.52) * mm});
            skLineSegment(sketch, "E2677", {"start": v(150.95, 145.72) * mm, "end": v(160.33, 144.07) * mm});
            skLineSegment(sketch, "E2678", {"start": v(147.82, 146.27) * mm, "end": v(149.38, 146) * mm});
            skLineSegment(sketch, "E2679", {"start": v(135.63, 148.43) * mm, "end": v(146.27, 146.55) * mm});
            skLineSegment(sketch, "E2680", {"start": v(120.77, 49.99) * mm, "end": v(119.98, 50.81) * mm});
            skLineSegment(sketch, "E2681", {"start": v(119.98, 50.81) * mm, "end": v(117.87, 48.06) * mm});
            skSolve(sketch);
        }
        {
            var Q0;
            Q0=qCreatedBy(makeId("Top.planeOp"),FACE);
            var sketch = newSketch(context, id + "F3", { "sketchPlane" : qUnion([Q0])});
            skCircle(sketch, "E2682", {"center": v(0, -76.2) * mm, "radius": 13.1 * mm});
            skSolve(sketch);
        }
        {
            var Q0;
            Q0 = qSketchRegion(id + "F3", true);
            extrude(context, id + "F4", {"entities" : qUnion([Q0]), "operationType" : NewBodyOperationType.REMOVE, "endBound" : BoundingType.SYMMETRIC, "depth" : 127 * mm, "offsetDistance" : 25.4 * mm});
        }
        {
            var Q0;
            Q0=qCreatedBy(makeId("Front.planeOp"),FACE);
            var sketch = newSketch(context, id + "F5", { "sketchPlane" : qUnion([Q0])});
            skLineSegment(sketch, "E2683", {"start": v(114.3, 25.4) * mm, "end": v(114.3, -25.4) * mm, "construction": true});
            skCircle(sketch, "E2684", {"center": v(114.3, 0) * mm, "radius": 15.88 * mm});
            skSolve(sketch);
        }
        {
            var Q0;
            Q0=makeQuery(id+"F5.imprint","IMPRINT",FACE,{"disambiguationData":[TD([[makeQuery(id+"F5.imprint","IMPRINT",EDGE,{"derivedFrom":sQuery(id+"F5.wireOp",EDGE,"E2684")}),1.0]])]});
            var Q1;
            Q1=sQuery(id+"F5.wireOp",EDGE,"E2684");
            var Q2;
            Q2=makeQuery(id+"F1.opExtrude","SWEPT_FACE",FACE,{"disambiguationData":[OSD([sQuery(id+"F0.wireOp",EDGE,"E1")])]});
            revolve(context, id + "F6", {"operationType" : NewBodyOperationType.REMOVE, "entities" : qUnion([Q0]), "surfaceEntities" : qUnion([Q1]), "axis" : qUnion([Q2]), "revolveType" : RevolveType.FULL, "oppositeDirection" : true});
        }
        {
            var Q0;
            Q0=qCreatedBy(makeId("Top.planeOp"),FACE);
            var sketch = newSketch(context, id + "F7", { "sketchPlane" : qUnion([Q0])});
            skLineSegment(sketch, "E2685.0", {"start": v(-19.05, -6) * mm, "end": v(-19.05, -112.7) * mm, "construction": true});
            skLineSegment(sketch, "E2686.bottom", {"start": v(-19.05, -39.68) * mm, "end": v(-114.3, -39.68) * mm});
            skLineSegment(sketch, "E2686.top", {"start": v(-19.05, -90.48) * mm, "end": v(-114.3, -90.48) * mm});
            skLineSegment(sketch, "E2686.left", {"start": v(-19.05, -39.68) * mm, "end": v(-19.05, -90.48) * mm});
            skLineSegment(sketch, "E2686.right", {"start": v(-114.3, -39.68) * mm, "end": v(-114.3, -90.48) * mm});
            skPoint(sketch, "E2687.0", {"position": v(-55.2, 107.26) * mm});
            skPoint(sketch, "E2688.0", {"position": v(14.64, 170.76) * mm});
            skCircle(sketch, "E2689", {"center": v(-69.85, -63.5) * mm, "radius": 12.37 * mm});
            skSolve(sketch);
        }
        {
            var Q0;
            Q0 = qSketchRegion(id + "F7", true);
            extrude(context, id + "F8", {"entities" : qUnion([Q0]), "operationType" : NewBodyOperationType.ADD, "endBound" : BoundingType.SYMMETRIC, "depth" : 31.75 * mm, "offsetDistance" : 25.4 * mm});
        }
        {
            var Q0;
            Q0=makeQuery(id+"F1.opExtrude","SWEPT_EDGE",EDGE,{"disambiguationData":[OSD([sQuery(id+"F0.wireOp",EDGE,"E4.0"),sQuery(id+"F0.wireOp",EDGE,"E4.1")])]});
            fillet(context, id + "F9", {"entities" : qUnion([Q0]), "radius" : 12.7 * mm, "tangentPropagation" : true, "allowEdgeOverflow" : false});
        }
        {
            var Q0;
            Q0=qCreatedBy(makeId("Front.planeOp"),FACE);
            var sketch = newSketch(context, id + "F10", { "sketchPlane" : qUnion([Q0])});
            skCircle(sketch, "E2690", {"center": v(-137.68, 0) * mm, "radius": 15.88 * mm});
            skCircle(sketch, "E2691", {"center": v(-137.68, 0) * mm, "radius": 12.7 * mm});
            skSolve(sketch);
        }
        {
            var Q0;
            Q0 = qSketchRegion(id + "F10", true);
            extrude(context, id + "F11", {"entities" : qUnion([Q0]), "depth" : 914.4 * mm, "offsetDistance" : 25.4 * mm});
        }
        {
            var Q0;
            Q0=qCreatedBy(makeId("Top.planeOp"),FACE);
            var sketch = newSketch(context, id + "F12", { "sketchPlane" : qUnion([Q0])});
            skLineSegment(sketch, "E2692.bottom", {"start": v(-155.53, 0) * mm, "end": v(-144.6, 0) * mm});
            skLineSegment(sketch, "E2692.top", {"start": v(-155.53, -41.12) * mm, "end": v(-144.6, -41.12) * mm});
            skLineSegment(sketch, "E2692.left", {"start": v(-155.53, 0) * mm, "end": v(-155.53, -41.12) * mm});
            skLineSegment(sketch, "E2692.right", {"start": v(-144.6, 0) * mm, "end": v(-144.6, -41.12) * mm});
            skSolve(sketch);
        }
        {
            var Q0;
            Q0 = qSketchRegion(id + "F12", true);
            extrude(context, id + "F13", {"entities" : qUnion([Q0]), "operationType" : NewBodyOperationType.ADD, "endBound" : BoundingType.SYMMETRIC, "depth" : 25.4 * mm, "offsetDistance" : 25.4 * mm});
        }
    });
